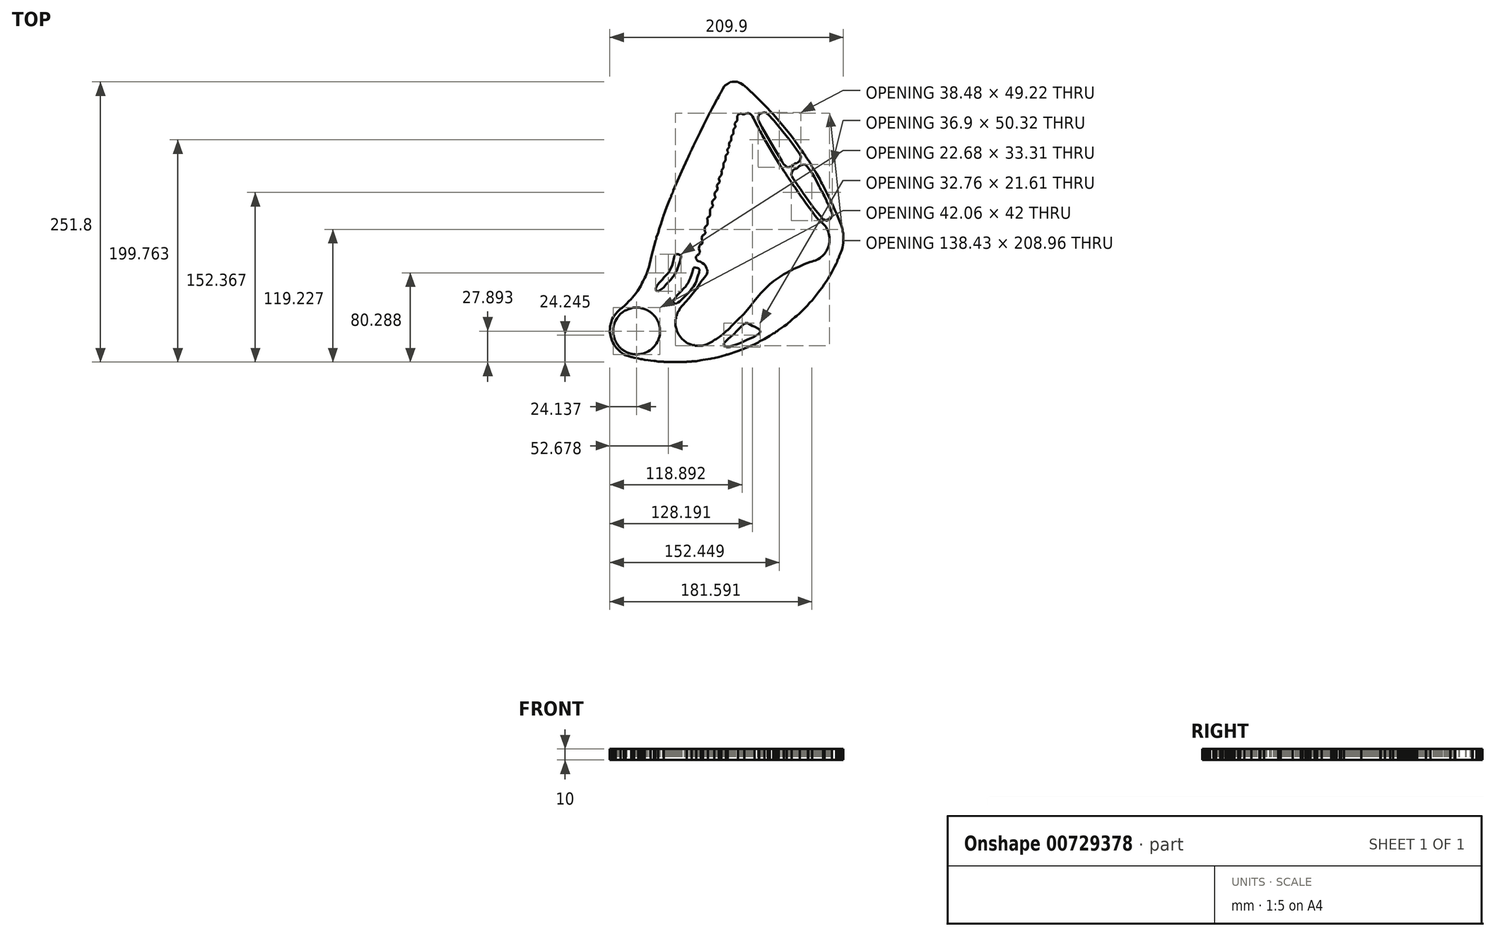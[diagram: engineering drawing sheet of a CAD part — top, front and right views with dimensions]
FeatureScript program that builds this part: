
annotation { "Feature Type Name" : "Feature", "Feature Type Description" : "" }
export const myFeature = defineFeature(function(context is Context, id is Id, definition is map)
    precondition{}
    {
        {
            var Q0;
            Q0=qCreatedBy(makeId("Top.planeOp"),FACE);
            var sketch = newSketch(context, id + "F0", { "sketchPlane" : qUnion([Q0])});
            skLineSegment(sketch, "E0", {"start": v(-166.72, -73.15) * mm, "end": v(-158.5, -73.15) * mm});
            skLineSegment(sketch, "E1", {"start": v(-158.5, -73.15) * mm, "end": v(-154.38, -73.15) * mm});
            skLineSegment(sketch, "E2", {"start": v(-154.38, -73.15) * mm, "end": v(-146.16, -73.15) * mm});
            skLineSegment(sketch, "E3", {"start": v(-146.16, -73.15) * mm, "end": v(-146.16, -73) * mm});
            skLineSegment(sketch, "E4", {"start": v(-146.16, -73) * mm, "end": v(-146.16, -72.91) * mm});
            skLineSegment(sketch, "E5", {"start": v(-146.16, -72.91) * mm, "end": v(-146.16, -72.76) * mm});
            skLineSegment(sketch, "E6", {"start": v(-146.16, -72.76) * mm, "end": v(-144.3, -72.76) * mm});
            skLineSegment(sketch, "E7", {"start": v(-144.3, -72.76) * mm, "end": v(-143.36, -72.76) * mm});
            skLineSegment(sketch, "E8", {"start": v(-143.36, -72.76) * mm, "end": v(-141.5, -72.76) * mm});
            skLineSegment(sketch, "E9", {"start": v(-141.5, -72.76) * mm, "end": v(-141.5, -72.6) * mm});
            skLineSegment(sketch, "E10", {"start": v(-141.5, -72.6) * mm, "end": v(-141.5, -72.53) * mm});
            skLineSegment(sketch, "E11", {"start": v(-141.5, -72.53) * mm, "end": v(-141.5, -72.37) * mm});
            skLineSegment(sketch, "E12", {"start": v(-141.5, -72.37) * mm, "end": v(-139.95, -72.37) * mm});
            skLineSegment(sketch, "E13", {"start": v(-139.95, -72.37) * mm, "end": v(-139.17, -72.37) * mm});
            skLineSegment(sketch, "E14", {"start": v(-139.17, -72.37) * mm, "end": v(-137.62, -72.37) * mm});
            skLineSegment(sketch, "E15", {"start": v(-137.62, -72.37) * mm, "end": v(-133.45, -71.54) * mm});
            skLineSegment(sketch, "E16", {"start": v(-133.45, -71.54) * mm, "end": v(-131.36, -71.2) * mm});
            skLineSegment(sketch, "E17", {"start": v(-131.36, -71.2) * mm, "end": v(-127.15, -70.62) * mm});
            skLineSegment(sketch, "E18", {"start": v(-127.15, -70.62) * mm, "end": v(-124.82, -70.16) * mm});
            skLineSegment(sketch, "E19", {"start": v(-124.82, -70.16) * mm, "end": v(-123.65, -69.93) * mm});
            skLineSegment(sketch, "E20", {"start": v(-123.65, -69.93) * mm, "end": v(-121.33, -69.46) * mm});
            skLineSegment(sketch, "E21", {"start": v(-121.33, -69.46) * mm, "end": v(-117.1, -68.56) * mm});
            skLineSegment(sketch, "E22", {"start": v(-117.1, -68.56) * mm, "end": v(-114.99, -68.02) * mm});
            skLineSegment(sketch, "E23", {"start": v(-114.99, -68.02) * mm, "end": v(-110.85, -66.74) * mm});
            skLineSegment(sketch, "E24", {"start": v(-110.85, -66.74) * mm, "end": v(-110.26, -66.5) * mm});
            skLineSegment(sketch, "E25", {"start": v(-110.26, -66.5) * mm, "end": v(-109.94, -66.42) * mm});
            skLineSegment(sketch, "E26", {"start": v(-109.94, -66.42) * mm, "end": v(-109.3, -66.36) * mm});
            skLineSegment(sketch, "E27", {"start": v(-109.3, -66.36) * mm, "end": v(-105.57, -65.12) * mm});
            skLineSegment(sketch, "E28", {"start": v(-105.57, -65.12) * mm, "end": v(-103.71, -64.5) * mm});
            skLineSegment(sketch, "E29", {"start": v(-103.71, -64.5) * mm, "end": v(-99.99, -63.25) * mm});
            skLineSegment(sketch, "E30", {"start": v(-99.99, -63.25) * mm, "end": v(-97.65, -62.34) * mm});
            skLineSegment(sketch, "E31", {"start": v(-97.65, -62.34) * mm, "end": v(-96.49, -61.87) * mm});
            skLineSegment(sketch, "E32", {"start": v(-96.49, -61.87) * mm, "end": v(-94.17, -60.93) * mm});
            skLineSegment(sketch, "E33", {"start": v(-94.17, -60.93) * mm, "end": v(-90.6, -59.37) * mm});
            skLineSegment(sketch, "E34", {"start": v(-90.6, -59.37) * mm, "end": v(-88.81, -58.6) * mm});
            skLineSegment(sketch, "E35", {"start": v(-88.81, -58.6) * mm, "end": v(-85.24, -57.05) * mm});
            skLineSegment(sketch, "E36", {"start": v(-85.24, -57.05) * mm, "end": v(-83.7, -56.27) * mm});
            skLineSegment(sketch, "E37", {"start": v(-83.7, -56.27) * mm, "end": v(-82.92, -55.88) * mm});
            skLineSegment(sketch, "E38", {"start": v(-82.92, -55.88) * mm, "end": v(-81.36, -55.1) * mm});
            skLineSegment(sketch, "E39", {"start": v(-81.36, -55.1) * mm, "end": v(-81.2, -54.95) * mm});
            skLineSegment(sketch, "E40", {"start": v(-81.2, -54.95) * mm, "end": v(-81.13, -54.87) * mm});
            skLineSegment(sketch, "E41", {"start": v(-81.13, -54.87) * mm, "end": v(-80.98, -54.72) * mm});
            skLineSegment(sketch, "E42", {"start": v(-80.98, -54.72) * mm, "end": v(-79.11, -53.79) * mm});
            skLineSegment(sketch, "E43", {"start": v(-79.11, -53.79) * mm, "end": v(-78.18, -53.32) * mm});
            skLineSegment(sketch, "E44", {"start": v(-78.18, -53.32) * mm, "end": v(-76.32, -52.39) * mm});
            skLineSegment(sketch, "E45", {"start": v(-76.32, -52.39) * mm, "end": v(-73, -50.47) * mm});
            skLineSegment(sketch, "E46", {"start": v(-73, -50.47) * mm, "end": v(-71.37, -49.46) * mm});
            skLineSegment(sketch, "E47", {"start": v(-71.37, -49.46) * mm, "end": v(-68.17, -47.35) * mm});
            skLineSegment(sketch, "E48", {"start": v(-68.17, -47.35) * mm, "end": v(-67.17, -46.84) * mm});
            skLineSegment(sketch, "E49", {"start": v(-67.17, -46.84) * mm, "end": v(-66.7, -46.52) * mm});
            skLineSegment(sketch, "E50", {"start": v(-66.7, -46.52) * mm, "end": v(-65.84, -45.8) * mm});
            skLineSegment(sketch, "E51", {"start": v(-65.84, -45.8) * mm, "end": v(-64.85, -45.29) * mm});
            skLineSegment(sketch, "E52", {"start": v(-64.85, -45.29) * mm, "end": v(-64.37, -44.97) * mm});
            skLineSegment(sketch, "E53", {"start": v(-64.37, -44.97) * mm, "end": v(-63.52, -44.24) * mm});
            skLineSegment(sketch, "E54", {"start": v(-63.52, -44.24) * mm, "end": v(-58.6, -41.03) * mm});
            skLineSegment(sketch, "E55", {"start": v(-58.6, -41.03) * mm, "end": v(-56.25, -39.23) * mm});
            skLineSegment(sketch, "E56", {"start": v(-56.25, -39.23) * mm, "end": v(-51.88, -35.32) * mm});
            skLineSegment(sketch, "E57", {"start": v(-51.88, -35.32) * mm, "end": v(-48.92, -32.85) * mm});
            skLineSegment(sketch, "E58", {"start": v(-48.92, -32.85) * mm, "end": v(-47.44, -31.6) * mm});
            skLineSegment(sketch, "E59", {"start": v(-47.44, -31.6) * mm, "end": v(-44.5, -29.11) * mm});
            skLineSegment(sketch, "E60", {"start": v(-44.5, -29.11) * mm, "end": v(-41.63, -26.24) * mm});
            skLineSegment(sketch, "E61", {"start": v(-41.63, -26.24) * mm, "end": v(-40.2, -24.8) * mm});
            skLineSegment(sketch, "E62", {"start": v(-40.2, -24.8) * mm, "end": v(-37.33, -21.93) * mm});
            skLineSegment(sketch, "E63", {"start": v(-37.33, -21.93) * mm, "end": v(-37.17, -21.62) * mm});
            skLineSegment(sketch, "E64", {"start": v(-37.17, -21.62) * mm, "end": v(-37.1, -21.47) * mm});
            skLineSegment(sketch, "E65", {"start": v(-37.1, -21.47) * mm, "end": v(-36.94, -21.16) * mm});
            skLineSegment(sketch, "E66", {"start": v(-36.94, -21.16) * mm, "end": v(-35.54, -19.76) * mm});
            skLineSegment(sketch, "E67", {"start": v(-35.54, -19.76) * mm, "end": v(-34.85, -19.06) * mm});
            skLineSegment(sketch, "E68", {"start": v(-34.85, -19.06) * mm, "end": v(-33.45, -17.67) * mm});
            skLineSegment(sketch, "E69", {"start": v(-33.45, -17.67) * mm, "end": v(-29.48, -12.63) * mm});
            skLineSegment(sketch, "E70", {"start": v(-29.48, -12.63) * mm, "end": v(-27.5, -10.11) * mm});
            skLineSegment(sketch, "E71", {"start": v(-27.5, -10.11) * mm, "end": v(-23.56, -5.06) * mm});
            skLineSegment(sketch, "E72", {"start": v(-23.56, -5.06) * mm, "end": v(-23.23, -4.1) * mm});
            skLineSegment(sketch, "E73", {"start": v(-23.23, -4.1) * mm, "end": v(-22.93, -3.62) * mm});
            skLineSegment(sketch, "E74", {"start": v(-22.93, -3.62) * mm, "end": v(-22.2, -2.92) * mm});
            skLineSegment(sketch, "E75", {"start": v(-22.2, -2.92) * mm, "end": v(-19.54, 1.41) * mm});
            skLineSegment(sketch, "E76", {"start": v(-19.54, 1.41) * mm, "end": v(-18.22, 3.59) * mm});
            skLineSegment(sketch, "E77", {"start": v(-18.22, 3.59) * mm, "end": v(-15.6, 7.94) * mm});
            skLineSegment(sketch, "E78", {"start": v(-15.6, 7.94) * mm, "end": v(-14.13, 10.89) * mm});
            skLineSegment(sketch, "E79", {"start": v(-14.13, 10.89) * mm, "end": v(-13.4, 12.36) * mm});
            skLineSegment(sketch, "E80", {"start": v(-13.4, 12.36) * mm, "end": v(-11.92, 15.31) * mm});
            skLineSegment(sketch, "E81", {"start": v(-11.92, 15.31) * mm, "end": v(-11.81, 15.62) * mm});
            skLineSegment(sketch, "E82", {"start": v(-11.81, 15.62) * mm, "end": v(-11.37, 15.72) * mm});
            skLineSegment(sketch, "E83", {"start": v(-6.48, 47.32) * mm, "end": v(-7.32, 50.1) * mm});
            skLineSegment(sketch, "E84", {"start": v(-7.32, 50.1) * mm, "end": v(-7.83, 51.46) * mm});
            skLineSegment(sketch, "E85", {"start": v(-7.83, 51.46) * mm, "end": v(-9, 54.11) * mm});
            skLineSegment(sketch, "E86", {"start": v(-9, 54.11) * mm, "end": v(-11.6, 60.33) * mm});
            skLineSegment(sketch, "E87", {"start": v(-11.6, 60.33) * mm, "end": v(-12.93, 63.44) * mm});
            skLineSegment(sketch, "E88", {"start": v(-12.93, 63.44) * mm, "end": v(-15.6, 69.63) * mm});
            skLineSegment(sketch, "E89", {"start": v(-15.6, 69.63) * mm, "end": v(-19.02, 76.46) * mm});
            skLineSegment(sketch, "E90", {"start": v(-19.02, 76.46) * mm, "end": v(-20.72, 79.87) * mm});
            skLineSegment(sketch, "E91", {"start": v(-20.72, 79.87) * mm, "end": v(-24.14, 86.7) * mm});
            skLineSegment(sketch, "E92", {"start": v(-24.14, 86.7) * mm, "end": v(-24.3, 86.86) * mm});
            skLineSegment(sketch, "E93", {"start": v(-24.3, 86.86) * mm, "end": v(-24.37, 86.93) * mm});
            skLineSegment(sketch, "E94", {"start": v(-24.37, 86.93) * mm, "end": v(-24.53, 87.09) * mm});
            skLineSegment(sketch, "E95", {"start": v(-24.53, 87.09) * mm, "end": v(-25.3, 88.64) * mm});
            skLineSegment(sketch, "E96", {"start": v(-25.3, 88.64) * mm, "end": v(-25.69, 89.42) * mm});
            skLineSegment(sketch, "E97", {"start": v(-25.69, 89.42) * mm, "end": v(-26.47, 90.97) * mm});
            skLineSegment(sketch, "E98", {"start": v(-26.47, 90.97) * mm, "end": v(-29.11, 95.75) * mm});
            skLineSegment(sketch, "E99", {"start": v(-29.11, 95.75) * mm, "end": v(-30.56, 98.1) * mm});
            skLineSegment(sketch, "E100", {"start": v(-30.56, 98.1) * mm, "end": v(-33.64, 102.6) * mm});
            skLineSegment(sketch, "E101", {"start": v(-33.64, 102.6) * mm, "end": v(-34.05, 103.97) * mm});
            skLineSegment(sketch, "E102", {"start": v(-34.05, 103.97) * mm, "end": v(-34.43, 104.66) * mm});
            skLineSegment(sketch, "E103", {"start": v(-34.43, 104.66) * mm, "end": v(-35.39, 105.71) * mm});
            skLineSegment(sketch, "E104", {"start": v(-35.39, 105.71) * mm, "end": v(-36.35, 107.5) * mm});
            skLineSegment(sketch, "E105", {"start": v(-36.35, 107.5) * mm, "end": v(-36.9, 108.36) * mm});
            skLineSegment(sketch, "E106", {"start": v(-36.9, 108.36) * mm, "end": v(-38.1, 109.98) * mm});
            skLineSegment(sketch, "E107", {"start": v(-38.1, 109.98) * mm, "end": v(-38.61, 110.98) * mm});
            skLineSegment(sketch, "E108", {"start": v(-38.61, 110.98) * mm, "end": v(-38.93, 111.46) * mm});
            skLineSegment(sketch, "E109", {"start": v(-38.93, 111.46) * mm, "end": v(-39.66, 112.3) * mm});
            skLineSegment(sketch, "E110", {"start": v(-39.66, 112.3) * mm, "end": v(-40.16, 113.3) * mm});
            skLineSegment(sketch, "E111", {"start": v(-40.16, 113.3) * mm, "end": v(-40.48, 113.78) * mm});
            skLineSegment(sketch, "E112", {"start": v(-40.48, 113.78) * mm, "end": v(-41.2, 114.63) * mm});
            skLineSegment(sketch, "E113", {"start": v(-41.2, 114.63) * mm, "end": v(-42.1, 116.36) * mm});
            skLineSegment(sketch, "E114", {"start": v(-42.1, 116.36) * mm, "end": v(-42.71, 117.18) * mm});
            skLineSegment(sketch, "E115", {"start": v(-42.71, 117.18) * mm, "end": v(-44.12, 118.51) * mm});
            skLineSegment(sketch, "E116", {"start": v(-44.12, 118.51) * mm, "end": v(-44.03, 119.03) * mm});
            skLineSegment(sketch, "E117", {"start": v(-44.03, 119.03) * mm, "end": v(-44.24, 119.44) * mm});
            skLineSegment(sketch, "E118", {"start": v(-44.24, 119.44) * mm, "end": v(-44.7, 119.68) * mm});
            skLineSegment(sketch, "E119", {"start": v(-44.7, 119.68) * mm, "end": v(-50.32, 127.77) * mm});
            skLineSegment(sketch, "E120", {"start": v(-50.32, 127.77) * mm, "end": v(-53.32, 131.7) * mm});
            skLineSegment(sketch, "E121", {"start": v(-53.32, 131.7) * mm, "end": v(-59.64, 139.27) * mm});
            skLineSegment(sketch, "E122", {"start": v(-59.64, 139.27) * mm, "end": v(-63.14, 143.38) * mm});
            skLineSegment(sketch, "E123", {"start": v(-63.14, 143.38) * mm, "end": v(-64.88, 145.43) * mm});
            skLineSegment(sketch, "E124", {"start": v(-64.88, 145.43) * mm, "end": v(-68.37, 149.55) * mm});
            skLineSegment(sketch, "E125", {"start": v(-68.37, 149.55) * mm, "end": v(-69.92, 151.1) * mm});
            skLineSegment(sketch, "E126", {"start": v(-69.92, 151.1) * mm, "end": v(-70.7, 151.88) * mm});
            skLineSegment(sketch, "E127", {"start": v(-70.7, 151.88) * mm, "end": v(-72.25, 153.43) * mm});
            skLineSegment(sketch, "E128", {"start": v(-72.25, 153.43) * mm, "end": v(-72.4, 153.74) * mm});
            skLineSegment(sketch, "E129", {"start": v(-72.4, 153.74) * mm, "end": v(-72.48, 153.9) * mm});
            skLineSegment(sketch, "E130", {"start": v(-72.48, 153.9) * mm, "end": v(-72.63, 154.2) * mm});
            skLineSegment(sketch, "E131", {"start": v(-72.63, 154.2) * mm, "end": v(-78.6, 160.18) * mm});
            skLineSegment(sketch, "E132", {"start": v(-78.6, 160.18) * mm, "end": v(-81.6, 163.17) * mm});
            skLineSegment(sketch, "E133", {"start": v(-81.6, 163.17) * mm, "end": v(-87.57, 169.15) * mm});
            skLineSegment(sketch, "E134", {"start": v(-87.57, 169.15) * mm, "end": v(-87.88, 169.3) * mm});
            skLineSegment(sketch, "E135", {"start": v(-87.88, 169.3) * mm, "end": v(-88.04, 169.38) * mm});
            skLineSegment(sketch, "E136", {"start": v(-88.04, 169.38) * mm, "end": v(-88.35, 169.53) * mm});
            skLineSegment(sketch, "E137", {"start": v(-88.35, 169.53) * mm, "end": v(-89.74, 170.93) * mm});
            skLineSegment(sketch, "E138", {"start": v(-89.74, 170.93) * mm, "end": v(-90.44, 171.63) * mm});
            skLineSegment(sketch, "E139", {"start": v(-90.44, 171.63) * mm, "end": v(-91.84, 173.03) * mm});
            skLineSegment(sketch, "E140", {"start": v(-91.84, 173.03) * mm, "end": v(-94.02, 174.98) * mm});
            skLineSegment(sketch, "E141", {"start": v(-94.02, 174.98) * mm, "end": v(-95.2, 175.89) * mm});
            skLineSegment(sketch, "E142", {"start": v(-95.2, 175.89) * mm, "end": v(-97.66, 177.49) * mm});
            skLineSegment(sketch, "E143", {"start": v(-97.66, 177.49) * mm, "end": v(-98.78, 177.87) * mm});
            skLineSegment(sketch, "E144", {"start": v(-98.78, 177.87) * mm, "end": v(-99.33, 178.1) * mm});
            skLineSegment(sketch, "E145", {"start": v(-99.33, 178.1) * mm, "end": v(-100.37, 178.65) * mm});
            skLineSegment(sketch, "E146", {"start": v(-100.37, 178.65) * mm, "end": v(-102.31, 178.65) * mm});
            skLineSegment(sketch, "E147", {"start": v(-102.31, 178.65) * mm, "end": v(-103.28, 178.65) * mm});
            skLineSegment(sketch, "E148", {"start": v(-103.28, 178.65) * mm, "end": v(-105.22, 178.65) * mm});
            skLineSegment(sketch, "E149", {"start": v(-105.22, 178.65) * mm, "end": v(-106.96, 178.31) * mm});
            skLineSegment(sketch, "E150", {"start": v(-106.96, 178.31) * mm, "end": v(-107.85, 177.93) * mm});
            skLineSegment(sketch, "E151", {"start": v(-107.85, 177.93) * mm, "end": v(-109.3, 176.9) * mm});
            skLineSegment(sketch, "E152", {"start": v(-109.3, 176.9) * mm, "end": v(-111.4, 175.61) * mm});
            skLineSegment(sketch, "E153", {"start": v(-111.4, 175.61) * mm, "end": v(-112.37, 174.6) * mm});
            skLineSegment(sketch, "E154", {"start": v(-112.37, 174.6) * mm, "end": v(-113.57, 172.44) * mm});
            skLineSegment(sketch, "E155", {"start": v(-113.57, 172.44) * mm, "end": v(-114.64, 170.38) * mm});
            skLineSegment(sketch, "E156", {"start": v(-114.64, 170.38) * mm, "end": v(-115.23, 169.36) * mm});
            skLineSegment(sketch, "E157", {"start": v(-115.23, 169.36) * mm, "end": v(-116.48, 167.4) * mm});
            skLineSegment(sketch, "E158", {"start": v(-116.48, 167.4) * mm, "end": v(-117.25, 165.85) * mm});
            skLineSegment(sketch, "E159", {"start": v(-117.25, 165.85) * mm, "end": v(-117.64, 165.07) * mm});
            skLineSegment(sketch, "E160", {"start": v(-117.64, 165.07) * mm, "end": v(-118.42, 163.52) * mm});
            skLineSegment(sketch, "E161", {"start": v(-118.42, 163.52) * mm, "end": v(-118.57, 163.36) * mm});
            skLineSegment(sketch, "E162", {"start": v(-118.57, 163.36) * mm, "end": v(-118.65, 163.29) * mm});
            skLineSegment(sketch, "E163", {"start": v(-118.65, 163.29) * mm, "end": v(-118.8, 163.13) * mm});
            skLineSegment(sketch, "E164", {"start": v(-118.8, 163.13) * mm, "end": v(-119.89, 160.96) * mm});
            skLineSegment(sketch, "E165", {"start": v(-119.89, 160.96) * mm, "end": v(-120.43, 159.87) * mm});
            skLineSegment(sketch, "E166", {"start": v(-120.43, 159.87) * mm, "end": v(-121.52, 157.7) * mm});
            skLineSegment(sketch, "E167", {"start": v(-121.52, 157.7) * mm, "end": v(-121.67, 157.54) * mm});
            skLineSegment(sketch, "E168", {"start": v(-121.67, 157.54) * mm, "end": v(-121.75, 157.47) * mm});
            skLineSegment(sketch, "E169", {"start": v(-121.75, 157.47) * mm, "end": v(-121.9, 157.31) * mm});
            skLineSegment(sketch, "E170", {"start": v(-121.9, 157.31) * mm, "end": v(-123.15, 154.83) * mm});
            skLineSegment(sketch, "E171", {"start": v(-123.15, 154.83) * mm, "end": v(-123.77, 153.59) * mm});
            skLineSegment(sketch, "E172", {"start": v(-123.77, 153.59) * mm, "end": v(-125.01, 151.1) * mm});
            skLineSegment(sketch, "E173", {"start": v(-125.01, 151.1) * mm, "end": v(-125.17, 150.95) * mm});
            skLineSegment(sketch, "E174", {"start": v(-125.17, 150.95) * mm, "end": v(-125.24, 150.87) * mm});
            skLineSegment(sketch, "E175", {"start": v(-125.24, 150.87) * mm, "end": v(-125.4, 150.72) * mm});
            skLineSegment(sketch, "E176", {"start": v(-125.4, 150.72) * mm, "end": v(-131.14, 139.23) * mm});
            skLineSegment(sketch, "E177", {"start": v(-131.14, 139.23) * mm, "end": v(-134.01, 133.5) * mm});
            skLineSegment(sketch, "E178", {"start": v(-134.01, 133.5) * mm, "end": v(-139.75, 122) * mm});
            skLineSegment(sketch, "E179", {"start": v(-139.75, 122) * mm, "end": v(-139.9, 121.54) * mm});
            skLineSegment(sketch, "E180", {"start": v(-139.9, 121.54) * mm, "end": v(-139.99, 121.3) * mm});
            skLineSegment(sketch, "E181", {"start": v(-139.99, 121.3) * mm, "end": v(-140.14, 120.84) * mm});
            skLineSegment(sketch, "E182", {"start": v(-140.14, 120.84) * mm, "end": v(-141.23, 118.67) * mm});
            skLineSegment(sketch, "E183", {"start": v(-141.23, 118.67) * mm, "end": v(-141.77, 117.58) * mm});
            skLineSegment(sketch, "E184", {"start": v(-141.77, 117.58) * mm, "end": v(-142.86, 115.41) * mm});
            skLineSegment(sketch, "E185", {"start": v(-142.86, 115.41) * mm, "end": v(-143.01, 114.95) * mm});
            skLineSegment(sketch, "E186", {"start": v(-143.01, 114.95) * mm, "end": v(-143.1, 114.71) * mm});
            skLineSegment(sketch, "E187", {"start": v(-143.1, 114.71) * mm, "end": v(-143.25, 114.25) * mm});
            skLineSegment(sketch, "E188", {"start": v(-143.25, 114.25) * mm, "end": v(-144.18, 112.38) * mm});
            skLineSegment(sketch, "E189", {"start": v(-144.18, 112.38) * mm, "end": v(-144.64, 111.45) * mm});
            skLineSegment(sketch, "E190", {"start": v(-144.64, 111.45) * mm, "end": v(-145.57, 109.6) * mm});
            skLineSegment(sketch, "E191", {"start": v(-145.57, 109.6) * mm, "end": v(-150.57, 98.27) * mm});
            skLineSegment(sketch, "E192", {"start": v(-150.57, 98.27) * mm, "end": v(-153.05, 92.6) * mm});
            skLineSegment(sketch, "E193", {"start": v(-153.05, 92.6) * mm, "end": v(-157.99, 81.27) * mm});
            skLineSegment(sketch, "E194", {"start": v(-157.99, 81.27) * mm, "end": v(-158.58, 79.3) * mm});
            skLineSegment(sketch, "E195", {"start": v(-158.58, 79.3) * mm, "end": v(-159.02, 78.34) * mm});
            skLineSegment(sketch, "E196", {"start": v(-159.02, 78.34) * mm, "end": v(-160.12, 76.61) * mm});
            skLineSegment(sketch, "E197", {"start": v(-160.12, 76.61) * mm, "end": v(-160.01, 75.81) * mm});
            skLineSegment(sketch, "E198", {"start": v(-160.01, 75.81) * mm, "end": v(-160.17, 75.28) * mm});
            skLineSegment(sketch, "E199", {"start": v(-160.17, 75.28) * mm, "end": v(-160.7, 74.67) * mm});
            skLineSegment(sketch, "E200", {"start": v(-160.7, 74.67) * mm, "end": v(-161.25, 73.1) * mm});
            skLineSegment(sketch, "E201", {"start": v(-161.25, 73.1) * mm, "end": v(-161.56, 72.31) * mm});
            skLineSegment(sketch, "E202", {"start": v(-161.56, 72.31) * mm, "end": v(-162.26, 70.8) * mm});
            skLineSegment(sketch, "E203", {"start": v(-162.26, 70.8) * mm, "end": v(-163.48, 67.53) * mm});
            skLineSegment(sketch, "E204", {"start": v(-163.48, 67.53) * mm, "end": v(-164.1, 65.9) * mm});
            skLineSegment(sketch, "E205", {"start": v(-164.1, 65.9) * mm, "end": v(-165.36, 62.65) * mm});
            skLineSegment(sketch, "E206", {"start": v(-165.36, 62.65) * mm, "end": v(-165.98, 60.78) * mm});
            skLineSegment(sketch, "E207", {"start": v(-165.98, 60.78) * mm, "end": v(-166.3, 59.85) * mm});
            skLineSegment(sketch, "E208", {"start": v(-166.3, 59.85) * mm, "end": v(-166.91, 57.99) * mm});
            skLineSegment(sketch, "E209", {"start": v(-166.91, 57.99) * mm, "end": v(-167.07, 57.68) * mm});
            skLineSegment(sketch, "E210", {"start": v(-167.07, 57.68) * mm, "end": v(-167.15, 57.52) * mm});
            skLineSegment(sketch, "E211", {"start": v(-167.15, 57.52) * mm, "end": v(-167.3, 57.21) * mm});
            skLineSegment(sketch, "E212", {"start": v(-167.3, 57.21) * mm, "end": v(-168.7, 53.02) * mm});
            skLineSegment(sketch, "E213", {"start": v(-168.7, 53.02) * mm, "end": v(-169.4, 50.93) * mm});
            skLineSegment(sketch, "E214", {"start": v(-169.4, 50.93) * mm, "end": v(-170.8, 46.74) * mm});
            skLineSegment(sketch, "E215", {"start": v(-170.8, 46.74) * mm, "end": v(-171.52, 43.56) * mm});
            skLineSegment(sketch, "E216", {"start": v(-171.52, 43.56) * mm, "end": v(-172.03, 41.98) * mm});
            skLineSegment(sketch, "E217", {"start": v(-172.03, 41.98) * mm, "end": v(-173.31, 38.98) * mm});
            skLineSegment(sketch, "E218", {"start": v(-173.31, 38.98) * mm, "end": v(-173.26, 37.87) * mm});
            skLineSegment(sketch, "E219", {"start": v(-173.26, 37.87) * mm, "end": v(-173.4, 37.25) * mm});
            skLineSegment(sketch, "E220", {"start": v(-173.4, 37.25) * mm, "end": v(-173.9, 36.26) * mm});
            skLineSegment(sketch, "E221", {"start": v(-173.9, 36.26) * mm, "end": v(-176.43, 26.66) * mm});
            skLineSegment(sketch, "E222", {"start": v(-176.43, 26.66) * mm, "end": v(-177.67, 21.84) * mm});
            skLineSegment(sketch, "E223", {"start": v(-177.67, 21.84) * mm, "end": v(-180.1, 12.2) * mm});
            skLineSegment(sketch, "E224", {"start": v(-180.1, 12.2) * mm, "end": v(-180.72, 10.35) * mm});
            skLineSegment(sketch, "E225", {"start": v(-180.72, 10.35) * mm, "end": v(-181.04, 9.42) * mm});
            skLineSegment(sketch, "E226", {"start": v(-181.04, 9.42) * mm, "end": v(-181.66, 7.55) * mm});
            skLineSegment(sketch, "E227", {"start": v(-181.66, 7.55) * mm, "end": v(-182.98, 4.15) * mm});
            skLineSegment(sketch, "E228", {"start": v(-182.98, 4.15) * mm, "end": v(-183.72, 2.48) * mm});
            skLineSegment(sketch, "E229", {"start": v(-183.72, 2.48) * mm, "end": v(-185.34, -0.79) * mm});
            skLineSegment(sketch, "E230", {"start": v(-185.34, -0.79) * mm, "end": v(-186.29, -2.37) * mm});
            skLineSegment(sketch, "E231", {"start": v(-186.29, -2.37) * mm, "end": v(-186.72, -3.19) * mm});
            skLineSegment(sketch, "E232", {"start": v(-186.72, -3.19) * mm, "end": v(-187.48, -4.86) * mm});
            skLineSegment(sketch, "E233", {"start": v(-187.48, -4.86) * mm, "end": v(-190.18, -9.2) * mm});
            skLineSegment(sketch, "E234", {"start": v(-190.18, -9.2) * mm, "end": v(-191.7, -11.27) * mm});
            skLineSegment(sketch, "E235", {"start": v(-191.7, -11.27) * mm, "end": v(-195.04, -15.14) * mm});
            skLineSegment(sketch, "E236", {"start": v(-195.04, -15.14) * mm, "end": v(-195.34, -15.48) * mm});
            skLineSegment(sketch, "E237", {"start": v(-195.34, -15.48) * mm, "end": v(-195.46, -15.7) * mm});
            skLineSegment(sketch, "E238", {"start": v(-195.46, -15.7) * mm, "end": v(-195.62, -16.11) * mm});
            skLineSegment(sketch, "E239", {"start": v(-195.62, -16.11) * mm, "end": v(-198.34, -18.83) * mm});
            skLineSegment(sketch, "E240", {"start": v(-198.34, -18.83) * mm, "end": v(-199.7, -20.19) * mm});
            skLineSegment(sketch, "E241", {"start": v(-199.7, -20.19) * mm, "end": v(-202.41, -22.9) * mm});
            skLineSegment(sketch, "E242", {"start": v(-202.41, -22.9) * mm, "end": v(-203.65, -23.83) * mm});
            skLineSegment(sketch, "E243", {"start": v(-203.65, -23.83) * mm, "end": v(-204.28, -24.3) * mm});
            skLineSegment(sketch, "E244", {"start": v(-204.28, -24.3) * mm, "end": v(-205.52, -25.23) * mm});
            skLineSegment(sketch, "E245", {"start": v(-205.52, -25.23) * mm, "end": v(-207.3, -27.02) * mm});
            skLineSegment(sketch, "E246", {"start": v(-207.3, -27.02) * mm, "end": v(-208.2, -27.9) * mm});
            skLineSegment(sketch, "E247", {"start": v(-208.2, -27.9) * mm, "end": v(-209.98, -29.7) * mm});
            skLineSegment(sketch, "E248", {"start": v(-209.98, -29.7) * mm, "end": v(-212.07, -32.68) * mm});
            skLineSegment(sketch, "E249", {"start": v(-212.07, -32.68) * mm, "end": v(-212.92, -34.38) * mm});
            skLineSegment(sketch, "E250", {"start": v(-212.92, -34.38) * mm, "end": v(-214.05, -37.84) * mm});
            skLineSegment(sketch, "E251", {"start": v(-214.05, -37.84) * mm, "end": v(-214.84, -40.88) * mm});
            skLineSegment(sketch, "E252", {"start": v(-214.84, -40.88) * mm, "end": v(-215.07, -42.46) * mm});
            skLineSegment(sketch, "E253", {"start": v(-215.07, -42.46) * mm, "end": v(-215.22, -45.6) * mm});
            skLineSegment(sketch, "E254", {"start": v(-215.22, -45.6) * mm, "end": v(-214.66, -48.73) * mm});
            skLineSegment(sketch, "E255", {"start": v(-214.66, -48.73) * mm, "end": v(-214.3, -50.3) * mm});
            skLineSegment(sketch, "E256", {"start": v(-214.3, -50.3) * mm, "end": v(-213.47, -53.36) * mm});
            skLineSegment(sketch, "E257", {"start": v(-213.47, -53.36) * mm, "end": v(-212.7, -54.91) * mm});
            skLineSegment(sketch, "E258", {"start": v(-212.7, -54.91) * mm, "end": v(-212.3, -55.69) * mm});
            skLineSegment(sketch, "E259", {"start": v(-212.3, -55.69) * mm, "end": v(-211.53, -57.24) * mm});
            skLineSegment(sketch, "E260", {"start": v(-211.53, -57.24) * mm, "end": v(-210.79, -58.08) * mm});
            skLineSegment(sketch, "E261", {"start": v(-210.79, -58.08) * mm, "end": v(-210.47, -58.56) * mm});
            skLineSegment(sketch, "E262", {"start": v(-210.47, -58.56) * mm, "end": v(-209.98, -59.57) * mm});
            skLineSegment(sketch, "E263", {"start": v(-209.98, -59.57) * mm, "end": v(-208.2, -61.35) * mm});
            skLineSegment(sketch, "E264", {"start": v(-208.2, -61.35) * mm, "end": v(-207.3, -62.24) * mm});
            skLineSegment(sketch, "E265", {"start": v(-207.3, -62.24) * mm, "end": v(-205.52, -64.03) * mm});
            skLineSegment(sketch, "E266", {"start": v(-205.52, -64.03) * mm, "end": v(-202.68, -66.03) * mm});
            skLineSegment(sketch, "E267", {"start": v(-202.68, -66.03) * mm, "end": v(-201.06, -66.84) * mm});
            skLineSegment(sketch, "E268", {"start": v(-201.06, -66.84) * mm, "end": v(-197.76, -67.9) * mm});
            skLineSegment(sketch, "E269", {"start": v(-197.76, -67.9) * mm, "end": v(-196.07, -68.45) * mm});
            skLineSegment(sketch, "E270", {"start": v(-196.07, -68.45) * mm, "end": v(-195.22, -68.68) * mm});
            skLineSegment(sketch, "E271", {"start": v(-195.22, -68.68) * mm, "end": v(-193.49, -69.07) * mm});
            skLineSegment(sketch, "E272", {"start": v(-193.49, -69.07) * mm, "end": v(-191.94, -69.38) * mm});
            skLineSegment(sketch, "E273", {"start": v(-191.94, -69.38) * mm, "end": v(-191.16, -69.54) * mm});
            skLineSegment(sketch, "E274", {"start": v(-191.16, -69.54) * mm, "end": v(-189.6, -69.85) * mm});
            skLineSegment(sketch, "E275", {"start": v(-189.6, -69.85) * mm, "end": v(-187.3, -70.39) * mm});
            skLineSegment(sketch, "E276", {"start": v(-187.3, -70.39) * mm, "end": v(-186.13, -70.62) * mm});
            skLineSegment(sketch, "E277", {"start": v(-186.13, -70.62) * mm, "end": v(-183.79, -71.01) * mm});
            skLineSegment(sketch, "E278", {"start": v(-183.79, -71.01) * mm, "end": v(-181.62, -71.32) * mm});
            skLineSegment(sketch, "E279", {"start": v(-181.62, -71.32) * mm, "end": v(-180.53, -71.48) * mm});
            skLineSegment(sketch, "E280", {"start": v(-180.53, -71.48) * mm, "end": v(-178.36, -71.79) * mm});
            skLineSegment(sketch, "E281", {"start": v(-178.36, -71.79) * mm, "end": v(-175.7, -71.93) * mm});
            skLineSegment(sketch, "E282", {"start": v(-175.7, -71.93) * mm, "end": v(-174.35, -72.13) * mm});
            skLineSegment(sketch, "E283", {"start": v(-174.35, -72.13) * mm, "end": v(-171.76, -72.76) * mm});
            skLineSegment(sketch, "E284", {"start": v(-171.76, -72.76) * mm, "end": v(-169.75, -72.76) * mm});
            skLineSegment(sketch, "E285", {"start": v(-169.75, -72.76) * mm, "end": v(-168.74, -72.76) * mm});
            skLineSegment(sketch, "E286", {"start": v(-168.74, -72.76) * mm, "end": v(-166.72, -72.76) * mm});
            skLineSegment(sketch, "E287", {"start": v(-166.72, -72.76) * mm, "end": v(-166.72, -72.91) * mm});
            skLineSegment(sketch, "E288", {"start": v(-166.72, -72.91) * mm, "end": v(-166.72, -73) * mm});
            skLineSegment(sketch, "E289", {"start": v(-166.72, -73) * mm, "end": v(-166.72, -73.15) * mm});
            skLineSegment(sketch, "E290", {"start": v(-164, -71.98) * mm, "end": v(-158.1, -71.98) * mm});
            skLineSegment(sketch, "E291", {"start": v(-158.1, -71.98) * mm, "end": v(-155.16, -71.98) * mm});
            skLineSegment(sketch, "E292", {"start": v(-155.16, -71.98) * mm, "end": v(-149.26, -71.98) * mm});
            skLineSegment(sketch, "E293", {"start": v(-149.26, -71.98) * mm, "end": v(-149.26, -71.83) * mm});
            skLineSegment(sketch, "E294", {"start": v(-149.26, -71.83) * mm, "end": v(-149.26, -71.75) * mm});
            skLineSegment(sketch, "E295", {"start": v(-149.26, -71.75) * mm, "end": v(-149.26, -71.6) * mm});
            skLineSegment(sketch, "E296", {"start": v(-149.26, -71.6) * mm, "end": v(-146.78, -71.6) * mm});
            skLineSegment(sketch, "E297", {"start": v(-146.78, -71.6) * mm, "end": v(-145.54, -71.6) * mm});
            skLineSegment(sketch, "E298", {"start": v(-145.54, -71.6) * mm, "end": v(-143.05, -71.6) * mm});
            skLineSegment(sketch, "E299", {"start": v(-143.05, -71.6) * mm, "end": v(-143.05, -71.44) * mm});
            skLineSegment(sketch, "E300", {"start": v(-143.05, -71.44) * mm, "end": v(-143.05, -71.36) * mm});
            skLineSegment(sketch, "E301", {"start": v(-143.05, -71.36) * mm, "end": v(-143.05, -71.2) * mm});
            skLineSegment(sketch, "E302", {"start": v(-143.05, -71.2) * mm, "end": v(-141.35, -71.2) * mm});
            skLineSegment(sketch, "E303", {"start": v(-141.35, -71.2) * mm, "end": v(-140.5, -71.2) * mm});
            skLineSegment(sketch, "E304", {"start": v(-140.5, -71.2) * mm, "end": v(-138.78, -71.2) * mm});
            skLineSegment(sketch, "E305", {"start": v(-138.78, -71.2) * mm, "end": v(-137.65, -70.65) * mm});
            skLineSegment(sketch, "E306", {"start": v(-137.65, -70.65) * mm, "end": v(-136.94, -70.52) * mm});
            skLineSegment(sketch, "E307", {"start": v(-136.94, -70.52) * mm, "end": v(-135.68, -70.62) * mm});
            skLineSegment(sketch, "E308", {"start": v(-135.68, -70.62) * mm, "end": v(-133.5, -70.31) * mm});
            skLineSegment(sketch, "E309", {"start": v(-133.5, -70.31) * mm, "end": v(-132.42, -70.16) * mm});
            skLineSegment(sketch, "E310", {"start": v(-132.42, -70.16) * mm, "end": v(-130.25, -69.85) * mm});
            skLineSegment(sketch, "E311", {"start": v(-130.25, -69.85) * mm, "end": v(-129.31, -69.73) * mm});
            skLineSegment(sketch, "E312", {"start": v(-129.31, -69.73) * mm, "end": v(-128.84, -69.66) * mm});
            skLineSegment(sketch, "E313", {"start": v(-128.84, -69.66) * mm, "end": v(-127.92, -69.46) * mm});
            skLineSegment(sketch, "E314", {"start": v(-127.92, -69.46) * mm, "end": v(-125.6, -69) * mm});
            skLineSegment(sketch, "E315", {"start": v(-125.6, -69) * mm, "end": v(-124.43, -68.76) * mm});
            skLineSegment(sketch, "E316", {"start": v(-124.43, -68.76) * mm, "end": v(-122.1, -68.3) * mm});
            skLineSegment(sketch, "E317", {"start": v(-122.1, -68.3) * mm, "end": v(-120.71, -67.94) * mm});
            skLineSegment(sketch, "E318", {"start": v(-120.71, -67.94) * mm, "end": v(-120.02, -67.79) * mm});
            skLineSegment(sketch, "E319", {"start": v(-120.02, -67.79) * mm, "end": v(-118.6, -67.52) * mm});
            skLineSegment(sketch, "E320", {"start": v(-118.6, -67.52) * mm, "end": v(-116.75, -67.06) * mm});
            skLineSegment(sketch, "E321", {"start": v(-116.75, -67.06) * mm, "end": v(-115.82, -66.82) * mm});
            skLineSegment(sketch, "E322", {"start": v(-115.82, -66.82) * mm, "end": v(-113.95, -66.36) * mm});
            skLineSegment(sketch, "E323", {"start": v(-113.95, -66.36) * mm, "end": v(-111.32, -65.57) * mm});
            skLineSegment(sketch, "E324", {"start": v(-111.32, -65.57) * mm, "end": v(-110, -65.18) * mm});
            skLineSegment(sketch, "E325", {"start": v(-110, -65.18) * mm, "end": v(-107.36, -64.42) * mm});
            skLineSegment(sketch, "E326", {"start": v(-107.36, -64.42) * mm, "end": v(-105.03, -63.64) * mm});
            skLineSegment(sketch, "E327", {"start": v(-105.03, -63.64) * mm, "end": v(-103.87, -63.25) * mm});
            skLineSegment(sketch, "E328", {"start": v(-103.87, -63.25) * mm, "end": v(-101.54, -62.48) * mm});
            skLineSegment(sketch, "E329", {"start": v(-101.54, -62.48) * mm, "end": v(-99.2, -61.56) * mm});
            skLineSegment(sketch, "E330", {"start": v(-99.2, -61.56) * mm, "end": v(-98.04, -61.1) * mm});
            skLineSegment(sketch, "E331", {"start": v(-98.04, -61.1) * mm, "end": v(-95.72, -60.15) * mm});
            skLineSegment(sketch, "E332", {"start": v(-95.72, -60.15) * mm, "end": v(-93.08, -59.08) * mm});
            skLineSegment(sketch, "E333", {"start": v(-93.08, -59.08) * mm, "end": v(-91.76, -58.53) * mm});
            skLineSegment(sketch, "E334", {"start": v(-91.76, -58.53) * mm, "end": v(-89.12, -57.43) * mm});
            skLineSegment(sketch, "E335", {"start": v(-89.12, -57.43) * mm, "end": v(-84.78, -55.26) * mm});
            skLineSegment(sketch, "E336", {"start": v(-84.78, -55.26) * mm, "end": v(-82.6, -54.17) * mm});
            skLineSegment(sketch, "E337", {"start": v(-82.6, -54.17) * mm, "end": v(-78.26, -52) * mm});
            skLineSegment(sketch, "E338", {"start": v(-78.26, -52) * mm, "end": v(-74.6, -49.98) * mm});
            skLineSegment(sketch, "E339", {"start": v(-74.6, -49.98) * mm, "end": v(-72.81, -48.9) * mm});
            skLineSegment(sketch, "E340", {"start": v(-72.81, -48.9) * mm, "end": v(-69.34, -46.57) * mm});
            skLineSegment(sketch, "E341", {"start": v(-69.34, -46.57) * mm, "end": v(-67.37, -45.5) * mm});
            skLineSegment(sketch, "E342", {"start": v(-67.37, -45.5) * mm, "end": v(-66.42, -44.87) * mm});
            skLineSegment(sketch, "E343", {"start": v(-66.42, -44.87) * mm, "end": v(-64.68, -43.47) * mm});
            skLineSegment(sketch, "E344", {"start": v(-64.68, -43.47) * mm, "end": v(-63.68, -42.96) * mm});
            skLineSegment(sketch, "E345", {"start": v(-63.68, -42.96) * mm, "end": v(-63.2, -42.64) * mm});
            skLineSegment(sketch, "E346", {"start": v(-63.2, -42.64) * mm, "end": v(-62.35, -41.91) * mm});
            skLineSegment(sketch, "E347", {"start": v(-62.35, -41.91) * mm, "end": v(-56.7, -38.05) * mm});
            skLineSegment(sketch, "E348", {"start": v(-56.7, -38.05) * mm, "end": v(-54, -35.9) * mm});
            skLineSegment(sketch, "E349", {"start": v(-54, -35.9) * mm, "end": v(-48.97, -31.24) * mm});
            skLineSegment(sketch, "E350", {"start": v(-48.97, -31.24) * mm, "end": v(-48.53, -30.74) * mm});
            skLineSegment(sketch, "E351", {"start": v(-48.53, -30.74) * mm, "end": v(-48.23, -30.52) * mm});
            skLineSegment(sketch, "E352", {"start": v(-48.23, -30.52) * mm, "end": v(-47.6, -30.27) * mm});
            skLineSegment(sketch, "E353", {"start": v(-47.6, -30.27) * mm, "end": v(-42.88, -25.54) * mm});
            skLineSegment(sketch, "E354", {"start": v(-42.88, -25.54) * mm, "end": v(-40.5, -23.17) * mm});
            skLineSegment(sketch, "E355", {"start": v(-40.5, -23.17) * mm, "end": v(-35.78, -18.44) * mm});
            skLineSegment(sketch, "E356", {"start": v(-35.78, -18.44) * mm, "end": v(-32.3, -14.16) * mm});
            skLineSegment(sketch, "E357", {"start": v(-32.3, -14.16) * mm, "end": v(-30.56, -12.02) * mm});
            skLineSegment(sketch, "E358", {"start": v(-30.56, -12.02) * mm, "end": v(-27.05, -7.77) * mm});
            skLineSegment(sketch, "E359", {"start": v(-27.05, -7.77) * mm, "end": v(-26.25, -6.18) * mm});
            skLineSegment(sketch, "E360", {"start": v(-26.25, -6.18) * mm, "end": v(-25.72, -5.41) * mm});
            skLineSegment(sketch, "E361", {"start": v(-25.72, -5.41) * mm, "end": v(-24.53, -4.09) * mm});
            skLineSegment(sketch, "E362", {"start": v(-24.53, -4.09) * mm, "end": v(-24.02, -3.09) * mm});
            skLineSegment(sketch, "E363", {"start": v(-24.02, -3.09) * mm, "end": v(-23.7, -2.6) * mm});
            skLineSegment(sketch, "E364", {"start": v(-23.7, -2.6) * mm, "end": v(-22.97, -1.76) * mm});
            skLineSegment(sketch, "E365", {"start": v(-22.97, -1.76) * mm, "end": v(-20.15, 2.88) * mm});
            skLineSegment(sketch, "E366", {"start": v(-20.15, 2.88) * mm, "end": v(-18.75, 5.2) * mm});
            skLineSegment(sketch, "E367", {"start": v(-18.75, 5.2) * mm, "end": v(-15.99, 9.88) * mm});
            skLineSegment(sketch, "E368", {"start": v(-15.99, 9.88) * mm, "end": v(-15.06, 11.74) * mm});
            skLineSegment(sketch, "E369", {"start": v(-15.06, 11.74) * mm, "end": v(-14.6, 12.67) * mm});
            skLineSegment(sketch, "E370", {"start": v(-14.6, 12.67) * mm, "end": v(-13.66, 14.54) * mm});
            skLineSegment(sketch, "E371", {"start": v(-13.66, 14.54) * mm, "end": v(-13.6, 15.02) * mm});
            skLineSegment(sketch, "E372", {"start": v(-13.6, 15.02) * mm, "end": v(-13.51, 15.27) * mm});
            skLineSegment(sketch, "E373", {"start": v(-13.51, 15.27) * mm, "end": v(-13.27, 15.7) * mm});
            skLineSegment(sketch, "E374", {"start": v(-13.27, 15.7) * mm, "end": v(-13.97, 15.78) * mm});
            skLineSegment(sketch, "E375", {"start": v(-13.97, 15.78) * mm, "end": v(-14.32, 15.82) * mm});
            skLineSegment(sketch, "E376", {"start": v(-14.32, 15.82) * mm, "end": v(-15.02, 15.9) * mm});
            skLineSegment(sketch, "E377", {"start": v(-15.02, 15.9) * mm, "end": v(-17.81, 16.2) * mm});
            skLineSegment(sketch, "E378", {"start": v(-17.81, 16.2) * mm, "end": v(-19.2, 16.36) * mm});
            skLineSegment(sketch, "E379", {"start": v(-19.2, 16.36) * mm, "end": v(-22, 16.67) * mm});
            skLineSegment(sketch, "E380", {"start": v(-22, 16.67) * mm, "end": v(-22.7, 16.75) * mm});
            skLineSegment(sketch, "E381", {"start": v(-22.7, 16.75) * mm, "end": v(-23.05, 16.79) * mm});
            skLineSegment(sketch, "E382", {"start": v(-23.05, 16.79) * mm, "end": v(-23.75, 16.86) * mm});
            skLineSegment(sketch, "E383", {"start": v(-23.75, 16.86) * mm, "end": v(-24.76, 16.86) * mm});
            skLineSegment(sketch, "E384", {"start": v(-24.76, 16.86) * mm, "end": v(-25.26, 16.86) * mm});
            skLineSegment(sketch, "E385", {"start": v(-25.26, 16.86) * mm, "end": v(-26.27, 16.86) * mm});
            skLineSegment(sketch, "E386", {"start": v(-26.27, 16.86) * mm, "end": v(-26.73, 17.3) * mm});
            skLineSegment(sketch, "E387", {"start": v(-26.73, 17.3) * mm, "end": v(-27.28, 17.36) * mm});
            skLineSegment(sketch, "E388", {"start": v(-27.28, 17.36) * mm, "end": v(-27.82, 17.06) * mm});
            skLineSegment(sketch, "E389", {"start": v(-27.82, 17.06) * mm, "end": v(-29, 16.96) * mm});
            skLineSegment(sketch, "E390", {"start": v(-29, 16.96) * mm, "end": v(-29.66, 16.68) * mm});
            skLineSegment(sketch, "E391", {"start": v(-29.66, 16.68) * mm, "end": v(-30.54, 15.9) * mm});
            skLineSegment(sketch, "E392", {"start": v(-30.54, 15.9) * mm, "end": v(-33.8, 14.8) * mm});
            skLineSegment(sketch, "E393", {"start": v(-33.8, 14.8) * mm, "end": v(-35.43, 14.26) * mm});
            skLineSegment(sketch, "E394", {"start": v(-35.43, 14.26) * mm, "end": v(-38.69, 13.18) * mm});
            skLineSegment(sketch, "E395", {"start": v(-38.69, 13.18) * mm, "end": v(-42.72, 11.46) * mm});
            skLineSegment(sketch, "E396", {"start": v(-42.72, 11.46) * mm, "end": v(-44.73, 10.6) * mm});
            skLineSegment(sketch, "E397", {"start": v(-44.73, 10.6) * mm, "end": v(-48.77, 8.91) * mm});
            skLineSegment(sketch, "E398", {"start": v(-48.77, 8.91) * mm, "end": v(-51.57, 7.51) * mm});
            skLineSegment(sketch, "E399", {"start": v(-51.57, 7.51) * mm, "end": v(-52.96, 6.82) * mm});
            skLineSegment(sketch, "E400", {"start": v(-52.96, 6.82) * mm, "end": v(-55.76, 5.42) * mm});
            skLineSegment(sketch, "E401", {"start": v(-55.76, 5.42) * mm, "end": v(-57.94, 4.04) * mm});
            skLineSegment(sketch, "E402", {"start": v(-57.94, 4.04) * mm, "end": v(-59.03, 3.34) * mm});
            skLineSegment(sketch, "E403", {"start": v(-59.03, 3.34) * mm, "end": v(-61.19, 1.93) * mm});
            skLineSegment(sketch, "E404", {"start": v(-61.19, 1.93) * mm, "end": v(-64.87, -0.55) * mm});
            skLineSegment(sketch, "E405", {"start": v(-64.87, -0.55) * mm, "end": v(-66.66, -1.87) * mm});
            skLineSegment(sketch, "E406", {"start": v(-66.66, -1.87) * mm, "end": v(-70.11, -4.67) * mm});
            skLineSegment(sketch, "E407", {"start": v(-70.11, -4.67) * mm, "end": v(-73.3, -7.85) * mm});
            skLineSegment(sketch, "E408", {"start": v(-73.3, -7.85) * mm, "end": v(-74.88, -9.44) * mm});
            skLineSegment(sketch, "E409", {"start": v(-74.88, -9.44) * mm, "end": v(-78.07, -12.62) * mm});
            skLineSegment(sketch, "E410", {"start": v(-78.07, -12.62) * mm, "end": v(-83.4, -19.63) * mm});
            skLineSegment(sketch, "E411", {"start": v(-83.4, -19.63) * mm, "end": v(-86.25, -23.02) * mm});
            skLineSegment(sketch, "E412", {"start": v(-86.25, -23.02) * mm, "end": v(-92.23, -29.5) * mm});
            skLineSegment(sketch, "E413", {"start": v(-92.23, -29.5) * mm, "end": v(-92.53, -29.84) * mm});
            skLineSegment(sketch, "E414", {"start": v(-92.53, -29.84) * mm, "end": v(-92.65, -30.05) * mm});
            skLineSegment(sketch, "E415", {"start": v(-92.65, -30.05) * mm, "end": v(-92.8, -30.47) * mm});
            skLineSegment(sketch, "E416", {"start": v(-92.8, -30.47) * mm, "end": v(-99.1, -36.75) * mm});
            skLineSegment(sketch, "E417", {"start": v(-99.1, -36.75) * mm, "end": v(-102.24, -39.9) * mm});
            skLineSegment(sketch, "E418", {"start": v(-102.24, -39.9) * mm, "end": v(-108.52, -46.18) * mm});
            skLineSegment(sketch, "E419", {"start": v(-108.52, -46.18) * mm, "end": v(-112.26, -49.19) * mm});
            skLineSegment(sketch, "E420", {"start": v(-112.26, -49.19) * mm, "end": v(-114.12, -50.7) * mm});
            skLineSegment(sketch, "E421", {"start": v(-114.12, -50.7) * mm, "end": v(-117.83, -53.75) * mm});
            skLineSegment(sketch, "E422", {"start": v(-117.83, -53.75) * mm, "end": v(-118.35, -53.66) * mm});
            skLineSegment(sketch, "E423", {"start": v(-118.35, -53.66) * mm, "end": v(-118.76, -53.87) * mm});
            skLineSegment(sketch, "E424", {"start": v(-118.76, -53.87) * mm, "end": v(-119, -54.33) * mm});
            skLineSegment(sketch, "E425", {"start": v(-119, -54.33) * mm, "end": v(-121.4, -55.7) * mm});
            skLineSegment(sketch, "E426", {"start": v(-121.4, -55.7) * mm, "end": v(-122.56, -56.43) * mm});
            skLineSegment(sketch, "E427", {"start": v(-122.56, -56.43) * mm, "end": v(-124.82, -58.02) * mm});
            skLineSegment(sketch, "E428", {"start": v(-124.82, -58.02) * mm, "end": v(-127.35, -58.6) * mm});
            skLineSegment(sketch, "E429", {"start": v(-127.35, -58.6) * mm, "end": v(-128.6, -59) * mm});
            skLineSegment(sketch, "E430", {"start": v(-128.6, -59) * mm, "end": v(-131.02, -59.96) * mm});
            skLineSegment(sketch, "E431", {"start": v(-131.02, -59.96) * mm, "end": v(-133.28, -59.96) * mm});
            skLineSegment(sketch, "E432", {"start": v(-133.28, -59.96) * mm, "end": v(-134.4, -59.96) * mm});
            skLineSegment(sketch, "E433", {"start": v(-134.4, -59.96) * mm, "end": v(-136.65, -59.96) * mm});
            skLineSegment(sketch, "E434", {"start": v(-136.65, -59.96) * mm, "end": v(-137.04, -59.88) * mm});
            skLineSegment(sketch, "E435", {"start": v(-137.04, -59.88) * mm, "end": v(-137.23, -59.84) * mm});
            skLineSegment(sketch, "E436", {"start": v(-137.23, -59.84) * mm, "end": v(-137.62, -59.76) * mm});
            skLineSegment(sketch, "E437", {"start": v(-137.62, -59.76) * mm, "end": v(-139.17, -59.45) * mm});
            skLineSegment(sketch, "E438", {"start": v(-139.17, -59.45) * mm, "end": v(-139.95, -59.3) * mm});
            skLineSegment(sketch, "E439", {"start": v(-139.95, -59.3) * mm, "end": v(-141.5, -58.99) * mm});
            skLineSegment(sketch, "E440", {"start": v(-141.5, -58.99) * mm, "end": v(-144.18, -58.24) * mm});
            skLineSegment(sketch, "E441", {"start": v(-144.18, -58.24) * mm, "end": v(-145.5, -57.58) * mm});
            skLineSegment(sketch, "E442", {"start": v(-145.5, -57.58) * mm, "end": v(-147.7, -55.88) * mm});
            skLineSegment(sketch, "E443", {"start": v(-147.7, -55.88) * mm, "end": v(-149.59, -54.73) * mm});
            skLineSegment(sketch, "E444", {"start": v(-149.59, -54.73) * mm, "end": v(-150.48, -54) * mm});
            skLineSegment(sketch, "E445", {"start": v(-150.48, -54) * mm, "end": v(-151.98, -52.39) * mm});
            skLineSegment(sketch, "E446", {"start": v(-151.98, -52.39) * mm, "end": v(-153.88, -49.86) * mm});
            skLineSegment(sketch, "E447", {"start": v(-153.88, -49.86) * mm, "end": v(-154.71, -48.47) * mm});
            skLineSegment(sketch, "E448", {"start": v(-154.71, -48.47) * mm, "end": v(-156.05, -45.6) * mm});
            skLineSegment(sketch, "E449", {"start": v(-156.05, -45.6) * mm, "end": v(-156.49, -43.86) * mm});
            skLineSegment(sketch, "E450", {"start": v(-156.49, -43.86) * mm, "end": v(-156.76, -43) * mm});
            skLineSegment(sketch, "E451", {"start": v(-156.76, -43) * mm, "end": v(-157.4, -41.33) * mm});
            skLineSegment(sketch, "E452", {"start": v(-157.4, -41.33) * mm, "end": v(-157.4, -38.38) * mm});
            skLineSegment(sketch, "E453", {"start": v(-157.4, -38.38) * mm, "end": v(-157.4, -36.9) * mm});
            skLineSegment(sketch, "E454", {"start": v(-157.4, -36.9) * mm, "end": v(-157.4, -33.96) * mm});
            skLineSegment(sketch, "E455", {"start": v(-157.4, -33.96) * mm, "end": v(-156.65, -30.88) * mm});
            skLineSegment(sketch, "E456", {"start": v(-156.65, -30.88) * mm, "end": v(-156.04, -29.36) * mm});
            skLineSegment(sketch, "E457", {"start": v(-156.04, -29.36) * mm, "end": v(-154.5, -26.59) * mm});
            skLineSegment(sketch, "E458", {"start": v(-154.5, -26.59) * mm, "end": v(-152.85, -23.7) * mm});
            skLineSegment(sketch, "E459", {"start": v(-152.85, -23.7) * mm, "end": v(-151.8, -22.34) * mm});
            skLineSegment(sketch, "E460", {"start": v(-151.8, -22.34) * mm, "end": v(-149.45, -20) * mm});
            skLineSegment(sketch, "E461", {"start": v(-149.45, -20) * mm, "end": v(-145.05, -14.86) * mm});
            skLineSegment(sketch, "E462", {"start": v(-145.05, -14.86) * mm, "end": v(-142.84, -12.3) * mm});
            skLineSegment(sketch, "E463", {"start": v(-142.84, -12.3) * mm, "end": v(-138.4, -7.2) * mm});
            skLineSegment(sketch, "E464", {"start": v(-138.4, -7.2) * mm, "end": v(-137.51, -5.04) * mm});
            skLineSegment(sketch, "E465", {"start": v(-137.51, -5.04) * mm, "end": v(-136.9, -4) * mm});
            skLineSegment(sketch, "E466", {"start": v(-136.9, -4) * mm, "end": v(-135.49, -2.15) * mm});
            skLineSegment(sketch, "E467", {"start": v(-135.49, -2.15) * mm, "end": v(-133.42, 1.2) * mm});
            skLineSegment(sketch, "E468", {"start": v(-133.42, 1.2) * mm, "end": v(-132.19, 2.78) * mm});
            skLineSegment(sketch, "E469", {"start": v(-132.19, 2.78) * mm, "end": v(-129.47, 5.61) * mm});
            skLineSegment(sketch, "E470", {"start": v(-129.47, 5.61) * mm, "end": v(-128.93, 6.92) * mm});
            skLineSegment(sketch, "E471", {"start": v(-128.93, 6.92) * mm, "end": v(-128.8, 7.7) * mm});
            skLineSegment(sketch, "E472", {"start": v(-128.8, 7.7) * mm, "end": v(-128.9, 9.1) * mm});
            skLineSegment(sketch, "E473", {"start": v(-128.9, 9.1) * mm, "end": v(-129.32, 11.14) * mm});
            skLineSegment(sketch, "E474", {"start": v(-129.32, 11.14) * mm, "end": v(-129.85, 12.2) * mm});
            skLineSegment(sketch, "E475", {"start": v(-129.85, 12.2) * mm, "end": v(-131.22, 13.76) * mm});
            skLineSegment(sketch, "E476", {"start": v(-131.22, 13.76) * mm, "end": v(-132.48, 14.9) * mm});
            skLineSegment(sketch, "E477", {"start": v(-132.48, 14.9) * mm, "end": v(-133.28, 15.37) * mm});
            skLineSegment(sketch, "E478", {"start": v(-133.28, 15.37) * mm, "end": v(-134.9, 15.9) * mm});
            skLineSegment(sketch, "E479", {"start": v(-134.9, 15.9) * mm, "end": v(-136.13, 16.15) * mm});
            skLineSegment(sketch, "E480", {"start": v(-136.13, 16.15) * mm, "end": v(-136.78, 16.52) * mm});
            skLineSegment(sketch, "E481", {"start": v(-136.78, 16.52) * mm, "end": v(-137.62, 17.45) * mm});
            skLineSegment(sketch, "E482", {"start": v(-137.62, 17.45) * mm, "end": v(-138.02, 18.04) * mm});
            skLineSegment(sketch, "E483", {"start": v(-138.02, 18.04) * mm, "end": v(-138.26, 18.32) * mm});
            skLineSegment(sketch, "E484", {"start": v(-138.26, 18.32) * mm, "end": v(-138.78, 18.8) * mm});
            skLineSegment(sketch, "E485", {"start": v(-138.78, 18.8) * mm, "end": v(-138.95, 20.43) * mm});
            skLineSegment(sketch, "E486", {"start": v(-138.95, 20.43) * mm, "end": v(-138.87, 21.31) * mm});
            skLineSegment(sketch, "E487", {"start": v(-138.87, 21.31) * mm, "end": v(-138.4, 22.88) * mm});
            skLineSegment(sketch, "E488", {"start": v(-138.4, 22.88) * mm, "end": v(-137.53, 23.95) * mm});
            skLineSegment(sketch, "E489", {"start": v(-137.53, 23.95) * mm, "end": v(-136.93, 24.42) * mm});
            skLineSegment(sketch, "E490", {"start": v(-136.93, 24.42) * mm, "end": v(-135.68, 25.01) * mm});
            skLineSegment(sketch, "E491", {"start": v(-135.68, 25.01) * mm, "end": v(-136.15, 26.99) * mm});
            skLineSegment(sketch, "E492", {"start": v(-136.15, 26.99) * mm, "end": v(-136.27, 28.02) * mm});
            skLineSegment(sketch, "E493", {"start": v(-136.27, 28.02) * mm, "end": v(-136.26, 30.06) * mm});
            skLineSegment(sketch, "E494", {"start": v(-136.26, 30.06) * mm, "end": v(-136.17, 30.79) * mm});
            skLineSegment(sketch, "E495", {"start": v(-136.17, 30.79) * mm, "end": v(-136.05, 31.16) * mm});
            skLineSegment(sketch, "E496", {"start": v(-136.05, 31.16) * mm, "end": v(-135.68, 31.8) * mm});
            skLineSegment(sketch, "E497", {"start": v(-135.68, 31.8) * mm, "end": v(-135.2, 32.55) * mm});
            skLineSegment(sketch, "E498", {"start": v(-135.2, 32.55) * mm, "end": v(-134.93, 32.9) * mm});
            skLineSegment(sketch, "E499", {"start": v(-134.93, 32.9) * mm, "end": v(-134.32, 33.55) * mm});
            skLineSegment(sketch, "E500", {"start": v(-134.32, 33.55) * mm, "end": v(-133.9, 33.57) * mm});
            skLineSegment(sketch, "E501", {"start": v(-133.9, 33.57) * mm, "end": v(-133.67, 33.67) * mm});
            skLineSegment(sketch, "E502", {"start": v(-133.67, 33.67) * mm, "end": v(-133.35, 33.94) * mm});
            skLineSegment(sketch, "E503", {"start": v(-133.35, 33.94) * mm, "end": v(-133.68, 36.24) * mm});
            skLineSegment(sketch, "E504", {"start": v(-133.68, 36.24) * mm, "end": v(-133.71, 37.43) * mm});
            skLineSegment(sketch, "E505", {"start": v(-133.71, 37.43) * mm, "end": v(-133.55, 39.76) * mm});
            skLineSegment(sketch, "E506", {"start": v(-133.55, 39.76) * mm, "end": v(-133.15, 40.8) * mm});
            skLineSegment(sketch, "E507", {"start": v(-133.15, 40.8) * mm, "end": v(-132.8, 41.32) * mm});
            skLineSegment(sketch, "E508", {"start": v(-132.8, 41.32) * mm, "end": v(-132, 42.08) * mm});
            skLineSegment(sketch, "E509", {"start": v(-132, 42.08) * mm, "end": v(-131.58, 42.1) * mm});
            skLineSegment(sketch, "E510", {"start": v(-131.58, 42.1) * mm, "end": v(-131.35, 42.2) * mm});
            skLineSegment(sketch, "E511", {"start": v(-131.35, 42.2) * mm, "end": v(-131.02, 42.47) * mm});
            skLineSegment(sketch, "E512", {"start": v(-131.02, 42.47) * mm, "end": v(-130.93, 42.93) * mm});
            skLineSegment(sketch, "E513", {"start": v(-130.93, 42.93) * mm, "end": v(-130.89, 43.17) * mm});
            skLineSegment(sketch, "E514", {"start": v(-130.89, 43.17) * mm, "end": v(-130.83, 43.63) * mm});
            skLineSegment(sketch, "E515", {"start": v(-130.83, 43.63) * mm, "end": v(-131.06, 44.8) * mm});
            skLineSegment(sketch, "E516", {"start": v(-131.06, 44.8) * mm, "end": v(-131.18, 45.38) * mm});
            skLineSegment(sketch, "E517", {"start": v(-131.18, 45.38) * mm, "end": v(-131.41, 46.54) * mm});
            skLineSegment(sketch, "E518", {"start": v(-131.41, 46.54) * mm, "end": v(-131.26, 47.86) * mm});
            skLineSegment(sketch, "E519", {"start": v(-131.26, 47.86) * mm, "end": v(-131, 48.55) * mm});
            skLineSegment(sketch, "E520", {"start": v(-131, 48.55) * mm, "end": v(-130.25, 49.65) * mm});
            skLineSegment(sketch, "E521", {"start": v(-130.25, 49.65) * mm, "end": v(-129.2, 50.37) * mm});
            skLineSegment(sketch, "E522", {"start": v(-129.2, 50.37) * mm, "end": v(-128.74, 50.97) * mm});
            skLineSegment(sketch, "E523", {"start": v(-128.74, 50.97) * mm, "end": v(-128.3, 52.17) * mm});
            skLineSegment(sketch, "E524", {"start": v(-128.3, 52.17) * mm, "end": v(-129, 53.42) * mm});
            skLineSegment(sketch, "E525", {"start": v(-129, 53.42) * mm, "end": v(-129.18, 54.23) * mm});
            skLineSegment(sketch, "E526", {"start": v(-129.18, 54.23) * mm, "end": v(-129.09, 55.66) * mm});
            skLineSegment(sketch, "E527", {"start": v(-129.09, 55.66) * mm, "end": v(-128.45, 57.03) * mm});
            skLineSegment(sketch, "E528", {"start": v(-128.45, 57.03) * mm, "end": v(-128, 57.68) * mm});
            skLineSegment(sketch, "E529", {"start": v(-128, 57.68) * mm, "end": v(-126.95, 58.77) * mm});
            skLineSegment(sketch, "E530", {"start": v(-126.95, 58.77) * mm, "end": v(-126.72, 58.77) * mm});
            skLineSegment(sketch, "E531", {"start": v(-126.72, 58.77) * mm, "end": v(-126.6, 58.77) * mm});
            skLineSegment(sketch, "E532", {"start": v(-126.6, 58.77) * mm, "end": v(-126.37, 58.77) * mm});
            skLineSegment(sketch, "E533", {"start": v(-126.37, 58.77) * mm, "end": v(-126.61, 60.61) * mm});
            skLineSegment(sketch, "E534", {"start": v(-126.61, 60.61) * mm, "end": v(-126.65, 61.56) * mm});
            skLineSegment(sketch, "E535", {"start": v(-126.65, 61.56) * mm, "end": v(-126.56, 63.42) * mm});
            skLineSegment(sketch, "E536", {"start": v(-126.56, 63.42) * mm, "end": v(-126.33, 64.54) * mm});
            skLineSegment(sketch, "E537", {"start": v(-126.33, 64.54) * mm, "end": v(-126, 65.13) * mm});
            skLineSegment(sketch, "E538", {"start": v(-126, 65.13) * mm, "end": v(-125.2, 65.94) * mm});
            skLineSegment(sketch, "E539", {"start": v(-125.2, 65.94) * mm, "end": v(-124.74, 66.4) * mm});
            skLineSegment(sketch, "E540", {"start": v(-124.74, 66.4) * mm, "end": v(-124.5, 66.64) * mm});
            skLineSegment(sketch, "E541", {"start": v(-124.5, 66.64) * mm, "end": v(-124.04, 67.1) * mm});
            skLineSegment(sketch, "E542", {"start": v(-124.04, 67.1) * mm, "end": v(-124.5, 68.84) * mm});
            skLineSegment(sketch, "E543", {"start": v(-124.5, 68.84) * mm, "end": v(-124.54, 69.8) * mm});
            skLineSegment(sketch, "E544", {"start": v(-124.54, 69.8) * mm, "end": v(-124.24, 71.57) * mm});
            skLineSegment(sketch, "E545", {"start": v(-124.24, 71.57) * mm, "end": v(-123.68, 72.9) * mm});
            skLineSegment(sketch, "E546", {"start": v(-123.68, 72.9) * mm, "end": v(-123.2, 73.55) * mm});
            skLineSegment(sketch, "E547", {"start": v(-123.2, 73.55) * mm, "end": v(-122.1, 74.48) * mm});
            skLineSegment(sketch, "E548", {"start": v(-122.1, 74.48) * mm, "end": v(-122.18, 75.95) * mm});
            skLineSegment(sketch, "E549", {"start": v(-122.18, 75.95) * mm, "end": v(-122.21, 76.7) * mm});
            skLineSegment(sketch, "E550", {"start": v(-122.21, 76.7) * mm, "end": v(-122.3, 78.16) * mm});
            skLineSegment(sketch, "E551", {"start": v(-122.3, 78.16) * mm, "end": v(-122.04, 79.4) * mm});
            skLineSegment(sketch, "E552", {"start": v(-122.04, 79.4) * mm, "end": v(-121.67, 80.04) * mm});
            skLineSegment(sketch, "E553", {"start": v(-121.67, 80.04) * mm, "end": v(-120.74, 80.88) * mm});
            skLineSegment(sketch, "E554", {"start": v(-120.74, 80.88) * mm, "end": v(-120.36, 81.27) * mm});
            skLineSegment(sketch, "E555", {"start": v(-120.36, 81.27) * mm, "end": v(-120.16, 81.46) * mm});
            skLineSegment(sketch, "E556", {"start": v(-120.16, 81.46) * mm, "end": v(-119.77, 81.85) * mm});
            skLineSegment(sketch, "E557", {"start": v(-119.77, 81.85) * mm, "end": v(-120.32, 83.55) * mm});
            skLineSegment(sketch, "E558", {"start": v(-120.32, 83.55) * mm, "end": v(-120.37, 84.57) * mm});
            skLineSegment(sketch, "E559", {"start": v(-120.37, 84.57) * mm, "end": v(-119.97, 86.31) * mm});
            skLineSegment(sketch, "E560", {"start": v(-119.97, 86.31) * mm, "end": v(-119.3, 87.45) * mm});
            skLineSegment(sketch, "E561", {"start": v(-119.3, 87.45) * mm, "end": v(-118.84, 87.98) * mm});
            skLineSegment(sketch, "E562", {"start": v(-118.84, 87.98) * mm, "end": v(-117.83, 88.83) * mm});
            skLineSegment(sketch, "E563", {"start": v(-117.83, 88.83) * mm, "end": v(-118.34, 90.38) * mm});
            skLineSegment(sketch, "E564", {"start": v(-118.34, 90.38) * mm, "end": v(-118.39, 91.32) * mm});
            skLineSegment(sketch, "E565", {"start": v(-118.39, 91.32) * mm, "end": v(-118.03, 92.9) * mm});
            skLineSegment(sketch, "E566", {"start": v(-118.03, 92.9) * mm, "end": v(-117.12, 94.27) * mm});
            skLineSegment(sketch, "E567", {"start": v(-117.12, 94.27) * mm, "end": v(-116.69, 94.97) * mm});
            skLineSegment(sketch, "E568", {"start": v(-116.69, 94.97) * mm, "end": v(-115.9, 96.4) * mm});
            skLineSegment(sketch, "E569", {"start": v(-115.9, 96.4) * mm, "end": v(-116.53, 97.47) * mm});
            skLineSegment(sketch, "E570", {"start": v(-116.53, 97.47) * mm, "end": v(-116.58, 98.36) * mm});
            skLineSegment(sketch, "E571", {"start": v(-116.58, 98.36) * mm, "end": v(-116.09, 99.5) * mm});
            skLineSegment(sketch, "E572", {"start": v(-116.09, 99.5) * mm, "end": v(-115.65, 100.65) * mm});
            skLineSegment(sketch, "E573", {"start": v(-115.65, 100.65) * mm, "end": v(-115.26, 101.21) * mm});
            skLineSegment(sketch, "E574", {"start": v(-115.26, 101.21) * mm, "end": v(-114.34, 102.03) * mm});
            skLineSegment(sketch, "E575", {"start": v(-114.34, 102.03) * mm, "end": v(-114.34, 103.5) * mm});
            skLineSegment(sketch, "E576", {"start": v(-114.34, 103.5) * mm, "end": v(-114.34, 104.24) * mm});
            skLineSegment(sketch, "E577", {"start": v(-114.34, 104.24) * mm, "end": v(-114.34, 105.71) * mm});
            skLineSegment(sketch, "E578", {"start": v(-114.34, 105.71) * mm, "end": v(-113.85, 107.02) * mm});
            skLineSegment(sketch, "E579", {"start": v(-113.85, 107.02) * mm, "end": v(-113.42, 107.66) * mm});
            skLineSegment(sketch, "E580", {"start": v(-113.42, 107.66) * mm, "end": v(-112.4, 108.62) * mm});
            skLineSegment(sketch, "E581", {"start": v(-112.4, 108.62) * mm, "end": v(-112.53, 109.78) * mm});
            skLineSegment(sketch, "E582", {"start": v(-112.53, 109.78) * mm, "end": v(-112.57, 110.36) * mm});
            skLineSegment(sketch, "E583", {"start": v(-112.57, 110.36) * mm, "end": v(-112.6, 111.53) * mm});
            skLineSegment(sketch, "E584", {"start": v(-112.6, 111.53) * mm, "end": v(-112.34, 112.76) * mm});
            skLineSegment(sketch, "E585", {"start": v(-112.34, 112.76) * mm, "end": v(-111.97, 113.4) * mm});
            skLineSegment(sketch, "E586", {"start": v(-111.97, 113.4) * mm, "end": v(-111.04, 114.25) * mm});
            skLineSegment(sketch, "E587", {"start": v(-111.04, 114.25) * mm, "end": v(-110.7, 114.6) * mm});
            skLineSegment(sketch, "E588", {"start": v(-110.7, 114.6) * mm, "end": v(-110.6, 114.92) * mm});
            skLineSegment(sketch, "E589", {"start": v(-110.6, 114.92) * mm, "end": v(-110.66, 115.41) * mm});
            skLineSegment(sketch, "E590", {"start": v(-110.66, 115.41) * mm, "end": v(-111, 116.85) * mm});
            skLineSegment(sketch, "E591", {"start": v(-111, 116.85) * mm, "end": v(-110.95, 117.7) * mm});
            skLineSegment(sketch, "E592", {"start": v(-110.95, 117.7) * mm, "end": v(-110.46, 119.1) * mm});
            skLineSegment(sketch, "E593", {"start": v(-110.46, 119.1) * mm, "end": v(-109.84, 119.72) * mm});
            skLineSegment(sketch, "E594", {"start": v(-109.84, 119.72) * mm, "end": v(-109.53, 120.03) * mm});
            skLineSegment(sketch, "E595", {"start": v(-109.53, 120.03) * mm, "end": v(-108.91, 120.65) * mm});
            skLineSegment(sketch, "E596", {"start": v(-108.91, 120.65) * mm, "end": v(-109.06, 121.65) * mm});
            skLineSegment(sketch, "E597", {"start": v(-109.06, 121.65) * mm, "end": v(-109.1, 122.16) * mm});
            skLineSegment(sketch, "E598", {"start": v(-109.1, 122.16) * mm, "end": v(-109.1, 123.17) * mm});
            skLineSegment(sketch, "E599", {"start": v(-109.1, 123.17) * mm, "end": v(-108.95, 124.24) * mm});
            skLineSegment(sketch, "E600", {"start": v(-108.95, 124.24) * mm, "end": v(-108.74, 124.8) * mm});
            skLineSegment(sketch, "E601", {"start": v(-108.74, 124.8) * mm, "end": v(-108.13, 125.7) * mm});
            skLineSegment(sketch, "E602", {"start": v(-108.13, 125.7) * mm, "end": v(-107.82, 126) * mm});
            skLineSegment(sketch, "E603", {"start": v(-107.82, 126) * mm, "end": v(-107.67, 126.16) * mm});
            skLineSegment(sketch, "E604", {"start": v(-107.67, 126.16) * mm, "end": v(-107.36, 126.47) * mm});
            skLineSegment(sketch, "E605", {"start": v(-107.36, 126.47) * mm, "end": v(-107.36, 127.79) * mm});
            skLineSegment(sketch, "E606", {"start": v(-107.36, 127.79) * mm, "end": v(-107.36, 128.45) * mm});
            skLineSegment(sketch, "E607", {"start": v(-107.36, 128.45) * mm, "end": v(-107.36, 129.77) * mm});
            skLineSegment(sketch, "E608", {"start": v(-107.36, 129.77) * mm, "end": v(-106.86, 131.07) * mm});
            skLineSegment(sketch, "E609", {"start": v(-106.86, 131.07) * mm, "end": v(-106.44, 131.72) * mm});
            skLineSegment(sketch, "E610", {"start": v(-106.44, 131.72) * mm, "end": v(-105.42, 132.68) * mm});
            skLineSegment(sketch, "E611", {"start": v(-105.42, 132.68) * mm, "end": v(-105.84, 133.76) * mm});
            skLineSegment(sketch, "E612", {"start": v(-105.84, 133.76) * mm, "end": v(-105.88, 134.45) * mm});
            skLineSegment(sketch, "E613", {"start": v(-105.88, 134.45) * mm, "end": v(-105.61, 135.59) * mm});
            skLineSegment(sketch, "E614", {"start": v(-105.61, 135.59) * mm, "end": v(-105.17, 136.73) * mm});
            skLineSegment(sketch, "E615", {"start": v(-105.17, 136.73) * mm, "end": v(-104.78, 137.3) * mm});
            skLineSegment(sketch, "E616", {"start": v(-104.78, 137.3) * mm, "end": v(-103.87, 138.1) * mm});
            skLineSegment(sketch, "E617", {"start": v(-103.87, 138.1) * mm, "end": v(-103.87, 139.74) * mm});
            skLineSegment(sketch, "E618", {"start": v(-103.87, 139.74) * mm, "end": v(-103.87, 140.55) * mm});
            skLineSegment(sketch, "E619", {"start": v(-103.87, 140.55) * mm, "end": v(-103.87, 142.18) * mm});
            skLineSegment(sketch, "E620", {"start": v(-103.87, 142.18) * mm, "end": v(-103.1, 143.04) * mm});
            skLineSegment(sketch, "E621", {"start": v(-103.1, 143.04) * mm, "end": v(-102.7, 143.46) * mm});
            skLineSegment(sketch, "E622", {"start": v(-102.7, 143.46) * mm, "end": v(-101.93, 144.31) * mm});
            skLineSegment(sketch, "E623", {"start": v(-101.93, 144.31) * mm, "end": v(-102.3, 145.58) * mm});
            skLineSegment(sketch, "E624", {"start": v(-102.3, 145.58) * mm, "end": v(-102.34, 146.31) * mm});
            skLineSegment(sketch, "E625", {"start": v(-102.34, 146.31) * mm, "end": v(-102.12, 147.61) * mm});
            skLineSegment(sketch, "E626", {"start": v(-102.12, 147.61) * mm, "end": v(-101.8, 148.69) * mm});
            skLineSegment(sketch, "E627", {"start": v(-101.8, 148.69) * mm, "end": v(-101.44, 149.24) * mm});
            skLineSegment(sketch, "E628", {"start": v(-101.44, 149.24) * mm, "end": v(-100.57, 149.94) * mm});
            skLineSegment(sketch, "E629", {"start": v(-100.57, 149.94) * mm, "end": v(-99.97, 150.34) * mm});
            skLineSegment(sketch, "E630", {"start": v(-99.97, 150.34) * mm, "end": v(-99.7, 150.58) * mm});
            skLineSegment(sketch, "E631", {"start": v(-99.7, 150.58) * mm, "end": v(-99.21, 151.1) * mm});
            skLineSegment(sketch, "E632", {"start": v(-99.21, 151.1) * mm, "end": v(-96.88, 151.1) * mm});
            skLineSegment(sketch, "E633", {"start": v(-96.88, 151.1) * mm, "end": v(-95.72, 151.1) * mm});
            skLineSegment(sketch, "E634", {"start": v(-95.72, 151.1) * mm, "end": v(-93.4, 151.1) * mm});
            skLineSegment(sketch, "E635", {"start": v(-93.4, 151.1) * mm, "end": v(-92.93, 151.41) * mm});
            skLineSegment(sketch, "E636", {"start": v(-92.93, 151.41) * mm, "end": v(-92.7, 151.57) * mm});
            skLineSegment(sketch, "E637", {"start": v(-92.7, 151.57) * mm, "end": v(-92.23, 151.88) * mm});
            skLineSegment(sketch, "E638", {"start": v(-92.23, 151.88) * mm, "end": v(-90.97, 151.97) * mm});
            skLineSegment(sketch, "E639", {"start": v(-90.97, 151.97) * mm, "end": v(-90.27, 151.84) * mm});
            skLineSegment(sketch, "E640", {"start": v(-90.27, 151.84) * mm, "end": v(-89.12, 151.3) * mm});
            skLineSegment(sketch, "E641", {"start": v(-89.12, 151.3) * mm, "end": v(-88.08, 150.9) * mm});
            skLineSegment(sketch, "E642", {"start": v(-88.08, 150.9) * mm, "end": v(-87.56, 150.56) * mm});
            skLineSegment(sketch, "E643", {"start": v(-87.56, 150.56) * mm, "end": v(-86.8, 149.75) * mm});
            skLineSegment(sketch, "E644", {"start": v(-86.8, 149.75) * mm, "end": v(-86.83, 149.3) * mm});
            skLineSegment(sketch, "E645", {"start": v(-86.83, 149.3) * mm, "end": v(-86.63, 148.96) * mm});
            skLineSegment(sketch, "E646", {"start": v(-86.63, 148.96) * mm, "end": v(-86.21, 148.78) * mm});
            skLineSegment(sketch, "E647", {"start": v(-86.21, 148.78) * mm, "end": v(-84.66, 145.67) * mm});
            skLineSegment(sketch, "E648", {"start": v(-84.66, 145.67) * mm, "end": v(-83.89, 144.12) * mm});
            skLineSegment(sketch, "E649", {"start": v(-83.89, 144.12) * mm, "end": v(-82.33, 141.02) * mm});
            skLineSegment(sketch, "E650", {"start": v(-82.33, 141.02) * mm, "end": v(-82.18, 140.86) * mm});
            skLineSegment(sketch, "E651", {"start": v(-82.18, 140.86) * mm, "end": v(-82.1, 140.78) * mm});
            skLineSegment(sketch, "E652", {"start": v(-82.1, 140.78) * mm, "end": v(-81.95, 140.63) * mm});
            skLineSegment(sketch, "E653", {"start": v(-81.95, 140.63) * mm, "end": v(-81.01, 138.77) * mm});
            skLineSegment(sketch, "E654", {"start": v(-81.01, 138.77) * mm, "end": v(-80.55, 137.84) * mm});
            skLineSegment(sketch, "E655", {"start": v(-80.55, 137.84) * mm, "end": v(-79.62, 135.97) * mm});
            skLineSegment(sketch, "E656", {"start": v(-79.62, 135.97) * mm, "end": v(-72.58, 123.8) * mm});
            skLineSegment(sketch, "E657", {"start": v(-72.58, 123.8) * mm, "end": v(-69.01, 117.75) * mm});
            skLineSegment(sketch, "E658", {"start": v(-69.01, 117.75) * mm, "end": v(-61.77, 105.71) * mm});
            skLineSegment(sketch, "E659", {"start": v(-61.77, 105.71) * mm, "end": v(-60.81, 103.93) * mm});
            skLineSegment(sketch, "E660", {"start": v(-60.81, 103.93) * mm, "end": v(-60.26, 103.07) * mm});
            skLineSegment(sketch, "E661", {"start": v(-60.26, 103.07) * mm, "end": v(-59.06, 101.44) * mm});
            skLineSegment(sketch, "E662", {"start": v(-59.06, 101.44) * mm, "end": v(-58.1, 99.66) * mm});
            skLineSegment(sketch, "E663", {"start": v(-58.1, 99.66) * mm, "end": v(-57.55, 98.8) * mm});
            skLineSegment(sketch, "E664", {"start": v(-57.55, 98.8) * mm, "end": v(-56.34, 97.18) * mm});
            skLineSegment(sketch, "E665", {"start": v(-56.34, 97.18) * mm, "end": v(-55.83, 96.18) * mm});
            skLineSegment(sketch, "E666", {"start": v(-55.83, 96.18) * mm, "end": v(-55.51, 95.7) * mm});
            skLineSegment(sketch, "E667", {"start": v(-55.51, 95.7) * mm, "end": v(-54.79, 94.85) * mm});
            skLineSegment(sketch, "E668", {"start": v(-54.79, 94.85) * mm, "end": v(-54.28, 93.85) * mm});
            skLineSegment(sketch, "E669", {"start": v(-54.28, 93.85) * mm, "end": v(-53.96, 93.37) * mm});
            skLineSegment(sketch, "E670", {"start": v(-53.96, 93.37) * mm, "end": v(-53.24, 92.52) * mm});
            skLineSegment(sketch, "E671", {"start": v(-53.24, 92.52) * mm, "end": v(-52.73, 91.52) * mm});
            skLineSegment(sketch, "E672", {"start": v(-52.73, 91.52) * mm, "end": v(-52.41, 91.04) * mm});
            skLineSegment(sketch, "E673", {"start": v(-52.41, 91.04) * mm, "end": v(-51.68, 90.2) * mm});
            skLineSegment(sketch, "E674", {"start": v(-51.68, 90.2) * mm, "end": v(-51.18, 89.2) * mm});
            skLineSegment(sketch, "E675", {"start": v(-51.18, 89.2) * mm, "end": v(-50.86, 88.72) * mm});
            skLineSegment(sketch, "E676", {"start": v(-50.86, 88.72) * mm, "end": v(-50.13, 87.86) * mm});
            skLineSegment(sketch, "E677", {"start": v(-50.13, 87.86) * mm, "end": v(-49.63, 86.87) * mm});
            skLineSegment(sketch, "E678", {"start": v(-49.63, 86.87) * mm, "end": v(-49.3, 86.39) * mm});
            skLineSegment(sketch, "E679", {"start": v(-49.3, 86.39) * mm, "end": v(-48.58, 85.54) * mm});
            skLineSegment(sketch, "E680", {"start": v(-48.58, 85.54) * mm, "end": v(-48.07, 84.54) * mm});
            skLineSegment(sketch, "E681", {"start": v(-48.07, 84.54) * mm, "end": v(-47.75, 84.06) * mm});
            skLineSegment(sketch, "E682", {"start": v(-47.75, 84.06) * mm, "end": v(-47.03, 83.2) * mm});
            skLineSegment(sketch, "E683", {"start": v(-47.03, 83.2) * mm, "end": v(-46.42, 81.97) * mm});
            skLineSegment(sketch, "E684", {"start": v(-46.42, 81.97) * mm, "end": v(-45.95, 81.38) * mm});
            skLineSegment(sketch, "E685", {"start": v(-45.95, 81.38) * mm, "end": v(-44.9, 80.5) * mm});
            skLineSegment(sketch, "E686", {"start": v(-44.9, 80.5) * mm, "end": v(-44.98, 79.98) * mm});
            skLineSegment(sketch, "E687", {"start": v(-44.98, 79.98) * mm, "end": v(-44.78, 79.57) * mm});
            skLineSegment(sketch, "E688", {"start": v(-44.78, 79.57) * mm, "end": v(-44.31, 79.33) * mm});
            skLineSegment(sketch, "E689", {"start": v(-44.31, 79.33) * mm, "end": v(-42.01, 76.05) * mm});
            skLineSegment(sketch, "E690", {"start": v(-42.01, 76.05) * mm, "end": v(-40.85, 74.42) * mm});
            skLineSegment(sketch, "E691", {"start": v(-40.85, 74.42) * mm, "end": v(-38.5, 71.18) * mm});
            skLineSegment(sketch, "E692", {"start": v(-38.5, 71.18) * mm, "end": v(-34.26, 65.09) * mm});
            skLineSegment(sketch, "E693", {"start": v(-34.26, 65.09) * mm, "end": v(-32, 62.12) * mm});
            skLineSegment(sketch, "E694", {"start": v(-32, 62.12) * mm, "end": v(-27.24, 56.44) * mm});
            skLineSegment(sketch, "E695", {"start": v(-27.24, 56.44) * mm, "end": v(-26.59, 56.05) * mm});
            skLineSegment(sketch, "E696", {"start": v(-26.59, 56.05) * mm, "end": v(-26.23, 55.89) * mm});
            skLineSegment(sketch, "E697", {"start": v(-26.23, 55.89) * mm, "end": v(-25.5, 55.66) * mm});
            skLineSegment(sketch, "E698", {"start": v(-25.5, 55.66) * mm, "end": v(-25.5, 55.35) * mm});
            skLineSegment(sketch, "E699", {"start": v(-25.5, 55.35) * mm, "end": v(-25.5, 55.2) * mm});
            skLineSegment(sketch, "E700", {"start": v(-25.5, 55.2) * mm, "end": v(-25.5, 54.89) * mm});
            skLineSegment(sketch, "E701", {"start": v(-25.5, 54.89) * mm, "end": v(-24.98, 54.98) * mm});
            skLineSegment(sketch, "E702", {"start": v(-24.98, 54.98) * mm, "end": v(-24.57, 54.77) * mm});
            skLineSegment(sketch, "E703", {"start": v(-24.57, 54.77) * mm, "end": v(-24.33, 54.3) * mm});
            skLineSegment(sketch, "E704", {"start": v(-24.33, 54.3) * mm, "end": v(-22.67, 53.13) * mm});
            skLineSegment(sketch, "E705", {"start": v(-22.67, 53.13) * mm, "end": v(-21.88, 52.46) * mm});
            skLineSegment(sketch, "E706", {"start": v(-21.88, 52.46) * mm, "end": v(-20.45, 51) * mm});
            skLineSegment(sketch, "E707", {"start": v(-20.45, 51) * mm, "end": v(-15.61, 49.7) * mm});
            skLineSegment(sketch, "E708", {"start": v(-15.61, 49.7) * mm, "end": v(-13.16, 49.16) * mm});
            skLineSegment(sketch, "E709", {"start": v(-13.16, 49.16) * mm, "end": v(-8.23, 48.3) * mm});
            skLineSegment(sketch, "E710", {"start": v(-8.23, 48.3) * mm, "end": v(-8.98, 50.83) * mm});
            skLineSegment(sketch, "E711", {"start": v(-8.98, 50.83) * mm, "end": v(-9.45, 52.09) * mm});
            skLineSegment(sketch, "E712", {"start": v(-9.45, 52.09) * mm, "end": v(-10.56, 54.5) * mm});
            skLineSegment(sketch, "E713", {"start": v(-10.56, 54.5) * mm, "end": v(-12.55, 59.32) * mm});
            skLineSegment(sketch, "E714", {"start": v(-12.55, 59.32) * mm, "end": v(-13.56, 61.72) * mm});
            skLineSegment(sketch, "E715", {"start": v(-13.56, 61.72) * mm, "end": v(-15.6, 66.53) * mm});
            skLineSegment(sketch, "E716", {"start": v(-15.6, 66.53) * mm, "end": v(-16.38, 68.08) * mm});
            skLineSegment(sketch, "E717", {"start": v(-16.38, 68.08) * mm, "end": v(-16.77, 68.85) * mm});
            skLineSegment(sketch, "E718", {"start": v(-16.77, 68.85) * mm, "end": v(-17.54, 70.4) * mm});
            skLineSegment(sketch, "E719", {"start": v(-17.54, 70.4) * mm, "end": v(-17.7, 70.87) * mm});
            skLineSegment(sketch, "E720", {"start": v(-17.7, 70.87) * mm, "end": v(-17.77, 71.1) * mm});
            skLineSegment(sketch, "E721", {"start": v(-17.77, 71.1) * mm, "end": v(-17.93, 71.57) * mm});
            skLineSegment(sketch, "E722", {"start": v(-17.93, 71.57) * mm, "end": v(-20.57, 76.85) * mm});
            skLineSegment(sketch, "E723", {"start": v(-20.57, 76.85) * mm, "end": v(-21.89, 79.48) * mm});
            skLineSegment(sketch, "E724", {"start": v(-21.89, 79.48) * mm, "end": v(-24.53, 84.76) * mm});
            skLineSegment(sketch, "E725", {"start": v(-24.53, 84.76) * mm, "end": v(-24.68, 84.92) * mm});
            skLineSegment(sketch, "E726", {"start": v(-24.68, 84.92) * mm, "end": v(-24.76, 85) * mm});
            skLineSegment(sketch, "E727", {"start": v(-24.76, 85) * mm, "end": v(-24.91, 85.15) * mm});
            skLineSegment(sketch, "E728", {"start": v(-24.91, 85.15) * mm, "end": v(-25.69, 86.7) * mm});
            skLineSegment(sketch, "E729", {"start": v(-25.69, 86.7) * mm, "end": v(-26.08, 87.48) * mm});
            skLineSegment(sketch, "E730", {"start": v(-26.08, 87.48) * mm, "end": v(-26.85, 89.03) * mm});
            skLineSegment(sketch, "E731", {"start": v(-26.85, 89.03) * mm, "end": v(-30.98, 96.05) * mm});
            skLineSegment(sketch, "E732", {"start": v(-30.98, 96.05) * mm, "end": v(-33.08, 99.54) * mm});
            skLineSegment(sketch, "E733", {"start": v(-33.08, 99.54) * mm, "end": v(-37.33, 106.49) * mm});
            skLineSegment(sketch, "E734", {"start": v(-37.33, 106.49) * mm, "end": v(-37.83, 107.49) * mm});
            skLineSegment(sketch, "E735", {"start": v(-37.83, 107.49) * mm, "end": v(-38.15, 107.96) * mm});
            skLineSegment(sketch, "E736", {"start": v(-38.15, 107.96) * mm, "end": v(-38.88, 108.81) * mm});
            skLineSegment(sketch, "E737", {"start": v(-38.88, 108.81) * mm, "end": v(-39.39, 109.81) * mm});
            skLineSegment(sketch, "E738", {"start": v(-39.39, 109.81) * mm, "end": v(-39.7, 110.3) * mm});
            skLineSegment(sketch, "E739", {"start": v(-39.7, 110.3) * mm, "end": v(-40.43, 111.14) * mm});
            skLineSegment(sketch, "E740", {"start": v(-40.43, 111.14) * mm, "end": v(-40.94, 112.14) * mm});
            skLineSegment(sketch, "E741", {"start": v(-40.94, 112.14) * mm, "end": v(-41.26, 112.62) * mm});
            skLineSegment(sketch, "E742", {"start": v(-41.26, 112.62) * mm, "end": v(-41.98, 113.47) * mm});
            skLineSegment(sketch, "E743", {"start": v(-41.98, 113.47) * mm, "end": v(-42.5, 114.47) * mm});
            skLineSegment(sketch, "E744", {"start": v(-42.5, 114.47) * mm, "end": v(-42.8, 114.95) * mm});
            skLineSegment(sketch, "E745", {"start": v(-42.8, 114.95) * mm, "end": v(-43.54, 115.8) * mm});
            skLineSegment(sketch, "E746", {"start": v(-43.54, 115.8) * mm, "end": v(-44.04, 116.8) * mm});
            skLineSegment(sketch, "E747", {"start": v(-44.04, 116.8) * mm, "end": v(-44.36, 117.28) * mm});
            skLineSegment(sketch, "E748", {"start": v(-44.36, 117.28) * mm, "end": v(-45.09, 118.13) * mm});
            skLineSegment(sketch, "E749", {"start": v(-45.09, 118.13) * mm, "end": v(-50.18, 125.51) * mm});
            skLineSegment(sketch, "E750", {"start": v(-50.18, 125.51) * mm, "end": v(-52.9, 129.1) * mm});
            skLineSegment(sketch, "E751", {"start": v(-52.9, 129.1) * mm, "end": v(-58.67, 135.97) * mm});
            skLineSegment(sketch, "E752", {"start": v(-58.67, 135.97) * mm, "end": v(-63.12, 141.85) * mm});
            skLineSegment(sketch, "E753", {"start": v(-63.12, 141.85) * mm, "end": v(-65.55, 144.66) * mm});
            skLineSegment(sketch, "E754", {"start": v(-65.55, 144.66) * mm, "end": v(-70.7, 149.94) * mm});
            skLineSegment(sketch, "E755", {"start": v(-70.7, 149.94) * mm, "end": v(-70.85, 150.25) * mm});
            skLineSegment(sketch, "E756", {"start": v(-70.85, 150.25) * mm, "end": v(-70.93, 150.4) * mm});
            skLineSegment(sketch, "E757", {"start": v(-70.93, 150.4) * mm, "end": v(-71.08, 150.72) * mm});
            skLineSegment(sketch, "E758", {"start": v(-71.08, 150.72) * mm, "end": v(-73.41, 153.04) * mm});
            skLineSegment(sketch, "E759", {"start": v(-73.41, 153.04) * mm, "end": v(-74.57, 154.2) * mm});
            skLineSegment(sketch, "E760", {"start": v(-74.57, 154.2) * mm, "end": v(-76.9, 156.54) * mm});
            skLineSegment(sketch, "E761", {"start": v(-76.9, 156.54) * mm, "end": v(-77.06, 156.85) * mm});
            skLineSegment(sketch, "E762", {"start": v(-77.06, 156.85) * mm, "end": v(-77.13, 157) * mm});
            skLineSegment(sketch, "E763", {"start": v(-77.13, 157) * mm, "end": v(-77.3, 157.31) * mm});
            skLineSegment(sketch, "E764", {"start": v(-77.3, 157.31) * mm, "end": v(-80.16, 160.18) * mm});
            skLineSegment(sketch, "E765", {"start": v(-80.16, 160.18) * mm, "end": v(-81.6, 161.62) * mm});
            skLineSegment(sketch, "E766", {"start": v(-81.6, 161.62) * mm, "end": v(-84.47, 164.49) * mm});
            skLineSegment(sketch, "E767", {"start": v(-84.47, 164.49) * mm, "end": v(-84.78, 164.64) * mm});
            skLineSegment(sketch, "E768", {"start": v(-84.78, 164.64) * mm, "end": v(-84.93, 164.72) * mm});
            skLineSegment(sketch, "E769", {"start": v(-84.93, 164.72) * mm, "end": v(-85.24, 164.88) * mm});
            skLineSegment(sketch, "E770", {"start": v(-85.24, 164.88) * mm, "end": v(-87.42, 167.05) * mm});
            skLineSegment(sketch, "E771", {"start": v(-87.42, 167.05) * mm, "end": v(-88.5, 168.14) * mm});
            skLineSegment(sketch, "E772", {"start": v(-88.5, 168.14) * mm, "end": v(-90.68, 170.3) * mm});
            skLineSegment(sketch, "E773", {"start": v(-90.68, 170.3) * mm, "end": v(-93.57, 172.6) * mm});
            skLineSegment(sketch, "E774", {"start": v(-93.57, 172.6) * mm, "end": v(-94.97, 173.8) * mm});
            skLineSegment(sketch, "E775", {"start": v(-94.97, 173.8) * mm, "end": v(-97.66, 176.32) * mm});
            skLineSegment(sketch, "E776", {"start": v(-97.66, 176.32) * mm, "end": v(-99.11, 176.55) * mm});
            skLineSegment(sketch, "E777", {"start": v(-99.11, 176.55) * mm, "end": v(-99.85, 176.8) * mm});
            skLineSegment(sketch, "E778", {"start": v(-99.85, 176.8) * mm, "end": v(-101.15, 177.49) * mm});
            skLineSegment(sketch, "E779", {"start": v(-101.15, 177.49) * mm, "end": v(-102.7, 177.49) * mm});
            skLineSegment(sketch, "E780", {"start": v(-102.7, 177.49) * mm, "end": v(-103.48, 177.49) * mm});
            skLineSegment(sketch, "E781", {"start": v(-103.48, 177.49) * mm, "end": v(-105.03, 177.49) * mm});
            skLineSegment(sketch, "E782", {"start": v(-105.03, 177.49) * mm, "end": v(-107.44, 176.6) * mm});
            skLineSegment(sketch, "E783", {"start": v(-107.44, 176.6) * mm, "end": v(-108.62, 175.95) * mm});
            skLineSegment(sketch, "E784", {"start": v(-108.62, 175.95) * mm, "end": v(-110.66, 174.38) * mm});
            skLineSegment(sketch, "E785", {"start": v(-110.66, 174.38) * mm, "end": v(-112.06, 172.64) * mm});
            skLineSegment(sketch, "E786", {"start": v(-112.06, 172.64) * mm, "end": v(-112.69, 171.7) * mm});
            skLineSegment(sketch, "E787", {"start": v(-112.69, 171.7) * mm, "end": v(-113.76, 169.73) * mm});
            skLineSegment(sketch, "E788", {"start": v(-113.76, 169.73) * mm, "end": v(-114.54, 168.18) * mm});
            skLineSegment(sketch, "E789", {"start": v(-114.54, 168.18) * mm, "end": v(-114.92, 167.4) * mm});
            skLineSegment(sketch, "E790", {"start": v(-114.92, 167.4) * mm, "end": v(-115.7, 165.85) * mm});
            skLineSegment(sketch, "E791", {"start": v(-115.7, 165.85) * mm, "end": v(-115.86, 165.7) * mm});
            skLineSegment(sketch, "E792", {"start": v(-115.86, 165.7) * mm, "end": v(-115.93, 165.61) * mm});
            skLineSegment(sketch, "E793", {"start": v(-115.93, 165.61) * mm, "end": v(-116.09, 165.46) * mm});
            skLineSegment(sketch, "E794", {"start": v(-116.09, 165.46) * mm, "end": v(-116.86, 163.9) * mm});
            skLineSegment(sketch, "E795", {"start": v(-116.86, 163.9) * mm, "end": v(-117.25, 163.13) * mm});
            skLineSegment(sketch, "E796", {"start": v(-117.25, 163.13) * mm, "end": v(-118.03, 161.58) * mm});
            skLineSegment(sketch, "E797", {"start": v(-118.03, 161.58) * mm, "end": v(-118.18, 161.42) * mm});
            skLineSegment(sketch, "E798", {"start": v(-118.18, 161.42) * mm, "end": v(-118.26, 161.35) * mm});
            skLineSegment(sketch, "E799", {"start": v(-118.26, 161.35) * mm, "end": v(-118.42, 161.2) * mm});
            skLineSegment(sketch, "E800", {"start": v(-118.42, 161.2) * mm, "end": v(-119.5, 159.02) * mm});
            skLineSegment(sketch, "E801", {"start": v(-119.5, 159.02) * mm, "end": v(-120.05, 157.93) * mm});
            skLineSegment(sketch, "E802", {"start": v(-120.05, 157.93) * mm, "end": v(-121.13, 155.76) * mm});
            skLineSegment(sketch, "E803", {"start": v(-121.13, 155.76) * mm, "end": v(-121.29, 155.6) * mm});
            skLineSegment(sketch, "E804", {"start": v(-121.29, 155.6) * mm, "end": v(-121.36, 155.53) * mm});
            skLineSegment(sketch, "E805", {"start": v(-121.36, 155.53) * mm, "end": v(-121.52, 155.37) * mm});
            skLineSegment(sketch, "E806", {"start": v(-121.52, 155.37) * mm, "end": v(-123.07, 152.27) * mm});
            skLineSegment(sketch, "E807", {"start": v(-123.07, 152.27) * mm, "end": v(-123.85, 150.72) * mm});
            skLineSegment(sketch, "E808", {"start": v(-123.85, 150.72) * mm, "end": v(-125.4, 147.61) * mm});
            skLineSegment(sketch, "E809", {"start": v(-125.4, 147.61) * mm, "end": v(-125.55, 147.46) * mm});
            skLineSegment(sketch, "E810", {"start": v(-125.55, 147.46) * mm, "end": v(-125.63, 147.38) * mm});
            skLineSegment(sketch, "E811", {"start": v(-125.63, 147.38) * mm, "end": v(-125.79, 147.22) * mm});
            skLineSegment(sketch, "E812", {"start": v(-125.79, 147.22) * mm, "end": v(-130.29, 138.22) * mm});
            skLineSegment(sketch, "E813", {"start": v(-130.29, 138.22) * mm, "end": v(-132.54, 133.72) * mm});
            skLineSegment(sketch, "E814", {"start": v(-132.54, 133.72) * mm, "end": v(-137.04, 124.72) * mm});
            skLineSegment(sketch, "E815", {"start": v(-137.04, 124.72) * mm, "end": v(-137.2, 124.26) * mm});
            skLineSegment(sketch, "E816", {"start": v(-137.2, 124.26) * mm, "end": v(-137.27, 124.02) * mm});
            skLineSegment(sketch, "E817", {"start": v(-137.27, 124.02) * mm, "end": v(-137.43, 123.56) * mm});
            skLineSegment(sketch, "E818", {"start": v(-137.43, 123.56) * mm, "end": v(-138.82, 120.76) * mm});
            skLineSegment(sketch, "E819", {"start": v(-138.82, 120.76) * mm, "end": v(-139.52, 119.37) * mm});
            skLineSegment(sketch, "E820", {"start": v(-139.52, 119.37) * mm, "end": v(-140.92, 116.57) * mm});
            skLineSegment(sketch, "E821", {"start": v(-140.92, 116.57) * mm, "end": v(-141.07, 116.1) * mm});
            skLineSegment(sketch, "E822", {"start": v(-141.07, 116.1) * mm, "end": v(-141.15, 115.88) * mm});
            skLineSegment(sketch, "E823", {"start": v(-141.15, 115.88) * mm, "end": v(-141.3, 115.41) * mm});
            skLineSegment(sketch, "E824", {"start": v(-141.3, 115.41) * mm, "end": v(-142.24, 113.55) * mm});
            skLineSegment(sketch, "E825", {"start": v(-142.24, 113.55) * mm, "end": v(-142.7, 112.62) * mm});
            skLineSegment(sketch, "E826", {"start": v(-142.7, 112.62) * mm, "end": v(-143.63, 110.75) * mm});
            skLineSegment(sketch, "E827", {"start": v(-143.63, 110.75) * mm, "end": v(-143.79, 110.29) * mm});
            skLineSegment(sketch, "E828", {"start": v(-143.79, 110.29) * mm, "end": v(-143.87, 110.06) * mm});
            skLineSegment(sketch, "E829", {"start": v(-143.87, 110.06) * mm, "end": v(-144.02, 109.6) * mm});
            skLineSegment(sketch, "E830", {"start": v(-144.02, 109.6) * mm, "end": v(-144.8, 108.04) * mm});
            skLineSegment(sketch, "E831", {"start": v(-144.8, 108.04) * mm, "end": v(-145.19, 107.26) * mm});
            skLineSegment(sketch, "E832", {"start": v(-145.19, 107.26) * mm, "end": v(-145.96, 105.71) * mm});
            skLineSegment(sketch, "E833", {"start": v(-145.96, 105.71) * mm, "end": v(-150.16, 96.1) * mm});
            skLineSegment(sketch, "E834", {"start": v(-150.16, 96.1) * mm, "end": v(-152.25, 91.28) * mm});
            skLineSegment(sketch, "E835", {"start": v(-152.25, 91.28) * mm, "end": v(-156.44, 81.66) * mm});
            skLineSegment(sketch, "E836", {"start": v(-156.44, 81.66) * mm, "end": v(-158.38, 76.63) * mm});
            skLineSegment(sketch, "E837", {"start": v(-158.38, 76.63) * mm, "end": v(-159.42, 74.14) * mm});
            skLineSegment(sketch, "E838", {"start": v(-159.42, 74.14) * mm, "end": v(-161.68, 69.24) * mm});
            skLineSegment(sketch, "E839", {"start": v(-161.68, 69.24) * mm, "end": v(-162.8, 65.56) * mm});
            skLineSegment(sketch, "E840", {"start": v(-162.8, 65.56) * mm, "end": v(-163.43, 63.73) * mm});
            skLineSegment(sketch, "E841", {"start": v(-163.43, 63.73) * mm, "end": v(-164.78, 60.12) * mm});
            skLineSegment(sketch, "E842", {"start": v(-164.78, 60.12) * mm, "end": v(-167.08, 53.54) * mm});
            skLineSegment(sketch, "E843", {"start": v(-167.08, 53.54) * mm, "end": v(-168.2, 50.25) * mm});
            skLineSegment(sketch, "E844", {"start": v(-168.2, 50.25) * mm, "end": v(-170.4, 43.63) * mm});
            skLineSegment(sketch, "E845", {"start": v(-170.4, 43.63) * mm, "end": v(-170.97, 40.92) * mm});
            skLineSegment(sketch, "E846", {"start": v(-170.97, 40.92) * mm, "end": v(-171.4, 39.57) * mm});
            skLineSegment(sketch, "E847", {"start": v(-171.4, 39.57) * mm, "end": v(-172.54, 37.04) * mm});
            skLineSegment(sketch, "E848", {"start": v(-172.54, 37.04) * mm, "end": v(-172.49, 35.93) * mm});
            skLineSegment(sketch, "E849", {"start": v(-172.49, 35.93) * mm, "end": v(-172.62, 35.31) * mm});
            skLineSegment(sketch, "E850", {"start": v(-172.62, 35.31) * mm, "end": v(-173.12, 34.32) * mm});
            skLineSegment(sketch, "E851", {"start": v(-173.12, 34.32) * mm, "end": v(-173.43, 33.24) * mm});
            skLineSegment(sketch, "E852", {"start": v(-173.43, 33.24) * mm, "end": v(-173.59, 32.7) * mm});
            skLineSegment(sketch, "E853", {"start": v(-173.59, 32.7) * mm, "end": v(-173.9, 31.6) * mm});
            skLineSegment(sketch, "E854", {"start": v(-173.9, 31.6) * mm, "end": v(-174.36, 29.75) * mm});
            skLineSegment(sketch, "E855", {"start": v(-174.36, 29.75) * mm, "end": v(-174.6, 28.81) * mm});
            skLineSegment(sketch, "E856", {"start": v(-174.6, 28.81) * mm, "end": v(-175.06, 26.95) * mm});
            skLineSegment(sketch, "E857", {"start": v(-175.06, 26.95) * mm, "end": v(-175.22, 26.49) * mm});
            skLineSegment(sketch, "E858", {"start": v(-175.22, 26.49) * mm, "end": v(-175.3, 26.25) * mm});
            skLineSegment(sketch, "E859", {"start": v(-175.3, 26.25) * mm, "end": v(-175.45, 25.79) * mm});
            skLineSegment(sketch, "E860", {"start": v(-175.45, 25.79) * mm, "end": v(-175.91, 23.93) * mm});
            skLineSegment(sketch, "E861", {"start": v(-175.91, 23.93) * mm, "end": v(-176.15, 23) * mm});
            skLineSegment(sketch, "E862", {"start": v(-176.15, 23) * mm, "end": v(-176.61, 21.13) * mm});
            skLineSegment(sketch, "E863", {"start": v(-176.61, 21.13) * mm, "end": v(-177.68, 15.68) * mm});
            skLineSegment(sketch, "E864", {"start": v(-177.68, 15.68) * mm, "end": v(-178.42, 12.97) * mm});
            skLineSegment(sketch, "E865", {"start": v(-178.42, 12.97) * mm, "end": v(-180.3, 7.75) * mm});
            skLineSegment(sketch, "E866", {"start": v(-180.3, 7.75) * mm, "end": v(-181.28, 5.18) * mm});
            skLineSegment(sketch, "E867", {"start": v(-181.28, 5.18) * mm, "end": v(-181.79, 3.9) * mm});
            skLineSegment(sketch, "E868", {"start": v(-181.79, 3.9) * mm, "end": v(-182.82, 1.35) * mm});
            skLineSegment(sketch, "E869", {"start": v(-182.82, 1.35) * mm, "end": v(-183.75, -0.52) * mm});
            skLineSegment(sketch, "E870", {"start": v(-183.75, -0.52) * mm, "end": v(-184.22, -1.45) * mm});
            skLineSegment(sketch, "E871", {"start": v(-184.22, -1.45) * mm, "end": v(-185.15, -3.31) * mm});
            skLineSegment(sketch, "E872", {"start": v(-185.15, -3.31) * mm, "end": v(-186.53, -5.5) * mm});
            skLineSegment(sketch, "E873", {"start": v(-186.53, -5.5) * mm, "end": v(-187.23, -6.58) * mm});
            skLineSegment(sketch, "E874", {"start": v(-187.23, -6.58) * mm, "end": v(-188.64, -8.74) * mm});
            skLineSegment(sketch, "E875", {"start": v(-188.64, -8.74) * mm, "end": v(-190.98, -12.5) * mm});
            skLineSegment(sketch, "E876", {"start": v(-190.98, -12.5) * mm, "end": v(-192.37, -14.28) * mm});
            skLineSegment(sketch, "E877", {"start": v(-192.37, -14.28) * mm, "end": v(-195.43, -17.47) * mm});
            skLineSegment(sketch, "E878", {"start": v(-195.43, -17.47) * mm, "end": v(-198.22, -20.72) * mm});
            skLineSegment(sketch, "E879", {"start": v(-198.22, -20.72) * mm, "end": v(-199.75, -22.25) * mm});
            skLineSegment(sketch, "E880", {"start": v(-199.75, -22.25) * mm, "end": v(-203, -25.04) * mm});
            skLineSegment(sketch, "E881", {"start": v(-203, -25.04) * mm, "end": v(-205.3, -26.56) * mm});
            skLineSegment(sketch, "E882", {"start": v(-205.3, -26.56) * mm, "end": v(-206.37, -27.47) * mm});
            skLineSegment(sketch, "E883", {"start": v(-206.37, -27.47) * mm, "end": v(-208.23, -29.5) * mm});
            skLineSegment(sketch, "E884", {"start": v(-208.23, -29.5) * mm, "end": v(-210.27, -32.1) * mm});
            skLineSegment(sketch, "E885", {"start": v(-210.27, -32.1) * mm, "end": v(-211.12, -33.6) * mm});
            skLineSegment(sketch, "E886", {"start": v(-211.12, -33.6) * mm, "end": v(-212.3, -36.68) * mm});
            skLineSegment(sketch, "E887", {"start": v(-212.3, -36.68) * mm, "end": v(-212.83, -38.54) * mm});
            skLineSegment(sketch, "E888", {"start": v(-212.83, -38.54) * mm, "end": v(-213.1, -39.48) * mm});
            skLineSegment(sketch, "E889", {"start": v(-213.1, -39.48) * mm, "end": v(-213.66, -41.33) * mm});
            skLineSegment(sketch, "E890", {"start": v(-213.66, -41.33) * mm, "end": v(-213.66, -44.13) * mm});
            skLineSegment(sketch, "E891", {"start": v(-213.66, -44.13) * mm, "end": v(-213.66, -45.52) * mm});
            skLineSegment(sketch, "E892", {"start": v(-213.66, -45.52) * mm, "end": v(-213.66, -48.32) * mm});
            skLineSegment(sketch, "E893", {"start": v(-213.66, -48.32) * mm, "end": v(-212.66, -51.84) * mm});
            skLineSegment(sketch, "E894", {"start": v(-212.66, -51.84) * mm, "end": v(-211.99, -53.57) * mm});
            skLineSegment(sketch, "E895", {"start": v(-211.99, -53.57) * mm, "end": v(-210.37, -56.85) * mm});
            skLineSegment(sketch, "E896", {"start": v(-210.37, -56.85) * mm, "end": v(-208.6, -59.38) * mm});
            skLineSegment(sketch, "E897", {"start": v(-208.6, -59.38) * mm, "end": v(-207.57, -60.57) * mm});
            skLineSegment(sketch, "E898", {"start": v(-207.57, -60.57) * mm, "end": v(-205.32, -62.67) * mm});
            skLineSegment(sketch, "E899", {"start": v(-205.32, -62.67) * mm, "end": v(-202.96, -64.14) * mm});
            skLineSegment(sketch, "E900", {"start": v(-202.96, -64.14) * mm, "end": v(-201.76, -64.84) * mm});
            skLineSegment(sketch, "E901", {"start": v(-201.76, -64.84) * mm, "end": v(-199.3, -66.16) * mm});
            skLineSegment(sketch, "E902", {"start": v(-199.3, -66.16) * mm, "end": v(-191.82, -68.25) * mm});
            skLineSegment(sketch, "E903", {"start": v(-191.82, -68.25) * mm, "end": v(-187.99, -69.07) * mm});
            skLineSegment(sketch, "E904", {"start": v(-187.99, -69.07) * mm, "end": v(-180.3, -70.24) * mm});
            skLineSegment(sketch, "E905", {"start": v(-180.3, -70.24) * mm, "end": v(-177.82, -70.55) * mm});
            skLineSegment(sketch, "E906", {"start": v(-177.82, -70.55) * mm, "end": v(-176.57, -70.7) * mm});
            skLineSegment(sketch, "E907", {"start": v(-176.57, -70.7) * mm, "end": v(-174.1, -71.01) * mm});
            skLineSegment(sketch, "E908", {"start": v(-174.1, -71.01) * mm, "end": v(-173.47, -71.1) * mm});
            skLineSegment(sketch, "E909", {"start": v(-173.47, -71.1) * mm, "end": v(-173.16, -71.13) * mm});
            skLineSegment(sketch, "E910", {"start": v(-173.16, -71.13) * mm, "end": v(-172.54, -71.2) * mm});
            skLineSegment(sketch, "E911", {"start": v(-172.54, -71.2) * mm, "end": v(-171.45, -71.2) * mm});
            skLineSegment(sketch, "E912", {"start": v(-171.45, -71.2) * mm, "end": v(-170.9, -71.2) * mm});
            skLineSegment(sketch, "E913", {"start": v(-170.9, -71.2) * mm, "end": v(-169.82, -71.2) * mm});
            skLineSegment(sketch, "E914", {"start": v(-169.82, -71.2) * mm, "end": v(-169.82, -71.36) * mm});
            skLineSegment(sketch, "E915", {"start": v(-169.82, -71.36) * mm, "end": v(-169.82, -71.44) * mm});
            skLineSegment(sketch, "E916", {"start": v(-169.82, -71.44) * mm, "end": v(-169.82, -71.6) * mm});
            skLineSegment(sketch, "E917", {"start": v(-169.82, -71.6) * mm, "end": v(-167.5, -71.6) * mm});
            skLineSegment(sketch, "E918", {"start": v(-167.5, -71.6) * mm, "end": v(-166.33, -71.6) * mm});
            skLineSegment(sketch, "E919", {"start": v(-166.33, -71.6) * mm, "end": v(-164, -71.6) * mm});
            skLineSegment(sketch, "E920", {"start": v(-164, -71.6) * mm, "end": v(-164, -71.75) * mm});
            skLineSegment(sketch, "E921", {"start": v(-164, -71.75) * mm, "end": v(-164, -71.83) * mm});
            skLineSegment(sketch, "E922", {"start": v(-164, -71.83) * mm, "end": v(-164, -71.98) * mm});
            skLineSegment(sketch, "E923", {"start": v(-193.1, -66.16) * mm, "end": v(-191.4, -66.16) * mm});
            skLineSegment(sketch, "E924", {"start": v(-191.4, -66.16) * mm, "end": v(-190.54, -66.16) * mm});
            skLineSegment(sketch, "E925", {"start": v(-190.54, -66.16) * mm, "end": v(-188.83, -66.16) * mm});
            skLineSegment(sketch, "E926", {"start": v(-188.83, -66.16) * mm, "end": v(-185.13, -65.28) * mm});
            skLineSegment(sketch, "E927", {"start": v(-185.13, -65.28) * mm, "end": v(-183.3, -64.6) * mm});
            skLineSegment(sketch, "E928", {"start": v(-183.3, -64.6) * mm, "end": v(-179.91, -62.86) * mm});
            skLineSegment(sketch, "E929", {"start": v(-179.91, -62.86) * mm, "end": v(-179.56, -62.43) * mm});
            skLineSegment(sketch, "E930", {"start": v(-179.56, -62.43) * mm, "end": v(-179.28, -62.24) * mm});
            skLineSegment(sketch, "E931", {"start": v(-179.28, -62.24) * mm, "end": v(-178.75, -62.09) * mm});
            skLineSegment(sketch, "E932", {"start": v(-178.75, -62.09) * mm, "end": v(-176.96, -60.3) * mm});
            skLineSegment(sketch, "E933", {"start": v(-176.96, -60.3) * mm, "end": v(-176.07, -59.41) * mm});
            skLineSegment(sketch, "E934", {"start": v(-176.07, -59.41) * mm, "end": v(-174.28, -57.63) * mm});
            skLineSegment(sketch, "E935", {"start": v(-174.28, -57.63) * mm, "end": v(-172.66, -55.38) * mm});
            skLineSegment(sketch, "E936", {"start": v(-172.66, -55.38) * mm, "end": v(-172, -54.07) * mm});
            skLineSegment(sketch, "E937", {"start": v(-172, -54.07) * mm, "end": v(-171.18, -51.42) * mm});
            skLineSegment(sketch, "E938", {"start": v(-171.18, -51.42) * mm, "end": v(-170.96, -50.14) * mm});
            skLineSegment(sketch, "E939", {"start": v(-170.96, -50.14) * mm, "end": v(-170.76, -49.5) * mm});
            skLineSegment(sketch, "E940", {"start": v(-170.76, -49.5) * mm, "end": v(-170.21, -48.32) * mm});
            skLineSegment(sketch, "E941", {"start": v(-170.21, -48.32) * mm, "end": v(-170.21, -45.99) * mm});
            skLineSegment(sketch, "E942", {"start": v(-170.21, -45.99) * mm, "end": v(-170.21, -44.82) * mm});
            skLineSegment(sketch, "E943", {"start": v(-170.21, -44.82) * mm, "end": v(-170.21, -42.5) * mm});
            skLineSegment(sketch, "E944", {"start": v(-170.21, -42.5) * mm, "end": v(-170.76, -39.6) * mm});
            skLineSegment(sketch, "E945", {"start": v(-170.76, -39.6) * mm, "end": v(-171.24, -38.16) * mm});
            skLineSegment(sketch, "E946", {"start": v(-171.24, -38.16) * mm, "end": v(-172.54, -35.51) * mm});
            skLineSegment(sketch, "E947", {"start": v(-172.54, -35.51) * mm, "end": v(-174.02, -32.85) * mm});
            skLineSegment(sketch, "E948", {"start": v(-174.02, -32.85) * mm, "end": v(-175, -31.6) * mm});
            skLineSegment(sketch, "E949", {"start": v(-175, -31.6) * mm, "end": v(-177.2, -29.5) * mm});
            skLineSegment(sketch, "E950", {"start": v(-177.2, -29.5) * mm, "end": v(-178.44, -28.9) * mm});
            skLineSegment(sketch, "E951", {"start": v(-179.04, -28.44) * mm, "end": v(-179.91, -27.37) * mm});
            skLineSegment(sketch, "E952", {"start": v(-179.91, -27.37) * mm, "end": v(-180.42, -27.45) * mm});
            skLineSegment(sketch, "E953", {"start": v(-180.42, -27.45) * mm, "end": v(-180.84, -27.25) * mm});
            skLineSegment(sketch, "E954", {"start": v(-180.84, -27.25) * mm, "end": v(-181.07, -26.78) * mm});
            skLineSegment(sketch, "E955", {"start": v(-181.07, -26.78) * mm, "end": v(-182.67, -26.2) * mm});
            skLineSegment(sketch, "E956", {"start": v(-182.67, -26.2) * mm, "end": v(-183.46, -25.85) * mm});
            skLineSegment(sketch, "E957", {"start": v(-183.46, -25.85) * mm, "end": v(-184.95, -25.04) * mm});
            skLineSegment(sketch, "E958", {"start": v(-184.95, -25.04) * mm, "end": v(-186.38, -25.13) * mm});
            skLineSegment(sketch, "E959", {"start": v(-186.38, -25.13) * mm, "end": v(-187.2, -24.95) * mm});
            skLineSegment(sketch, "E960", {"start": v(-187.2, -24.95) * mm, "end": v(-188.45, -24.26) * mm});
            skLineSegment(sketch, "E961", {"start": v(-188.45, -24.26) * mm, "end": v(-190.62, -24.26) * mm});
            skLineSegment(sketch, "E962", {"start": v(-190.62, -24.26) * mm, "end": v(-191.7, -24.26) * mm});
            skLineSegment(sketch, "E963", {"start": v(-191.7, -24.26) * mm, "end": v(-193.88, -24.26) * mm});
            skLineSegment(sketch, "E964", {"start": v(-193.88, -24.26) * mm, "end": v(-196.08, -24.86) * mm});
            skLineSegment(sketch, "E965", {"start": v(-196.08, -24.86) * mm, "end": v(-197.17, -25.21) * mm});
            skLineSegment(sketch, "E966", {"start": v(-197.17, -25.21) * mm, "end": v(-199.3, -26) * mm});
            skLineSegment(sketch, "E967", {"start": v(-199.3, -26) * mm, "end": v(-201.05, -26.61) * mm});
            skLineSegment(sketch, "E968", {"start": v(-201.05, -26.61) * mm, "end": v(-201.9, -27.06) * mm});
            skLineSegment(sketch, "E969", {"start": v(-201.9, -27.06) * mm, "end": v(-203.38, -28.14) * mm});
            skLineSegment(sketch, "E970", {"start": v(-203.38, -28.14) * mm, "end": v(-205.78, -29.98) * mm});
            skLineSegment(sketch, "E971", {"start": v(-205.78, -29.98) * mm, "end": v(-206.87, -31.11) * mm});
            skLineSegment(sketch, "E972", {"start": v(-206.87, -31.11) * mm, "end": v(-208.62, -33.57) * mm});
            skLineSegment(sketch, "E973", {"start": v(-208.62, -33.57) * mm, "end": v(-210.27, -36.23) * mm});
            skLineSegment(sketch, "E974", {"start": v(-210.27, -36.23) * mm, "end": v(-210.92, -37.73) * mm});
            skLineSegment(sketch, "E975", {"start": v(-210.92, -37.73) * mm, "end": v(-211.72, -40.75) * mm});
            skLineSegment(sketch, "E976", {"start": v(-211.72, -40.75) * mm, "end": v(-211.46, -41.25) * mm});
            skLineSegment(sketch, "E977", {"start": v(-211.46, -41.25) * mm, "end": v(-211.62, -41.82) * mm});
            skLineSegment(sketch, "E978", {"start": v(-211.62, -41.82) * mm, "end": v(-212.11, -42.1) * mm});
            skLineSegment(sketch, "E979", {"start": v(-212.11, -42.1) * mm, "end": v(-212.11, -44.6) * mm});
            skLineSegment(sketch, "E980", {"start": v(-212.11, -44.6) * mm, "end": v(-212.11, -45.83) * mm});
            skLineSegment(sketch, "E981", {"start": v(-212.11, -45.83) * mm, "end": v(-212.11, -48.32) * mm});
            skLineSegment(sketch, "E982", {"start": v(-212.11, -48.32) * mm, "end": v(-211.47, -49.99) * mm});
            skLineSegment(sketch, "E983", {"start": v(-211.47, -49.99) * mm, "end": v(-211.2, -50.85) * mm});
            skLineSegment(sketch, "E984", {"start": v(-211.2, -50.85) * mm, "end": v(-210.75, -52.58) * mm});
            skLineSegment(sketch, "E985", {"start": v(-210.75, -52.58) * mm, "end": v(-209.98, -54.14) * mm});
            skLineSegment(sketch, "E986", {"start": v(-209.98, -54.14) * mm, "end": v(-209.6, -54.91) * mm});
            skLineSegment(sketch, "E987", {"start": v(-209.6, -54.91) * mm, "end": v(-208.81, -56.46) * mm});
            skLineSegment(sketch, "E988", {"start": v(-208.81, -56.46) * mm, "end": v(-208.38, -56.81) * mm});
            skLineSegment(sketch, "E989", {"start": v(-208.38, -56.81) * mm, "end": v(-208.2, -57.09) * mm});
            skLineSegment(sketch, "E990", {"start": v(-208.2, -57.09) * mm, "end": v(-208.04, -57.63) * mm});
            skLineSegment(sketch, "E991", {"start": v(-208.04, -57.63) * mm, "end": v(-206.25, -59.41) * mm});
            skLineSegment(sketch, "E992", {"start": v(-206.25, -59.41) * mm, "end": v(-205.36, -60.3) * mm});
            skLineSegment(sketch, "E993", {"start": v(-205.36, -60.3) * mm, "end": v(-203.58, -62.09) * mm});
            skLineSegment(sketch, "E994", {"start": v(-203.58, -62.09) * mm, "end": v(-200.71, -63.93) * mm});
            skLineSegment(sketch, "E995", {"start": v(-200.71, -63.93) * mm, "end": v(-199.1, -64.66) * mm});
            skLineSegment(sketch, "E996", {"start": v(-199.1, -64.66) * mm, "end": v(-195.82, -65.58) * mm});
            skLineSegment(sketch, "E997", {"start": v(-195.82, -65.58) * mm, "end": v(-194.7, -65.52) * mm});
            skLineSegment(sketch, "E998", {"start": v(-194.7, -65.52) * mm, "end": v(-194.09, -65.65) * mm});
            skLineSegment(sketch, "E999", {"start": v(-194.09, -65.65) * mm, "end": v(-193.1, -66.16) * mm});
            skLineSegment(sketch, "E1000", {"start": v(-194.65, -64.61) * mm, "end": v(-191.86, -64.61) * mm});
            skLineSegment(sketch, "E1001", {"start": v(-191.86, -64.61) * mm, "end": v(-190.46, -64.61) * mm});
            skLineSegment(sketch, "E1002", {"start": v(-190.46, -64.61) * mm, "end": v(-187.67, -64.61) * mm});
            skLineSegment(sketch, "E1003", {"start": v(-187.67, -64.61) * mm, "end": v(-186.11, -64.08) * mm});
            skLineSegment(sketch, "E1004", {"start": v(-186.11, -64.08) * mm, "end": v(-185.34, -63.8) * mm});
            skLineSegment(sketch, "E1005", {"start": v(-185.34, -63.8) * mm, "end": v(-183.79, -63.25) * mm});
            skLineSegment(sketch, "E1006", {"start": v(-183.79, -63.25) * mm, "end": v(-181.73, -62.61) * mm});
            skLineSegment(sketch, "E1007", {"start": v(-181.73, -62.61) * mm, "end": v(-180.7, -62.01) * mm});
            skLineSegment(sketch, "E1008", {"start": v(-180.7, -62.01) * mm, "end": v(-179.13, -60.54) * mm});
            skLineSegment(sketch, "E1009", {"start": v(-179.13, -60.54) * mm, "end": v(-177.06, -59.1) * mm});
            skLineSegment(sketch, "E1010", {"start": v(-177.06, -59.1) * mm, "end": v(-176.1, -58.15) * mm});
            skLineSegment(sketch, "E1011", {"start": v(-176.1, -58.15) * mm, "end": v(-174.67, -56.08) * mm});
            skLineSegment(sketch, "E1012", {"start": v(-174.67, -56.08) * mm, "end": v(-173.9, -54.52) * mm});
            skLineSegment(sketch, "E1013", {"start": v(-173.9, -54.52) * mm, "end": v(-173.5, -53.75) * mm});
            skLineSegment(sketch, "E1014", {"start": v(-173.5, -53.75) * mm, "end": v(-172.73, -52.2) * mm});
            skLineSegment(sketch, "E1015", {"start": v(-172.73, -52.2) * mm, "end": v(-172.53, -51.06) * mm});
            skLineSegment(sketch, "E1016", {"start": v(-172.53, -51.06) * mm, "end": v(-172.33, -50.49) * mm});
            skLineSegment(sketch, "E1017", {"start": v(-172.33, -50.49) * mm, "end": v(-171.76, -49.48) * mm});
            skLineSegment(sketch, "E1018", {"start": v(-171.76, -49.48) * mm, "end": v(-172.04, -48.58) * mm});
            skLineSegment(sketch, "E1019", {"start": v(-172.04, -48.58) * mm, "end": v(-171.93, -47.92) * mm});
            skLineSegment(sketch, "E1020", {"start": v(-171.93, -47.92) * mm, "end": v(-171.37, -47.15) * mm});
            skLineSegment(sketch, "E1021", {"start": v(-171.37, -47.15) * mm, "end": v(-171.37, -45.6) * mm});
            skLineSegment(sketch, "E1022", {"start": v(-171.37, -45.6) * mm, "end": v(-171.37, -44.82) * mm});
            skLineSegment(sketch, "E1023", {"start": v(-171.37, -44.82) * mm, "end": v(-171.37, -43.27) * mm});
            skLineSegment(sketch, "E1024", {"start": v(-171.37, -43.27) * mm, "end": v(-172.06, -40.08) * mm});
            skLineSegment(sketch, "E1025", {"start": v(-172.06, -40.08) * mm, "end": v(-172.57, -38.5) * mm});
            skLineSegment(sketch, "E1026", {"start": v(-172.57, -38.5) * mm, "end": v(-173.9, -35.51) * mm});
            skLineSegment(sketch, "E1027", {"start": v(-173.9, -35.51) * mm, "end": v(-174.64, -34.67) * mm});
            skLineSegment(sketch, "E1028", {"start": v(-174.64, -34.67) * mm, "end": v(-174.96, -34.2) * mm});
            skLineSegment(sketch, "E1029", {"start": v(-174.96, -34.2) * mm, "end": v(-175.45, -33.18) * mm});
            skLineSegment(sketch, "E1030", {"start": v(-175.45, -33.18) * mm, "end": v(-176.92, -31.71) * mm});
            skLineSegment(sketch, "E1031", {"start": v(-176.92, -31.71) * mm, "end": v(-177.66, -30.97) * mm});
            skLineSegment(sketch, "E1032", {"start": v(-177.66, -30.97) * mm, "end": v(-179.13, -29.5) * mm});
            skLineSegment(sketch, "E1033", {"start": v(-179.13, -29.5) * mm, "end": v(-179.67, -29.34) * mm});
            skLineSegment(sketch, "E1034", {"start": v(-179.67, -29.34) * mm, "end": v(-179.95, -29.16) * mm});
            skLineSegment(sketch, "E1035", {"start": v(-179.95, -29.16) * mm, "end": v(-180.3, -28.72) * mm});
            skLineSegment(sketch, "E1036", {"start": v(-180.3, -28.72) * mm, "end": v(-181.85, -27.95) * mm});
            skLineSegment(sketch, "E1037", {"start": v(-181.85, -27.95) * mm, "end": v(-182.63, -27.56) * mm});
            skLineSegment(sketch, "E1038", {"start": v(-182.63, -27.56) * mm, "end": v(-184.18, -26.78) * mm});
            skLineSegment(sketch, "E1039", {"start": v(-184.18, -26.78) * mm, "end": v(-185.31, -26.58) * mm});
            skLineSegment(sketch, "E1040", {"start": v(-185.31, -26.58) * mm, "end": v(-185.89, -26.38) * mm});
            skLineSegment(sketch, "E1041", {"start": v(-185.89, -26.38) * mm, "end": v(-186.9, -25.81) * mm});
            skLineSegment(sketch, "E1042", {"start": v(-186.9, -25.81) * mm, "end": v(-189.05, -25.57) * mm});
            skLineSegment(sketch, "E1043", {"start": v(-189.05, -25.57) * mm, "end": v(-190.15, -25.53) * mm});
            skLineSegment(sketch, "E1044", {"start": v(-190.15, -25.53) * mm, "end": v(-192.33, -25.62) * mm});
            skLineSegment(sketch, "E1045", {"start": v(-192.33, -25.62) * mm, "end": v(-194.2, -25.79) * mm});
            skLineSegment(sketch, "E1046", {"start": v(-194.2, -25.79) * mm, "end": v(-195.15, -25.94) * mm});
            skLineSegment(sketch, "E1047", {"start": v(-195.15, -25.94) * mm, "end": v(-196.98, -26.4) * mm});
            skLineSegment(sketch, "E1048", {"start": v(-196.98, -26.4) * mm, "end": v(-197.41, -26.63) * mm});
            skLineSegment(sketch, "E1049", {"start": v(-197.41, -26.63) * mm, "end": v(-197.66, -26.71) * mm});
            skLineSegment(sketch, "E1050", {"start": v(-197.66, -26.71) * mm, "end": v(-198.15, -26.78) * mm});
            skLineSegment(sketch, "E1051", {"start": v(-198.15, -26.78) * mm, "end": v(-199.7, -27.56) * mm});
            skLineSegment(sketch, "E1052", {"start": v(-199.7, -27.56) * mm, "end": v(-200.47, -27.95) * mm});
            skLineSegment(sketch, "E1053", {"start": v(-200.47, -27.95) * mm, "end": v(-202.02, -28.72) * mm});
            skLineSegment(sketch, "E1054", {"start": v(-202.02, -28.72) * mm, "end": v(-202.37, -29.16) * mm});
            skLineSegment(sketch, "E1055", {"start": v(-202.37, -29.16) * mm, "end": v(-202.65, -29.34) * mm});
            skLineSegment(sketch, "E1056", {"start": v(-202.65, -29.34) * mm, "end": v(-203.19, -29.5) * mm});
            skLineSegment(sketch, "E1057", {"start": v(-203.19, -29.5) * mm, "end": v(-204.66, -30.97) * mm});
            skLineSegment(sketch, "E1058", {"start": v(-204.66, -30.97) * mm, "end": v(-205.4, -31.71) * mm});
            skLineSegment(sketch, "E1059", {"start": v(-205.4, -31.71) * mm, "end": v(-206.87, -33.18) * mm});
            skLineSegment(sketch, "E1060", {"start": v(-206.87, -33.18) * mm, "end": v(-207.36, -34.2) * mm});
            skLineSegment(sketch, "E1061", {"start": v(-207.36, -34.2) * mm, "end": v(-207.69, -34.67) * mm});
            skLineSegment(sketch, "E1062", {"start": v(-207.69, -34.67) * mm, "end": v(-208.43, -35.51) * mm});
            skLineSegment(sketch, "E1063", {"start": v(-208.43, -35.51) * mm, "end": v(-209, -37.11) * mm});
            skLineSegment(sketch, "E1064", {"start": v(-209, -37.11) * mm, "end": v(-209.36, -37.9) * mm});
            skLineSegment(sketch, "E1065", {"start": v(-209.36, -37.9) * mm, "end": v(-210.17, -39.4) * mm});
            skLineSegment(sketch, "E1066", {"start": v(-210.17, -39.4) * mm, "end": v(-210.66, -42.32) * mm});
            skLineSegment(sketch, "E1067", {"start": v(-210.66, -42.32) * mm, "end": v(-210.82, -43.8) * mm});
            skLineSegment(sketch, "E1068", {"start": v(-210.82, -43.8) * mm, "end": v(-210.95, -46.76) * mm});
            skLineSegment(sketch, "E1069", {"start": v(-210.95, -46.76) * mm, "end": v(-210.44, -49.12) * mm});
            skLineSegment(sketch, "E1070", {"start": v(-210.44, -49.12) * mm, "end": v(-210.12, -50.29) * mm});
            skLineSegment(sketch, "E1071", {"start": v(-210.12, -50.29) * mm, "end": v(-209.4, -52.58) * mm});
            skLineSegment(sketch, "E1072", {"start": v(-209.4, -52.58) * mm, "end": v(-208.36, -55.02) * mm});
            skLineSegment(sketch, "E1073", {"start": v(-208.36, -55.02) * mm, "end": v(-207.63, -56.2) * mm});
            skLineSegment(sketch, "E1074", {"start": v(-207.63, -56.2) * mm, "end": v(-205.9, -58.2) * mm});
            skLineSegment(sketch, "E1075", {"start": v(-205.9, -58.2) * mm, "end": v(-204, -60.22) * mm});
            skLineSegment(sketch, "E1076", {"start": v(-204, -60.22) * mm, "end": v(-202.88, -61.11) * mm});
            skLineSegment(sketch, "E1077", {"start": v(-202.88, -61.11) * mm, "end": v(-200.47, -62.48) * mm});
            skLineSegment(sketch, "E1078", {"start": v(-200.47, -62.48) * mm, "end": v(-198.86, -63.01) * mm});
            skLineSegment(sketch, "E1079", {"start": v(-198.86, -63.01) * mm, "end": v(-198.07, -63.37) * mm});
            skLineSegment(sketch, "E1080", {"start": v(-198.07, -63.37) * mm, "end": v(-196.6, -64.22) * mm});
            skLineSegment(sketch, "E1081", {"start": v(-196.6, -64.22) * mm, "end": v(-195.86, -63.92) * mm});
            skLineSegment(sketch, "E1082", {"start": v(-195.86, -63.92) * mm, "end": v(-195.21, -64.05) * mm});
            skLineSegment(sketch, "E1083", {"start": v(-195.21, -64.05) * mm, "end": v(-194.65, -64.61) * mm});
            skLineSegment(sketch, "E1084", {"start": v(-110.66, -59.57) * mm, "end": v(-108.77, -59.71) * mm});
            skLineSegment(sketch, "E1085", {"start": v(-108.77, -59.71) * mm, "end": v(-107.73, -59.54) * mm});
            skLineSegment(sketch, "E1086", {"start": v(-107.73, -59.54) * mm, "end": v(-106, -58.8) * mm});
            skLineSegment(sketch, "E1087", {"start": v(-106, -58.8) * mm, "end": v(-99.9, -56.74) * mm});
            skLineSegment(sketch, "E1088", {"start": v(-99.9, -56.74) * mm, "end": v(-96.89, -55.53) * mm});
            skLineSegment(sketch, "E1089", {"start": v(-96.89, -55.53) * mm, "end": v(-91.06, -52.78) * mm});
            skLineSegment(sketch, "E1090", {"start": v(-91.06, -52.78) * mm, "end": v(-86.97, -51.24) * mm});
            skLineSegment(sketch, "E1091", {"start": v(-86.97, -51.24) * mm, "end": v(-84.97, -50.2) * mm});
            skLineSegment(sketch, "E1092", {"start": v(-84.97, -50.2) * mm, "end": v(-81.36, -47.73) * mm});
            skLineSegment(sketch, "E1093", {"start": v(-81.36, -47.73) * mm, "end": v(-80.9, -47.27) * mm});
            skLineSegment(sketch, "E1094", {"start": v(-80.9, -47.27) * mm, "end": v(-80.67, -47.04) * mm});
            skLineSegment(sketch, "E1095", {"start": v(-80.67, -47.04) * mm, "end": v(-80.2, -46.57) * mm});
            skLineSegment(sketch, "E1096", {"start": v(-80.2, -46.57) * mm, "end": v(-79.95, -45.66) * mm});
            skLineSegment(sketch, "E1097", {"start": v(-79.95, -45.66) * mm, "end": v(-80.05, -45.02) * mm});
            skLineSegment(sketch, "E1098", {"start": v(-80.05, -45.02) * mm, "end": v(-80.59, -44.24) * mm});
            skLineSegment(sketch, "E1099", {"start": v(-80.59, -44.24) * mm, "end": v(-81.05, -43.78) * mm});
            skLineSegment(sketch, "E1100", {"start": v(-81.05, -43.78) * mm, "end": v(-81.29, -43.54) * mm});
            skLineSegment(sketch, "E1101", {"start": v(-81.29, -43.54) * mm, "end": v(-81.75, -43.08) * mm});
            skLineSegment(sketch, "E1102", {"start": v(-81.75, -43.08) * mm, "end": v(-85.17, -41.37) * mm});
            skLineSegment(sketch, "E1103", {"start": v(-85.17, -41.37) * mm, "end": v(-86.87, -40.52) * mm});
            skLineSegment(sketch, "E1104", {"start": v(-86.87, -40.52) * mm, "end": v(-90.29, -38.81) * mm});
            skLineSegment(sketch, "E1105", {"start": v(-90.29, -38.81) * mm, "end": v(-91.58, -38.23) * mm});
            skLineSegment(sketch, "E1106", {"start": v(-91.58, -38.23) * mm, "end": v(-92.37, -38.1) * mm});
            skLineSegment(sketch, "E1107", {"start": v(-92.37, -38.1) * mm, "end": v(-93.78, -38.23) * mm});
            skLineSegment(sketch, "E1108", {"start": v(-93.78, -38.23) * mm, "end": v(-93.95, -38.8) * mm});
            skLineSegment(sketch, "E1109", {"start": v(-93.95, -38.8) * mm, "end": v(-94.34, -39.13) * mm});
            skLineSegment(sketch, "E1110", {"start": v(-94.34, -39.13) * mm, "end": v(-94.94, -39.2) * mm});
            skLineSegment(sketch, "E1111", {"start": v(-94.94, -39.2) * mm, "end": v(-98.67, -42.92) * mm});
            skLineSegment(sketch, "E1112", {"start": v(-98.67, -42.92) * mm, "end": v(-100.53, -44.79) * mm});
            skLineSegment(sketch, "E1113", {"start": v(-100.53, -44.79) * mm, "end": v(-104.25, -48.5) * mm});
            skLineSegment(sketch, "E1114", {"start": v(-104.25, -48.5) * mm, "end": v(-105.96, -49.9) * mm});
            skLineSegment(sketch, "E1115", {"start": v(-105.96, -49.9) * mm, "end": v(-106.82, -50.6) * mm});
            skLineSegment(sketch, "E1116", {"start": v(-106.82, -50.6) * mm, "end": v(-108.52, -52) * mm});
            skLineSegment(sketch, "E1117", {"start": v(-108.52, -52) * mm, "end": v(-110, -53.48) * mm});
            skLineSegment(sketch, "E1118", {"start": v(-110, -53.48) * mm, "end": v(-110.73, -54.21) * mm});
            skLineSegment(sketch, "E1119", {"start": v(-110.73, -54.21) * mm, "end": v(-112.2, -55.69) * mm});
            skLineSegment(sketch, "E1120", {"start": v(-112.2, -55.69) * mm, "end": v(-112.7, -56.57) * mm});
            skLineSegment(sketch, "E1121", {"start": v(-112.7, -56.57) * mm, "end": v(-112.64, -57.42) * mm});
            skLineSegment(sketch, "E1122", {"start": v(-112.64, -57.42) * mm, "end": v(-112.01, -58.2) * mm});
            skLineSegment(sketch, "E1123", {"start": v(-112.01, -58.2) * mm, "end": v(-111.47, -58.75) * mm});
            skLineSegment(sketch, "E1124", {"start": v(-111.47, -58.75) * mm, "end": v(-111.2, -59.02) * mm});
            skLineSegment(sketch, "E1125", {"start": v(-111.2, -59.02) * mm, "end": v(-110.66, -59.57) * mm});
            skLineSegment(sketch, "E1126", {"start": v(-110.46, -58.4) * mm, "end": v(-109.69, -58.49) * mm});
            skLineSegment(sketch, "E1127", {"start": v(-109.69, -58.49) * mm, "end": v(-109.27, -58.45) * mm});
            skLineSegment(sketch, "E1128", {"start": v(-109.27, -58.45) * mm, "end": v(-108.52, -58.2) * mm});
            skLineSegment(sketch, "E1129", {"start": v(-108.52, -58.2) * mm, "end": v(-106.2, -57.43) * mm});
            skLineSegment(sketch, "E1130", {"start": v(-106.2, -57.43) * mm, "end": v(-105.03, -57.05) * mm});
            skLineSegment(sketch, "E1131", {"start": v(-105.03, -57.05) * mm, "end": v(-102.7, -56.27) * mm});
            skLineSegment(sketch, "E1132", {"start": v(-102.7, -56.27) * mm, "end": v(-100.37, -55.35) * mm});
            skLineSegment(sketch, "E1133", {"start": v(-100.37, -55.35) * mm, "end": v(-99.2, -54.89) * mm});
            skLineSegment(sketch, "E1134", {"start": v(-99.2, -54.89) * mm, "end": v(-96.88, -53.94) * mm});
            skLineSegment(sketch, "E1135", {"start": v(-96.88, -53.94) * mm, "end": v(-95.33, -53.31) * mm});
            skLineSegment(sketch, "E1136", {"start": v(-95.33, -53.31) * mm, "end": v(-94.56, -53) * mm});
            skLineSegment(sketch, "E1137", {"start": v(-94.56, -53) * mm, "end": v(-93, -52.39) * mm});
            skLineSegment(sketch, "E1138", {"start": v(-93, -52.39) * mm, "end": v(-91.14, -51.46) * mm});
            skLineSegment(sketch, "E1139", {"start": v(-91.14, -51.46) * mm, "end": v(-90.2, -51) * mm});
            skLineSegment(sketch, "E1140", {"start": v(-90.2, -51) * mm, "end": v(-88.35, -50.06) * mm});
            skLineSegment(sketch, "E1141", {"start": v(-88.35, -50.06) * mm, "end": v(-85.49, -49.08) * mm});
            skLineSegment(sketch, "E1142", {"start": v(-85.49, -49.08) * mm, "end": v(-84.09, -48.3) * mm});
            skLineSegment(sketch, "E1143", {"start": v(-84.09, -48.3) * mm, "end": v(-81.75, -46.38) * mm});
            skLineSegment(sketch, "E1144", {"start": v(-81.75, -46.38) * mm, "end": v(-81.42, -46.04) * mm});
            skLineSegment(sketch, "E1145", {"start": v(-81.42, -46.04) * mm, "end": v(-81.35, -45.64) * mm});
            skLineSegment(sketch, "E1146", {"start": v(-81.35, -45.64) * mm, "end": v(-81.56, -45.21) * mm});
            skLineSegment(sketch, "E1147", {"start": v(-81.56, -45.21) * mm, "end": v(-81.72, -44.79) * mm});
            skLineSegment(sketch, "E1148", {"start": v(-81.72, -44.79) * mm, "end": v(-81.84, -44.58) * mm});
            skLineSegment(sketch, "E1149", {"start": v(-81.84, -44.58) * mm, "end": v(-82.14, -44.24) * mm});
            skLineSegment(sketch, "E1150", {"start": v(-82.14, -44.24) * mm, "end": v(-84, -43.31) * mm});
            skLineSegment(sketch, "E1151", {"start": v(-84, -43.31) * mm, "end": v(-84.93, -42.85) * mm});
            skLineSegment(sketch, "E1152", {"start": v(-84.93, -42.85) * mm, "end": v(-86.8, -41.91) * mm});
            skLineSegment(sketch, "E1153", {"start": v(-86.8, -41.91) * mm, "end": v(-87.26, -41.76) * mm});
            skLineSegment(sketch, "E1154", {"start": v(-87.26, -41.76) * mm, "end": v(-87.5, -41.68) * mm});
            skLineSegment(sketch, "E1155", {"start": v(-87.5, -41.68) * mm, "end": v(-87.96, -41.53) * mm});
            skLineSegment(sketch, "E1156", {"start": v(-87.96, -41.53) * mm, "end": v(-89.51, -40.75) * mm});
            skLineSegment(sketch, "E1157", {"start": v(-89.51, -40.75) * mm, "end": v(-90.29, -40.36) * mm});
            skLineSegment(sketch, "E1158", {"start": v(-90.29, -40.36) * mm, "end": v(-91.84, -39.59) * mm});
            skLineSegment(sketch, "E1159", {"start": v(-91.84, -39.59) * mm, "end": v(-92.5, -39.35) * mm});
            skLineSegment(sketch, "E1160", {"start": v(-92.5, -39.35) * mm, "end": v(-93, -39.4) * mm});
            skLineSegment(sketch, "E1161", {"start": v(-93, -39.4) * mm, "end": v(-93.59, -39.78) * mm});
            skLineSegment(sketch, "E1162", {"start": v(-93.59, -39.78) * mm, "end": v(-96.3, -42.5) * mm});
            skLineSegment(sketch, "E1163", {"start": v(-96.3, -42.5) * mm, "end": v(-97.66, -43.85) * mm});
            skLineSegment(sketch, "E1164", {"start": v(-97.66, -43.85) * mm, "end": v(-100.37, -46.57) * mm});
            skLineSegment(sketch, "E1165", {"start": v(-100.37, -46.57) * mm, "end": v(-100.69, -46.73) * mm});
            skLineSegment(sketch, "E1166", {"start": v(-100.69, -46.73) * mm, "end": v(-100.84, -46.8) * mm});
            skLineSegment(sketch, "E1167", {"start": v(-100.84, -46.8) * mm, "end": v(-101.15, -46.96) * mm});
            skLineSegment(sketch, "E1168", {"start": v(-101.15, -46.96) * mm, "end": v(-102.86, -48.66) * mm});
            skLineSegment(sketch, "E1169", {"start": v(-102.86, -48.66) * mm, "end": v(-103.71, -49.52) * mm});
            skLineSegment(sketch, "E1170", {"start": v(-103.71, -49.52) * mm, "end": v(-105.42, -51.23) * mm});
            skLineSegment(sketch, "E1171", {"start": v(-105.42, -51.23) * mm, "end": v(-107.99, -52.92) * mm});
            skLineSegment(sketch, "E1172", {"start": v(-107.99, -52.92) * mm, "end": v(-109.17, -54.02) * mm});
            skLineSegment(sketch, "E1173", {"start": v(-109.17, -54.02) * mm, "end": v(-111.04, -56.46) * mm});
            skLineSegment(sketch, "E1174", {"start": v(-111.04, -56.46) * mm, "end": v(-111.16, -57.26) * mm});
            skLineSegment(sketch, "E1175", {"start": v(-111.16, -57.26) * mm, "end": v(-111, -57.8) * mm});
            skLineSegment(sketch, "E1176", {"start": v(-111, -57.8) * mm, "end": v(-110.46, -58.4) * mm});
            skLineSegment(sketch, "E1177", {"start": v(-156.83, -20.77) * mm, "end": v(-154.92, -20.25) * mm});
            skLineSegment(sketch, "E1178", {"start": v(-154.92, -20.25) * mm, "end": v(-153.97, -19.8) * mm});
            skLineSegment(sketch, "E1179", {"start": v(-153.97, -19.8) * mm, "end": v(-152.36, -18.64) * mm});
            skLineSegment(sketch, "E1180", {"start": v(-152.36, -18.64) * mm, "end": v(-148.56, -14.83) * mm});
            skLineSegment(sketch, "E1181", {"start": v(-148.56, -14.83) * mm, "end": v(-146.66, -12.93) * mm});
            skLineSegment(sketch, "E1182", {"start": v(-146.66, -12.93) * mm, "end": v(-142.86, -9.13) * mm});
            skLineSegment(sketch, "E1183", {"start": v(-142.86, -9.13) * mm, "end": v(-142.27, -7.88) * mm});
            skLineSegment(sketch, "E1184", {"start": v(-142.27, -7.88) * mm, "end": v(-141.8, -7.28) * mm});
            skLineSegment(sketch, "E1185", {"start": v(-141.8, -7.28) * mm, "end": v(-140.72, -6.41) * mm});
            skLineSegment(sketch, "E1186", {"start": v(-140.72, -6.41) * mm, "end": v(-140.81, -5.9) * mm});
            skLineSegment(sketch, "E1187", {"start": v(-140.81, -5.9) * mm, "end": v(-140.6, -5.49) * mm});
            skLineSegment(sketch, "E1188", {"start": v(-140.6, -5.49) * mm, "end": v(-140.14, -5.25) * mm});
            skLineSegment(sketch, "E1189", {"start": v(-140.14, -5.25) * mm, "end": v(-138.3, -2.27) * mm});
            skLineSegment(sketch, "E1190", {"start": v(-138.3, -2.27) * mm, "end": v(-137.53, -0.63) * mm});
            skLineSegment(sketch, "E1191", {"start": v(-137.53, -0.63) * mm, "end": v(-136.46, 2.7) * mm});
            skLineSegment(sketch, "E1192", {"start": v(-136.46, 2.7) * mm, "end": v(-135.5, 5.6) * mm});
            skLineSegment(sketch, "E1193", {"start": v(-135.5, 5.6) * mm, "end": v(-135.11, 7.08) * mm});
            skLineSegment(sketch, "E1194", {"start": v(-135.11, 7.08) * mm, "end": v(-134.52, 10.07) * mm});
            skLineSegment(sketch, "E1195", {"start": v(-134.52, 10.07) * mm, "end": v(-135.75, 11.14) * mm});
            skLineSegment(sketch, "E1196", {"start": v(-135.75, 11.14) * mm, "end": v(-136.6, 11.54) * mm});
            skLineSegment(sketch, "E1197", {"start": v(-136.6, 11.54) * mm, "end": v(-138.2, 11.82) * mm});
            skLineSegment(sketch, "E1198", {"start": v(-138.2, 11.82) * mm, "end": v(-138.9, 11.97) * mm});
            skLineSegment(sketch, "E1199", {"start": v(-138.9, 11.97) * mm, "end": v(-139.38, 11.87) * mm});
            skLineSegment(sketch, "E1200", {"start": v(-139.38, 11.87) * mm, "end": v(-139.95, 11.43) * mm});
            skLineSegment(sketch, "E1201", {"start": v(-139.95, 11.43) * mm, "end": v(-141.08, 7.7) * mm});
            skLineSegment(sketch, "E1202", {"start": v(-141.08, 7.7) * mm, "end": v(-141.66, 5.84) * mm});
            skLineSegment(sketch, "E1203", {"start": v(-141.66, 5.84) * mm, "end": v(-142.86, 2.12) * mm});
            skLineSegment(sketch, "E1204", {"start": v(-142.86, 2.12) * mm, "end": v(-143.79, 0.26) * mm});
            skLineSegment(sketch, "E1205", {"start": v(-143.79, 0.26) * mm, "end": v(-144.25, -0.67) * mm});
            skLineSegment(sketch, "E1206", {"start": v(-144.25, -0.67) * mm, "end": v(-145.19, -2.53) * mm});
            skLineSegment(sketch, "E1207", {"start": v(-145.19, -2.53) * mm, "end": v(-146.07, -3.54) * mm});
            skLineSegment(sketch, "E1208", {"start": v(-146.07, -3.54) * mm, "end": v(-146.47, -4.1) * mm});
            skLineSegment(sketch, "E1209", {"start": v(-146.47, -4.1) * mm, "end": v(-147.13, -5.25) * mm});
            skLineSegment(sketch, "E1210", {"start": v(-147.13, -5.25) * mm, "end": v(-148.52, -6.65) * mm});
            skLineSegment(sketch, "E1211", {"start": v(-148.52, -6.65) * mm, "end": v(-149.22, -7.35) * mm});
            skLineSegment(sketch, "E1212", {"start": v(-149.22, -7.35) * mm, "end": v(-150.62, -8.74) * mm});
            skLineSegment(sketch, "E1213", {"start": v(-150.62, -8.74) * mm, "end": v(-153.27, -11.61) * mm});
            skLineSegment(sketch, "E1214", {"start": v(-153.27, -11.61) * mm, "end": v(-154.55, -13.09) * mm});
            skLineSegment(sketch, "E1215", {"start": v(-154.55, -13.09) * mm, "end": v(-157.02, -16.11) * mm});
            skLineSegment(sketch, "E1216", {"start": v(-157.02, -16.11) * mm, "end": v(-157.1, -16.54) * mm});
            skLineSegment(sketch, "E1217", {"start": v(-157.1, -16.54) * mm, "end": v(-157.37, -16.8) * mm});
            skLineSegment(sketch, "E1218", {"start": v(-157.37, -16.8) * mm, "end": v(-157.8, -16.89) * mm});
            skLineSegment(sketch, "E1219", {"start": v(-157.8, -16.89) * mm, "end": v(-158.14, -17.92) * mm});
            skLineSegment(sketch, "E1220", {"start": v(-158.14, -17.92) * mm, "end": v(-158.19, -18.53) * mm});
            skLineSegment(sketch, "E1221", {"start": v(-158.19, -18.53) * mm, "end": v(-157.99, -19.6) * mm});
            skLineSegment(sketch, "E1222", {"start": v(-157.99, -19.6) * mm, "end": v(-157.52, -20.07) * mm});
            skLineSegment(sketch, "E1223", {"start": v(-157.52, -20.07) * mm, "end": v(-157.3, -20.3) * mm});
            skLineSegment(sketch, "E1224", {"start": v(-157.3, -20.3) * mm, "end": v(-156.83, -20.77) * mm});
            skLineSegment(sketch, "E1225", {"start": v(-156.63, -19.22) * mm, "end": v(-155.07, -19.18) * mm});
            skLineSegment(sketch, "E1226", {"start": v(-155.07, -19.18) * mm, "end": v(-154.11, -18.7) * mm});
            skLineSegment(sketch, "E1227", {"start": v(-154.11, -18.7) * mm, "end": v(-153.14, -17.47) * mm});
            skLineSegment(sketch, "E1228", {"start": v(-153.14, -17.47) * mm, "end": v(-152.65, -16.87) * mm});
            skLineSegment(sketch, "E1229", {"start": v(-152.65, -16.87) * mm, "end": v(-152.3, -16.61) * mm});
            skLineSegment(sketch, "E1230", {"start": v(-152.3, -16.61) * mm, "end": v(-151.59, -16.3) * mm});
            skLineSegment(sketch, "E1231", {"start": v(-151.59, -16.3) * mm, "end": v(-148.87, -13.6) * mm});
            skLineSegment(sketch, "E1232", {"start": v(-148.87, -13.6) * mm, "end": v(-147.51, -12.23) * mm});
            skLineSegment(sketch, "E1233", {"start": v(-147.51, -12.23) * mm, "end": v(-144.8, -9.52) * mm});
            skLineSegment(sketch, "E1234", {"start": v(-144.8, -9.52) * mm, "end": v(-142.66, -6.93) * mm});
            skLineSegment(sketch, "E1235", {"start": v(-142.66, -6.93) * mm, "end": v(-141.7, -5.5) * mm});
            skLineSegment(sketch, "E1236", {"start": v(-141.7, -5.5) * mm, "end": v(-140.14, -2.53) * mm});
            skLineSegment(sketch, "E1237", {"start": v(-140.14, -2.53) * mm, "end": v(-139.52, -1.3) * mm});
            skLineSegment(sketch, "E1238", {"start": v(-139.52, -1.3) * mm, "end": v(-139.21, -0.67) * mm});
            skLineSegment(sketch, "E1239", {"start": v(-139.21, -0.67) * mm, "end": v(-138.6, 0.57) * mm});
            skLineSegment(sketch, "E1240", {"start": v(-138.6, 0.57) * mm, "end": v(-137.97, 2.43) * mm});
            skLineSegment(sketch, "E1241", {"start": v(-137.97, 2.43) * mm, "end": v(-137.66, 3.36) * mm});
            skLineSegment(sketch, "E1242", {"start": v(-137.66, 3.36) * mm, "end": v(-137.04, 5.23) * mm});
            skLineSegment(sketch, "E1243", {"start": v(-137.04, 5.23) * mm, "end": v(-136.99, 6.38) * mm});
            skLineSegment(sketch, "E1244", {"start": v(-136.99, 6.38) * mm, "end": v(-136.76, 7.02) * mm});
            skLineSegment(sketch, "E1245", {"start": v(-136.76, 7.02) * mm, "end": v(-136.07, 7.94) * mm});
            skLineSegment(sketch, "E1246", {"start": v(-136.07, 7.94) * mm, "end": v(-136.07, 8.72) * mm});
            skLineSegment(sketch, "E1247", {"start": v(-136.07, 8.72) * mm, "end": v(-136.07, 9.1) * mm});
            skLineSegment(sketch, "E1248", {"start": v(-136.07, 9.1) * mm, "end": v(-136.07, 9.88) * mm});
            skLineSegment(sketch, "E1249", {"start": v(-136.07, 9.88) * mm, "end": v(-137.3, 10.15) * mm});
            skLineSegment(sketch, "E1250", {"start": v(-137.3, 10.15) * mm, "end": v(-137.92, 10.23) * mm});
            skLineSegment(sketch, "E1251", {"start": v(-137.92, 10.23) * mm, "end": v(-139.17, 10.27) * mm});
            skLineSegment(sketch, "E1252", {"start": v(-139.17, 10.27) * mm, "end": v(-139.34, 8.68) * mm});
            skLineSegment(sketch, "E1253", {"start": v(-139.34, 8.68) * mm, "end": v(-139.55, 7.87) * mm});
            skLineSegment(sketch, "E1254", {"start": v(-139.55, 7.87) * mm, "end": v(-140.14, 6.39) * mm});
            skLineSegment(sketch, "E1255", {"start": v(-140.14, 6.39) * mm, "end": v(-140.9, 3.23) * mm});
            skLineSegment(sketch, "E1256", {"start": v(-140.9, 3.23) * mm, "end": v(-141.5, 1.67) * mm});
            skLineSegment(sketch, "E1257", {"start": v(-141.5, 1.67) * mm, "end": v(-143.05, -1.18) * mm});
            skLineSegment(sketch, "E1258", {"start": v(-143.05, -1.18) * mm, "end": v(-143.8, -2.56) * mm});
            skLineSegment(sketch, "E1259", {"start": v(-143.8, -2.56) * mm, "end": v(-144.24, -3.22) * mm});
            skLineSegment(sketch, "E1260", {"start": v(-144.24, -3.22) * mm, "end": v(-145.19, -4.47) * mm});
            skLineSegment(sketch, "E1261", {"start": v(-145.19, -4.47) * mm, "end": v(-145.97, -5.56) * mm});
            skLineSegment(sketch, "E1262", {"start": v(-145.97, -5.56) * mm, "end": v(-146.36, -6.1) * mm});
            skLineSegment(sketch, "E1263", {"start": v(-146.36, -6.1) * mm, "end": v(-147.13, -7.2) * mm});
            skLineSegment(sketch, "E1264", {"start": v(-147.13, -7.2) * mm, "end": v(-150.23, -10.3) * mm});
            skLineSegment(sketch, "E1265", {"start": v(-150.23, -10.3) * mm, "end": v(-151.78, -11.85) * mm});
            skLineSegment(sketch, "E1266", {"start": v(-151.78, -11.85) * mm, "end": v(-154.89, -14.95) * mm});
            skLineSegment(sketch, "E1267", {"start": v(-154.89, -14.95) * mm, "end": v(-155.9, -16.35) * mm});
            skLineSegment(sketch, "E1268", {"start": v(-155.9, -16.35) * mm, "end": v(-156.31, -17.17) * mm});
            skLineSegment(sketch, "E1269", {"start": v(-156.31, -17.17) * mm, "end": v(-156.83, -18.83) * mm});
            skLineSegment(sketch, "E1270", {"start": v(-156.83, -18.83) * mm, "end": v(-156.67, -18.91) * mm});
            skLineSegment(sketch, "E1271", {"start": v(-156.67, -18.91) * mm, "end": v(-156.6, -19.05) * mm});
            skLineSegment(sketch, "E1272", {"start": v(-156.6, -19.05) * mm, "end": v(-156.63, -19.22) * mm});
            skLineSegment(sketch, "E1273", {"start": v(-171.96, -9.52) * mm, "end": v(-171.22, -9.21) * mm});
            skLineSegment(sketch, "E1274", {"start": v(-171.22, -9.21) * mm, "end": v(-170.86, -9.02) * mm});
            skLineSegment(sketch, "E1275", {"start": v(-170.86, -9.02) * mm, "end": v(-170.21, -8.55) * mm});
            skLineSegment(sketch, "E1276", {"start": v(-170.21, -8.55) * mm, "end": v(-167.98, -7.13) * mm});
            skLineSegment(sketch, "E1277", {"start": v(-167.98, -7.13) * mm, "end": v(-166.93, -6.25) * mm});
            skLineSegment(sketch, "E1278", {"start": v(-166.93, -6.25) * mm, "end": v(-165.17, -4.28) * mm});
            skLineSegment(sketch, "E1279", {"start": v(-165.17, -4.28) * mm, "end": v(-165.23, -4.04) * mm});
            skLineSegment(sketch, "E1280", {"start": v(-165.23, -4.04) * mm, "end": v(-165.17, -3.85) * mm});
            skLineSegment(sketch, "E1281", {"start": v(-165.17, -3.85) * mm, "end": v(-164.97, -3.7) * mm});
            skLineSegment(sketch, "E1282", {"start": v(-164.97, -3.7) * mm, "end": v(-163.11, -1.84) * mm});
            skLineSegment(sketch, "E1283", {"start": v(-163.11, -1.84) * mm, "end": v(-162.18, -0.9) * mm});
            skLineSegment(sketch, "E1284", {"start": v(-162.18, -0.9) * mm, "end": v(-160.32, 0.96) * mm});
            skLineSegment(sketch, "E1285", {"start": v(-160.32, 0.96) * mm, "end": v(-158.75, 3.12) * mm});
            skLineSegment(sketch, "E1286", {"start": v(-158.75, 3.12) * mm, "end": v(-157.97, 4.2) * mm});
            skLineSegment(sketch, "E1287", {"start": v(-157.97, 4.2) * mm, "end": v(-156.44, 6.39) * mm});
            skLineSegment(sketch, "E1288", {"start": v(-156.44, 6.39) * mm, "end": v(-155.66, 7.94) * mm});
            skLineSegment(sketch, "E1289", {"start": v(-155.66, 7.94) * mm, "end": v(-155.27, 8.72) * mm});
            skLineSegment(sketch, "E1290", {"start": v(-155.27, 8.72) * mm, "end": v(-154.5, 10.27) * mm});
            skLineSegment(sketch, "E1291", {"start": v(-154.5, 10.27) * mm, "end": v(-153.86, 11.97) * mm});
            skLineSegment(sketch, "E1292", {"start": v(-153.86, 11.97) * mm, "end": v(-153.55, 12.82) * mm});
            skLineSegment(sketch, "E1293", {"start": v(-153.55, 12.82) * mm, "end": v(-152.95, 14.54) * mm});
            skLineSegment(sketch, "E1294", {"start": v(-152.95, 14.54) * mm, "end": v(-152.25, 17.33) * mm});
            skLineSegment(sketch, "E1295", {"start": v(-152.25, 17.33) * mm, "end": v(-151.9, 18.73) * mm});
            skLineSegment(sketch, "E1296", {"start": v(-151.9, 18.73) * mm, "end": v(-151.2, 21.52) * mm});
            skLineSegment(sketch, "E1297", {"start": v(-151.2, 21.52) * mm, "end": v(-151.24, 22.3) * mm});
            skLineSegment(sketch, "E1298", {"start": v(-151.24, 22.3) * mm, "end": v(-151.63, 22.82) * mm});
            skLineSegment(sketch, "E1299", {"start": v(-151.63, 22.82) * mm, "end": v(-152.36, 23.07) * mm});
            skLineSegment(sketch, "E1300", {"start": v(-152.36, 23.07) * mm, "end": v(-153.82, 23.66) * mm});
            skLineSegment(sketch, "E1301", {"start": v(-153.82, 23.66) * mm, "end": v(-154.68, 23.8) * mm});
            skLineSegment(sketch, "E1302", {"start": v(-154.68, 23.8) * mm, "end": v(-156.24, 23.65) * mm});
            skLineSegment(sketch, "E1303", {"start": v(-156.24, 23.65) * mm, "end": v(-157, 22.66) * mm});
            skLineSegment(sketch, "E1304", {"start": v(-157, 22.66) * mm, "end": v(-157.27, 22) * mm});
            skLineSegment(sketch, "E1305", {"start": v(-157.27, 22) * mm, "end": v(-157.4, 20.74) * mm});
            skLineSegment(sketch, "E1306", {"start": v(-157.4, 20.74) * mm, "end": v(-158.34, 16.25) * mm});
            skLineSegment(sketch, "E1307", {"start": v(-158.34, 16.25) * mm, "end": v(-159.1, 14.01) * mm});
            skLineSegment(sketch, "E1308", {"start": v(-159.1, 14.01) * mm, "end": v(-161.1, 9.88) * mm});
            skLineSegment(sketch, "E1309", {"start": v(-161.1, 9.88) * mm, "end": v(-162.7, 7.1) * mm});
            skLineSegment(sketch, "E1310", {"start": v(-162.7, 7.1) * mm, "end": v(-163.7, 5.79) * mm});
            skLineSegment(sketch, "E1311", {"start": v(-163.7, 5.79) * mm, "end": v(-165.94, 3.48) * mm});
            skLineSegment(sketch, "E1312", {"start": v(-165.94, 3.48) * mm, "end": v(-166.63, 2.92) * mm});
            skLineSegment(sketch, "E1313", {"start": v(-166.63, 2.92) * mm, "end": v(-166.93, 2.54) * mm});
            skLineSegment(sketch, "E1314", {"start": v(-166.93, 2.54) * mm, "end": v(-167.3, 1.73) * mm});
            skLineSegment(sketch, "E1315", {"start": v(-167.3, 1.73) * mm, "end": v(-168.7, 0.34) * mm});
            skLineSegment(sketch, "E1316", {"start": v(-168.7, 0.34) * mm, "end": v(-169.4, -0.36) * mm});
            skLineSegment(sketch, "E1317", {"start": v(-169.4, -0.36) * mm, "end": v(-170.8, -1.76) * mm});
            skLineSegment(sketch, "E1318", {"start": v(-170.8, -1.76) * mm, "end": v(-172.1, -3.53) * mm});
            skLineSegment(sketch, "E1319", {"start": v(-172.1, -3.53) * mm, "end": v(-172.68, -4.47) * mm});
            skLineSegment(sketch, "E1320", {"start": v(-172.68, -4.47) * mm, "end": v(-173.7, -6.41) * mm});
            skLineSegment(sketch, "E1321", {"start": v(-173.7, -6.41) * mm, "end": v(-173.88, -7.5) * mm});
            skLineSegment(sketch, "E1322", {"start": v(-173.88, -7.5) * mm, "end": v(-173.8, -8.14) * mm});
            skLineSegment(sketch, "E1323", {"start": v(-173.8, -8.14) * mm, "end": v(-173.31, -9.13) * mm});
            skLineSegment(sketch, "E1324", {"start": v(-173.31, -9.13) * mm, "end": v(-172.78, -8.94) * mm});
            skLineSegment(sketch, "E1325", {"start": v(-172.78, -8.94) * mm, "end": v(-172.31, -9.08) * mm});
            skLineSegment(sketch, "E1326", {"start": v(-172.31, -9.08) * mm, "end": v(-171.96, -9.52) * mm});
            skLineSegment(sketch, "E1327", {"start": v(-172.73, -7.97) * mm, "end": v(-171.5, -7.94) * mm});
            skLineSegment(sketch, "E1328", {"start": v(-171.5, -7.94) * mm, "end": v(-170.82, -7.71) * mm});
            skLineSegment(sketch, "E1329", {"start": v(-170.82, -7.71) * mm, "end": v(-169.82, -7) * mm});
            skLineSegment(sketch, "E1330", {"start": v(-169.82, -7) * mm, "end": v(-166.95, -4.13) * mm});
            skLineSegment(sketch, "E1331", {"start": v(-166.95, -4.13) * mm, "end": v(-165.52, -2.69) * mm});
            skLineSegment(sketch, "E1332", {"start": v(-165.52, -2.69) * mm, "end": v(-162.65, 0.18) * mm});
            skLineSegment(sketch, "E1333", {"start": v(-162.65, 0.18) * mm, "end": v(-161.02, 2.48) * mm});
            skLineSegment(sketch, "E1334", {"start": v(-161.02, 2.48) * mm, "end": v(-160.12, 3.58) * mm});
            skLineSegment(sketch, "E1335", {"start": v(-160.12, 3.58) * mm, "end": v(-158.18, 5.61) * mm});
            skLineSegment(sketch, "E1336", {"start": v(-158.18, 5.61) * mm, "end": v(-156.2, 9.33) * mm});
            skLineSegment(sketch, "E1337", {"start": v(-156.2, 9.33) * mm, "end": v(-155.38, 11.3) * mm});
            skLineSegment(sketch, "E1338", {"start": v(-155.38, 11.3) * mm, "end": v(-154.1, 15.31) * mm});
            skLineSegment(sketch, "E1339", {"start": v(-154.1, 15.31) * mm, "end": v(-153.64, 17.17) * mm});
            skLineSegment(sketch, "E1340", {"start": v(-153.64, 17.17) * mm, "end": v(-153.41, 18.1) * mm});
            skLineSegment(sketch, "E1341", {"start": v(-153.41, 18.1) * mm, "end": v(-152.95, 19.97) * mm});
            skLineSegment(sketch, "E1342", {"start": v(-152.95, 19.97) * mm, "end": v(-152.73, 20.72) * mm});
            skLineSegment(sketch, "E1343", {"start": v(-152.73, 20.72) * mm, "end": v(-152.69, 21.13) * mm});
            skLineSegment(sketch, "E1344", {"start": v(-152.69, 21.13) * mm, "end": v(-152.75, 21.9) * mm});
            skLineSegment(sketch, "E1345", {"start": v(-152.75, 21.9) * mm, "end": v(-153.78, 22.27) * mm});
            skLineSegment(sketch, "E1346", {"start": v(-153.78, 22.27) * mm, "end": v(-154.4, 22.32) * mm});
            skLineSegment(sketch, "E1347", {"start": v(-154.4, 22.32) * mm, "end": v(-155.47, 22.1) * mm});
            skLineSegment(sketch, "E1348", {"start": v(-155.47, 22.1) * mm, "end": v(-156.22, 19.84) * mm});
            skLineSegment(sketch, "E1349", {"start": v(-156.22, 19.84) * mm, "end": v(-156.6, 18.72) * mm});
            skLineSegment(sketch, "E1350", {"start": v(-156.6, 18.72) * mm, "end": v(-157.4, 16.48) * mm});
            skLineSegment(sketch, "E1351", {"start": v(-157.4, 16.48) * mm, "end": v(-157.36, 15.37) * mm});
            skLineSegment(sketch, "E1352", {"start": v(-157.36, 15.37) * mm, "end": v(-157.49, 14.75) * mm});
            skLineSegment(sketch, "E1353", {"start": v(-157.49, 14.75) * mm, "end": v(-157.99, 13.76) * mm});
            skLineSegment(sketch, "E1354", {"start": v(-157.99, 13.76) * mm, "end": v(-159.02, 10.96) * mm});
            skLineSegment(sketch, "E1355", {"start": v(-159.02, 10.96) * mm, "end": v(-159.74, 9.6) * mm});
            skLineSegment(sketch, "E1356", {"start": v(-159.74, 9.6) * mm, "end": v(-161.48, 7.16) * mm});
            skLineSegment(sketch, "E1357", {"start": v(-161.48, 7.16) * mm, "end": v(-163.52, 4.02) * mm});
            skLineSegment(sketch, "E1358", {"start": v(-163.52, 4.02) * mm, "end": v(-164.76, 2.54) * mm});
            skLineSegment(sketch, "E1359", {"start": v(-164.76, 2.54) * mm, "end": v(-167.5, -0.01) * mm});
            skLineSegment(sketch, "E1360", {"start": v(-167.5, -0.01) * mm, "end": v(-168.88, -1.93) * mm});
            skLineSegment(sketch, "E1361", {"start": v(-168.88, -1.93) * mm, "end": v(-169.67, -2.84) * mm});
            skLineSegment(sketch, "E1362", {"start": v(-169.67, -2.84) * mm, "end": v(-171.37, -4.47) * mm});
            skLineSegment(sketch, "E1363", {"start": v(-171.37, -4.47) * mm, "end": v(-171.92, -5.87) * mm});
            skLineSegment(sketch, "E1364", {"start": v(-171.92, -5.87) * mm, "end": v(-172.2, -6.57) * mm});
            skLineSegment(sketch, "E1365", {"start": v(-172.2, -6.57) * mm, "end": v(-172.73, -7.97) * mm});
            skLineSegment(sketch, "E1366", {"start": v(-21.23, 54.11) * mm, "end": v(-20.12, 54.06) * mm});
            skLineSegment(sketch, "E1367", {"start": v(-20.12, 54.06) * mm, "end": v(-19.5, 54.2) * mm});
            skLineSegment(sketch, "E1368", {"start": v(-19.5, 54.2) * mm, "end": v(-18.51, 54.7) * mm});
            skLineSegment(sketch, "E1369", {"start": v(-18.51, 54.7) * mm, "end": v(-17.29, 55.43) * mm});
            skLineSegment(sketch, "E1370", {"start": v(-17.29, 55.43) * mm, "end": v(-16.72, 55.92) * mm});
            skLineSegment(sketch, "E1371", {"start": v(-16.72, 55.92) * mm, "end": v(-15.8, 57.02) * mm});
            skLineSegment(sketch, "E1372", {"start": v(-15.8, 57.02) * mm, "end": v(-15.23, 58.55) * mm});
            skLineSegment(sketch, "E1373", {"start": v(-15.23, 58.55) * mm, "end": v(-15.18, 59.52) * mm});
            skLineSegment(sketch, "E1374", {"start": v(-15.18, 59.52) * mm, "end": v(-15.6, 61.1) * mm});
            skLineSegment(sketch, "E1375", {"start": v(-15.6, 61.1) * mm, "end": v(-16.6, 63.24) * mm});
            skLineSegment(sketch, "E1376", {"start": v(-16.6, 63.24) * mm, "end": v(-17.07, 64.32) * mm});
            skLineSegment(sketch, "E1377", {"start": v(-17.07, 64.32) * mm, "end": v(-17.93, 66.53) * mm});
            skLineSegment(sketch, "E1378", {"start": v(-17.93, 66.53) * mm, "end": v(-18.86, 68.39) * mm});
            skLineSegment(sketch, "E1379", {"start": v(-18.86, 68.39) * mm, "end": v(-19.33, 69.32) * mm});
            skLineSegment(sketch, "E1380", {"start": v(-19.33, 69.32) * mm, "end": v(-20.26, 71.18) * mm});
            skLineSegment(sketch, "E1381", {"start": v(-20.26, 71.18) * mm, "end": v(-20.41, 71.65) * mm});
            skLineSegment(sketch, "E1382", {"start": v(-20.41, 71.65) * mm, "end": v(-20.5, 71.88) * mm});
            skLineSegment(sketch, "E1383", {"start": v(-20.5, 71.88) * mm, "end": v(-20.65, 72.35) * mm});
            skLineSegment(sketch, "E1384", {"start": v(-20.65, 72.35) * mm, "end": v(-22.35, 75.76) * mm});
            skLineSegment(sketch, "E1385", {"start": v(-22.35, 75.76) * mm, "end": v(-23.2, 77.47) * mm});
            skLineSegment(sketch, "E1386", {"start": v(-23.2, 77.47) * mm, "end": v(-24.91, 80.88) * mm});
            skLineSegment(sketch, "E1387", {"start": v(-24.91, 80.88) * mm, "end": v(-25.07, 81.04) * mm});
            skLineSegment(sketch, "E1388", {"start": v(-25.07, 81.04) * mm, "end": v(-25.15, 81.11) * mm});
            skLineSegment(sketch, "E1389", {"start": v(-25.15, 81.11) * mm, "end": v(-25.3, 81.27) * mm});
            skLineSegment(sketch, "E1390", {"start": v(-25.3, 81.27) * mm, "end": v(-26.39, 83.44) * mm});
            skLineSegment(sketch, "E1391", {"start": v(-26.39, 83.44) * mm, "end": v(-26.93, 84.53) * mm});
            skLineSegment(sketch, "E1392", {"start": v(-26.93, 84.53) * mm, "end": v(-28.02, 86.7) * mm});
            skLineSegment(sketch, "E1393", {"start": v(-28.02, 86.7) * mm, "end": v(-31.5, 93.28) * mm});
            skLineSegment(sketch, "E1394", {"start": v(-31.5, 93.28) * mm, "end": v(-33.46, 96.49) * mm});
            skLineSegment(sketch, "E1395", {"start": v(-33.46, 96.49) * mm, "end": v(-37.72, 102.6) * mm});
            skLineSegment(sketch, "E1396", {"start": v(-37.72, 102.6) * mm, "end": v(-38.43, 103.2) * mm});
            skLineSegment(sketch, "E1397", {"start": v(-38.43, 103.2) * mm, "end": v(-38.78, 103.52) * mm});
            skLineSegment(sketch, "E1398", {"start": v(-38.78, 103.52) * mm, "end": v(-39.46, 104.16) * mm});
            skLineSegment(sketch, "E1399", {"start": v(-39.46, 104.16) * mm, "end": v(-41, 104.38) * mm});
            skLineSegment(sketch, "E1400", {"start": v(-41, 104.38) * mm, "end": v(-41.87, 104.29) * mm});
            skLineSegment(sketch, "E1401", {"start": v(-41.87, 104.29) * mm, "end": v(-43.34, 103.77) * mm});
            skLineSegment(sketch, "E1402", {"start": v(-43.34, 103.77) * mm, "end": v(-45.06, 102.77) * mm});
            skLineSegment(sketch, "E1403", {"start": v(-45.06, 102.77) * mm, "end": v(-45.87, 102.12) * mm});
            skLineSegment(sketch, "E1404", {"start": v(-45.87, 102.12) * mm, "end": v(-47.22, 100.67) * mm});
            skLineSegment(sketch, "E1405", {"start": v(-47.22, 100.67) * mm, "end": v(-48.18, 100.75) * mm});
            skLineSegment(sketch, "E1406", {"start": v(-48.18, 100.75) * mm, "end": v(-48.74, 100.6) * mm});
            skLineSegment(sketch, "E1407", {"start": v(-48.74, 100.6) * mm, "end": v(-49.55, 100.09) * mm});
            skLineSegment(sketch, "E1408", {"start": v(-49.55, 100.09) * mm, "end": v(-50.77, 99.03) * mm});
            skLineSegment(sketch, "E1409", {"start": v(-50.77, 99.03) * mm, "end": v(-51.29, 98.3) * mm});
            skLineSegment(sketch, "E1410", {"start": v(-51.29, 98.3) * mm, "end": v(-51.88, 96.79) * mm});
            skLineSegment(sketch, "E1411", {"start": v(-51.88, 96.79) * mm, "end": v(-52.08, 95.39) * mm});
            skLineSegment(sketch, "E1412", {"start": v(-52.08, 95.39) * mm, "end": v(-51.94, 94.56) * mm});
            skLineSegment(sketch, "E1413", {"start": v(-51.94, 94.56) * mm, "end": v(-51.3, 93.3) * mm});
            skLineSegment(sketch, "E1414", {"start": v(-51.3, 93.3) * mm, "end": v(-50.79, 92.3) * mm});
            skLineSegment(sketch, "E1415", {"start": v(-50.79, 92.3) * mm, "end": v(-50.47, 91.82) * mm});
            skLineSegment(sketch, "E1416", {"start": v(-50.47, 91.82) * mm, "end": v(-49.74, 90.97) * mm});
            skLineSegment(sketch, "E1417", {"start": v(-49.74, 90.97) * mm, "end": v(-49.24, 89.97) * mm});
            skLineSegment(sketch, "E1418", {"start": v(-49.24, 89.97) * mm, "end": v(-48.92, 89.5) * mm});
            skLineSegment(sketch, "E1419", {"start": v(-48.92, 89.5) * mm, "end": v(-48.2, 88.64) * mm});
            skLineSegment(sketch, "E1420", {"start": v(-48.2, 88.64) * mm, "end": v(-47.69, 87.64) * mm});
            skLineSegment(sketch, "E1421", {"start": v(-47.69, 87.64) * mm, "end": v(-47.37, 87.16) * mm});
            skLineSegment(sketch, "E1422", {"start": v(-47.37, 87.16) * mm, "end": v(-46.64, 86.31) * mm});
            skLineSegment(sketch, "E1423", {"start": v(-46.64, 86.31) * mm, "end": v(-46.03, 85.07) * mm});
            skLineSegment(sketch, "E1424", {"start": v(-46.03, 85.07) * mm, "end": v(-45.57, 84.48) * mm});
            skLineSegment(sketch, "E1425", {"start": v(-45.57, 84.48) * mm, "end": v(-44.5, 83.6) * mm});
            skLineSegment(sketch, "E1426", {"start": v(-44.5, 83.6) * mm, "end": v(-44.6, 83.08) * mm});
            skLineSegment(sketch, "E1427", {"start": v(-44.6, 83.08) * mm, "end": v(-44.39, 82.67) * mm});
            skLineSegment(sketch, "E1428", {"start": v(-44.39, 82.67) * mm, "end": v(-43.92, 82.43) * mm});
            skLineSegment(sketch, "E1429", {"start": v(-43.92, 82.43) * mm, "end": v(-43.31, 81.2) * mm});
            skLineSegment(sketch, "E1430", {"start": v(-43.31, 81.2) * mm, "end": v(-42.85, 80.6) * mm});
            skLineSegment(sketch, "E1431", {"start": v(-42.85, 80.6) * mm, "end": v(-41.8, 79.72) * mm});
            skLineSegment(sketch, "E1432", {"start": v(-41.8, 79.72) * mm, "end": v(-41.88, 79.2) * mm});
            skLineSegment(sketch, "E1433", {"start": v(-41.88, 79.2) * mm, "end": v(-41.67, 78.79) * mm});
            skLineSegment(sketch, "E1434", {"start": v(-41.67, 78.79) * mm, "end": v(-41.2, 78.55) * mm});
            skLineSegment(sketch, "E1435", {"start": v(-41.2, 78.55) * mm, "end": v(-35.07, 69.6) * mm});
            skLineSegment(sketch, "E1436", {"start": v(-35.07, 69.6) * mm, "end": v(-31.8, 65.23) * mm});
            skLineSegment(sketch, "E1437", {"start": v(-31.8, 65.23) * mm, "end": v(-24.91, 56.83) * mm});
            skLineSegment(sketch, "E1438", {"start": v(-24.91, 56.83) * mm, "end": v(-24.48, 55.76) * mm});
            skLineSegment(sketch, "E1439", {"start": v(-24.48, 55.76) * mm, "end": v(-23.88, 55.22) * mm});
            skLineSegment(sketch, "E1440", {"start": v(-23.88, 55.22) * mm, "end": v(-22.78, 54.89) * mm});
            skLineSegment(sketch, "E1441", {"start": v(-22.78, 54.89) * mm, "end": v(-22.1, 54.78) * mm});
            skLineSegment(sketch, "E1442", {"start": v(-22.1, 54.78) * mm, "end": v(-21.72, 54.6) * mm});
            skLineSegment(sketch, "E1443", {"start": v(-21.72, 54.6) * mm, "end": v(-21.23, 54.11) * mm});
            skLineSegment(sketch, "E1444", {"start": v(-22, 55.66) * mm, "end": v(-20.53, 55.5) * mm});
            skLineSegment(sketch, "E1445", {"start": v(-20.53, 55.5) * mm, "end": v(-19.73, 55.59) * mm});
            skLineSegment(sketch, "E1446", {"start": v(-19.73, 55.59) * mm, "end": v(-18.32, 56.05) * mm});
            skLineSegment(sketch, "E1447", {"start": v(-18.32, 56.05) * mm, "end": v(-17.4, 56.96) * mm});
            skLineSegment(sketch, "E1448", {"start": v(-17.4, 56.96) * mm, "end": v(-17.03, 57.56) * mm});
            skLineSegment(sketch, "E1449", {"start": v(-17.03, 57.56) * mm, "end": v(-16.57, 58.77) * mm});
            skLineSegment(sketch, "E1450", {"start": v(-16.57, 58.77) * mm, "end": v(-16.52, 59.88) * mm});
            skLineSegment(sketch, "E1451", {"start": v(-16.52, 59.88) * mm, "end": v(-16.65, 60.5) * mm});
            skLineSegment(sketch, "E1452", {"start": v(-16.65, 60.5) * mm, "end": v(-17.15, 61.48) * mm});
            skLineSegment(sketch, "E1453", {"start": v(-17.15, 61.48) * mm, "end": v(-18.26, 63.96) * mm});
            skLineSegment(sketch, "E1454", {"start": v(-18.26, 63.96) * mm, "end": v(-18.8, 65.2) * mm});
            skLineSegment(sketch, "E1455", {"start": v(-18.8, 65.2) * mm, "end": v(-19.87, 67.69) * mm});
            skLineSegment(sketch, "E1456", {"start": v(-19.87, 67.69) * mm, "end": v(-23.28, 74.52) * mm});
            skLineSegment(sketch, "E1457", {"start": v(-23.28, 74.52) * mm, "end": v(-25, 77.93) * mm});
            skLineSegment(sketch, "E1458", {"start": v(-25, 77.93) * mm, "end": v(-28.4, 84.76) * mm});
            skLineSegment(sketch, "E1459", {"start": v(-28.4, 84.76) * mm, "end": v(-28.56, 84.92) * mm});
            skLineSegment(sketch, "E1460", {"start": v(-28.56, 84.92) * mm, "end": v(-28.64, 85) * mm});
            skLineSegment(sketch, "E1461", {"start": v(-28.64, 85) * mm, "end": v(-28.8, 85.15) * mm});
            skLineSegment(sketch, "E1462", {"start": v(-28.8, 85.15) * mm, "end": v(-29.57, 86.7) * mm});
            skLineSegment(sketch, "E1463", {"start": v(-29.57, 86.7) * mm, "end": v(-29.96, 87.48) * mm});
            skLineSegment(sketch, "E1464", {"start": v(-29.96, 87.48) * mm, "end": v(-30.73, 89.03) * mm});
            skLineSegment(sketch, "E1465", {"start": v(-30.73, 89.03) * mm, "end": v(-33.74, 94.57) * mm});
            skLineSegment(sketch, "E1466", {"start": v(-33.74, 94.57) * mm, "end": v(-35.42, 97.27) * mm});
            skLineSegment(sketch, "E1467", {"start": v(-35.42, 97.27) * mm, "end": v(-39.07, 102.41) * mm});
            skLineSegment(sketch, "E1468", {"start": v(-39.07, 102.41) * mm, "end": v(-40.22, 102.96) * mm});
            skLineSegment(sketch, "E1469", {"start": v(-40.22, 102.96) * mm, "end": v(-40.92, 103.09) * mm});
            skLineSegment(sketch, "E1470", {"start": v(-40.92, 103.09) * mm, "end": v(-42.18, 103) * mm});
            skLineSegment(sketch, "E1471", {"start": v(-42.18, 103) * mm, "end": v(-43.19, 102.68) * mm});
            skLineSegment(sketch, "E1472", {"start": v(-43.19, 102.68) * mm, "end": v(-43.7, 102.3) * mm});
            skLineSegment(sketch, "E1473", {"start": v(-43.7, 102.3) * mm, "end": v(-44.31, 101.44) * mm});
            skLineSegment(sketch, "E1474", {"start": v(-44.31, 101.44) * mm, "end": v(-46.3, 99.82) * mm});
            skLineSegment(sketch, "E1475", {"start": v(-46.3, 99.82) * mm, "end": v(-47.5, 99.16) * mm});
            skLineSegment(sketch, "E1476", {"start": v(-47.5, 99.16) * mm, "end": v(-49.94, 98.34) * mm});
            skLineSegment(sketch, "E1477", {"start": v(-49.94, 98.34) * mm, "end": v(-50.44, 97) * mm});
            skLineSegment(sketch, "E1478", {"start": v(-50.44, 97) * mm, "end": v(-50.6, 96.27) * mm});
            skLineSegment(sketch, "E1479", {"start": v(-50.6, 96.27) * mm, "end": v(-50.71, 94.85) * mm});
            skLineSegment(sketch, "E1480", {"start": v(-50.71, 94.85) * mm, "end": v(-50.23, 93.89) * mm});
            skLineSegment(sketch, "E1481", {"start": v(-50.23, 93.89) * mm, "end": v(-49.95, 93.42) * mm});
            skLineSegment(sketch, "E1482", {"start": v(-49.95, 93.42) * mm, "end": v(-49.36, 92.52) * mm});
            skLineSegment(sketch, "E1483", {"start": v(-49.36, 92.52) * mm, "end": v(-48.75, 91.28) * mm});
            skLineSegment(sketch, "E1484", {"start": v(-48.75, 91.28) * mm, "end": v(-48.28, 90.7) * mm});
            skLineSegment(sketch, "E1485", {"start": v(-48.28, 90.7) * mm, "end": v(-47.22, 89.8) * mm});
            skLineSegment(sketch, "E1486", {"start": v(-47.22, 89.8) * mm, "end": v(-47.31, 89.3) * mm});
            skLineSegment(sketch, "E1487", {"start": v(-47.31, 89.3) * mm, "end": v(-47.1, 88.88) * mm});
            skLineSegment(sketch, "E1488", {"start": v(-47.1, 88.88) * mm, "end": v(-46.64, 88.64) * mm});
            skLineSegment(sketch, "E1489", {"start": v(-46.64, 88.64) * mm, "end": v(-46.13, 87.64) * mm});
            skLineSegment(sketch, "E1490", {"start": v(-46.13, 87.64) * mm, "end": v(-45.81, 87.16) * mm});
            skLineSegment(sketch, "E1491", {"start": v(-45.81, 87.16) * mm, "end": v(-45.09, 86.31) * mm});
            skLineSegment(sketch, "E1492", {"start": v(-45.09, 86.31) * mm, "end": v(-44.2, 84.59) * mm});
            skLineSegment(sketch, "E1493", {"start": v(-44.2, 84.59) * mm, "end": v(-43.58, 83.77) * mm});
            skLineSegment(sketch, "E1494", {"start": v(-43.58, 83.77) * mm, "end": v(-42.18, 82.43) * mm});
            skLineSegment(sketch, "E1495", {"start": v(-42.18, 82.43) * mm, "end": v(-42.27, 81.92) * mm});
            skLineSegment(sketch, "E1496", {"start": v(-42.27, 81.92) * mm, "end": v(-42.06, 81.5) * mm});
            skLineSegment(sketch, "E1497", {"start": v(-42.06, 81.5) * mm, "end": v(-41.6, 81.27) * mm});
            skLineSegment(sketch, "E1498", {"start": v(-41.6, 81.27) * mm, "end": v(-38.84, 77.36) * mm});
            skLineSegment(sketch, "E1499", {"start": v(-38.84, 77.36) * mm, "end": v(-37.44, 75.42) * mm});
            skLineSegment(sketch, "E1500", {"start": v(-37.44, 75.42) * mm, "end": v(-34.61, 71.57) * mm});
            skLineSegment(sketch, "E1501", {"start": v(-34.61, 71.57) * mm, "end": v(-30.17, 65.1) * mm});
            skLineSegment(sketch, "E1502", {"start": v(-30.17, 65.1) * mm, "end": v(-27.75, 61.97) * mm});
            skLineSegment(sketch, "E1503", {"start": v(-27.75, 61.97) * mm, "end": v(-22.59, 56.05) * mm});
            skLineSegment(sketch, "E1504", {"start": v(-22.59, 56.05) * mm, "end": v(-22.32, 56.15) * mm});
            skLineSegment(sketch, "E1505", {"start": v(-22.32, 56.15) * mm, "end": v(-22, 55.94) * mm});
            skLineSegment(sketch, "E1506", {"start": v(-22, 55.94) * mm, "end": v(-22, 55.66) * mm});
            skLineSegment(sketch, "E1507", {"start": v(-56.15, 102.22) * mm, "end": v(-54.6, 102) * mm});
            skLineSegment(sketch, "E1508", {"start": v(-54.6, 102) * mm, "end": v(-53.74, 102.09) * mm});
            skLineSegment(sketch, "E1509", {"start": v(-53.74, 102.09) * mm, "end": v(-52.27, 102.6) * mm});
            skLineSegment(sketch, "E1510", {"start": v(-52.27, 102.6) * mm, "end": v(-51.2, 103.06) * mm});
            skLineSegment(sketch, "E1511", {"start": v(-51.2, 103.06) * mm, "end": v(-50.68, 103.45) * mm});
            skLineSegment(sketch, "E1512", {"start": v(-50.68, 103.45) * mm, "end": v(-49.94, 104.35) * mm});
            skLineSegment(sketch, "E1513", {"start": v(-49.94, 104.35) * mm, "end": v(-49.94, 104.59) * mm});
            skLineSegment(sketch, "E1514", {"start": v(-49.94, 104.59) * mm, "end": v(-49.94, 104.7) * mm});
            skLineSegment(sketch, "E1515", {"start": v(-49.94, 104.7) * mm, "end": v(-49.94, 104.94) * mm});
            skLineSegment(sketch, "E1516", {"start": v(-49.94, 104.94) * mm, "end": v(-49.42, 104.85) * mm});
            skLineSegment(sketch, "E1517", {"start": v(-49.42, 104.85) * mm, "end": v(-49.01, 105.05) * mm});
            skLineSegment(sketch, "E1518", {"start": v(-49.01, 105.05) * mm, "end": v(-48.77, 105.52) * mm});
            skLineSegment(sketch, "E1519", {"start": v(-48.77, 105.52) * mm, "end": v(-47.06, 105.8) * mm});
            skLineSegment(sketch, "E1520", {"start": v(-47.06, 105.8) * mm, "end": v(-46.14, 106.25) * mm});
            skLineSegment(sketch, "E1521", {"start": v(-46.14, 106.25) * mm, "end": v(-44.9, 107.46) * mm});
            skLineSegment(sketch, "E1522", {"start": v(-44.9, 107.46) * mm, "end": v(-44.35, 108.26) * mm});
            skLineSegment(sketch, "E1523", {"start": v(-44.35, 108.26) * mm, "end": v(-44.12, 108.7) * mm});
            skLineSegment(sketch, "E1524", {"start": v(-44.12, 108.7) * mm, "end": v(-43.73, 109.6) * mm});
            skLineSegment(sketch, "E1525", {"start": v(-43.73, 109.6) * mm, "end": v(-43.53, 111) * mm});
            skLineSegment(sketch, "E1526", {"start": v(-43.53, 111) * mm, "end": v(-43.67, 111.82) * mm});
            skLineSegment(sketch, "E1527", {"start": v(-43.67, 111.82) * mm, "end": v(-44.31, 113.08) * mm});
            skLineSegment(sketch, "E1528", {"start": v(-44.31, 113.08) * mm, "end": v(-44.82, 114.08) * mm});
            skLineSegment(sketch, "E1529", {"start": v(-44.82, 114.08) * mm, "end": v(-45.14, 114.56) * mm});
            skLineSegment(sketch, "E1530", {"start": v(-45.14, 114.56) * mm, "end": v(-45.86, 115.41) * mm});
            skLineSegment(sketch, "E1531", {"start": v(-45.86, 115.41) * mm, "end": v(-51.1, 123.11) * mm});
            skLineSegment(sketch, "E1532", {"start": v(-51.1, 123.11) * mm, "end": v(-53.9, 126.85) * mm});
            skLineSegment(sketch, "E1533", {"start": v(-53.9, 126.85) * mm, "end": v(-59.83, 134.03) * mm});
            skLineSegment(sketch, "E1534", {"start": v(-59.83, 134.03) * mm, "end": v(-65.05, 140.57) * mm});
            skLineSegment(sketch, "E1535", {"start": v(-65.05, 140.57) * mm, "end": v(-67.78, 143.76) * mm});
            skLineSegment(sketch, "E1536", {"start": v(-67.78, 143.76) * mm, "end": v(-73.41, 149.94) * mm});
            skLineSegment(sketch, "E1537", {"start": v(-73.41, 149.94) * mm, "end": v(-73.9, 149.88) * mm});
            skLineSegment(sketch, "E1538", {"start": v(-73.9, 149.88) * mm, "end": v(-74.33, 150.22) * mm});
            skLineSegment(sketch, "E1539", {"start": v(-74.33, 150.22) * mm, "end": v(-74.38, 150.72) * mm});
            skLineSegment(sketch, "E1540", {"start": v(-74.38, 150.72) * mm, "end": v(-75.86, 151.18) * mm});
            skLineSegment(sketch, "E1541", {"start": v(-75.86, 151.18) * mm, "end": v(-76.74, 151.22) * mm});
            skLineSegment(sketch, "E1542", {"start": v(-76.74, 151.22) * mm, "end": v(-78.26, 150.91) * mm});
            skLineSegment(sketch, "E1543", {"start": v(-78.26, 150.91) * mm, "end": v(-79.69, 150.3) * mm});
            skLineSegment(sketch, "E1544", {"start": v(-79.69, 150.3) * mm, "end": v(-80.38, 149.78) * mm});
            skLineSegment(sketch, "E1545", {"start": v(-80.38, 149.78) * mm, "end": v(-81.36, 148.58) * mm});
            skLineSegment(sketch, "E1546", {"start": v(-81.36, 148.58) * mm, "end": v(-81.88, 147.35) * mm});
            skLineSegment(sketch, "E1547", {"start": v(-81.88, 147.35) * mm, "end": v(-82.01, 146.62) * mm});
            skLineSegment(sketch, "E1548", {"start": v(-82.01, 146.62) * mm, "end": v(-81.95, 145.28) * mm});
            skLineSegment(sketch, "E1549", {"start": v(-81.95, 145.28) * mm, "end": v(-81.8, 144.82) * mm});
            skLineSegment(sketch, "E1550", {"start": v(-81.8, 144.82) * mm, "end": v(-81.71, 144.59) * mm});
            skLineSegment(sketch, "E1551", {"start": v(-81.71, 144.59) * mm, "end": v(-81.56, 144.12) * mm});
            skLineSegment(sketch, "E1552", {"start": v(-81.56, 144.12) * mm, "end": v(-80.32, 141.64) * mm});
            skLineSegment(sketch, "E1553", {"start": v(-80.32, 141.64) * mm, "end": v(-79.7, 140.4) * mm});
            skLineSegment(sketch, "E1554", {"start": v(-79.7, 140.4) * mm, "end": v(-78.45, 137.91) * mm});
            skLineSegment(sketch, "E1555", {"start": v(-78.45, 137.91) * mm, "end": v(-71.42, 125.75) * mm});
            skLineSegment(sketch, "E1556", {"start": v(-71.42, 125.75) * mm, "end": v(-67.85, 119.7) * mm});
            skLineSegment(sketch, "E1557", {"start": v(-67.85, 119.7) * mm, "end": v(-60.6, 107.65) * mm});
            skLineSegment(sketch, "E1558", {"start": v(-60.6, 107.65) * mm, "end": v(-59.63, 105.66) * mm});
            skLineSegment(sketch, "E1559", {"start": v(-59.63, 105.66) * mm, "end": v(-58.93, 104.7) * mm});
            skLineSegment(sketch, "E1560", {"start": v(-58.93, 104.7) * mm, "end": v(-57.3, 103.19) * mm});
            skLineSegment(sketch, "E1561", {"start": v(-57.3, 103.19) * mm, "end": v(-56.77, 102.9) * mm});
            skLineSegment(sketch, "E1562", {"start": v(-56.77, 102.9) * mm, "end": v(-56.52, 102.7) * mm});
            skLineSegment(sketch, "E1563", {"start": v(-56.52, 102.7) * mm, "end": v(-56.15, 102.22) * mm});
            skLineSegment(sketch, "E1564", {"start": v(-54.98, 103.38) * mm, "end": v(-53.87, 103.34) * mm});
            skLineSegment(sketch, "E1565", {"start": v(-53.87, 103.34) * mm, "end": v(-53.26, 103.47) * mm});
            skLineSegment(sketch, "E1566", {"start": v(-53.26, 103.47) * mm, "end": v(-52.27, 103.97) * mm});
            skLineSegment(sketch, "E1567", {"start": v(-52.27, 103.97) * mm, "end": v(-51.22, 105.24) * mm});
            skLineSegment(sketch, "E1568", {"start": v(-51.22, 105.24) * mm, "end": v(-50.57, 105.82) * mm});
            skLineSegment(sketch, "E1569", {"start": v(-50.57, 105.82) * mm, "end": v(-49.16, 106.68) * mm});
            skLineSegment(sketch, "E1570", {"start": v(-49.16, 106.68) * mm, "end": v(-47.8, 106.92) * mm});
            skLineSegment(sketch, "E1571", {"start": v(-47.8, 106.92) * mm, "end": v(-47.07, 107.28) * mm});
            skLineSegment(sketch, "E1572", {"start": v(-47.07, 107.28) * mm, "end": v(-46.06, 108.23) * mm});
            skLineSegment(sketch, "E1573", {"start": v(-46.06, 108.23) * mm, "end": v(-45.75, 108.54) * mm});
            skLineSegment(sketch, "E1574", {"start": v(-45.75, 108.54) * mm, "end": v(-45.6, 108.7) * mm});
            skLineSegment(sketch, "E1575", {"start": v(-45.6, 108.7) * mm, "end": v(-45.28, 109) * mm});
            skLineSegment(sketch, "E1576", {"start": v(-45.28, 109) * mm, "end": v(-44.9, 109.95) * mm});
            skLineSegment(sketch, "E1577", {"start": v(-44.9, 109.95) * mm, "end": v(-44.86, 110.55) * mm});
            skLineSegment(sketch, "E1578", {"start": v(-44.86, 110.55) * mm, "end": v(-45.09, 111.53) * mm});
            skLineSegment(sketch, "E1579", {"start": v(-45.09, 111.53) * mm, "end": v(-45.33, 112.65) * mm});
            skLineSegment(sketch, "E1580", {"start": v(-45.33, 112.65) * mm, "end": v(-45.64, 113.24) * mm});
            skLineSegment(sketch, "E1581", {"start": v(-45.64, 113.24) * mm, "end": v(-46.45, 114.05) * mm});
            skLineSegment(sketch, "E1582", {"start": v(-46.45, 114.05) * mm, "end": v(-47.82, 116.21) * mm});
            skLineSegment(sketch, "E1583", {"start": v(-47.82, 116.21) * mm, "end": v(-48.56, 117.27) * mm});
            skLineSegment(sketch, "E1584", {"start": v(-48.56, 117.27) * mm, "end": v(-50.13, 119.3) * mm});
            skLineSegment(sketch, "E1585", {"start": v(-50.13, 119.3) * mm, "end": v(-55.08, 126.36) * mm});
            skLineSegment(sketch, "E1586", {"start": v(-55.08, 126.36) * mm, "end": v(-57.73, 129.79) * mm});
            skLineSegment(sketch, "E1587", {"start": v(-57.73, 129.79) * mm, "end": v(-63.32, 136.36) * mm});
            skLineSegment(sketch, "E1588", {"start": v(-63.32, 136.36) * mm, "end": v(-67.5, 141.6) * mm});
            skLineSegment(sketch, "E1589", {"start": v(-67.5, 141.6) * mm, "end": v(-69.72, 144.14) * mm});
            skLineSegment(sketch, "E1590", {"start": v(-69.72, 144.14) * mm, "end": v(-74.38, 148.97) * mm});
            skLineSegment(sketch, "E1591", {"start": v(-74.38, 148.97) * mm, "end": v(-75.45, 149.72) * mm});
            skLineSegment(sketch, "E1592", {"start": v(-75.45, 149.72) * mm, "end": v(-76.18, 149.95) * mm});
            skLineSegment(sketch, "E1593", {"start": v(-76.18, 149.95) * mm, "end": v(-77.48, 149.94) * mm});
            skLineSegment(sketch, "E1594", {"start": v(-77.48, 149.94) * mm, "end": v(-78.35, 149.37) * mm});
            skLineSegment(sketch, "E1595", {"start": v(-78.35, 149.37) * mm, "end": v(-78.83, 149.13) * mm});
            skLineSegment(sketch, "E1596", {"start": v(-78.83, 149.13) * mm, "end": v(-79.81, 148.78) * mm});
            skLineSegment(sketch, "E1597", {"start": v(-79.81, 148.78) * mm, "end": v(-79.72, 148.26) * mm});
            skLineSegment(sketch, "E1598", {"start": v(-79.72, 148.26) * mm, "end": v(-79.93, 147.85) * mm});
            skLineSegment(sketch, "E1599", {"start": v(-79.93, 147.85) * mm, "end": v(-80.4, 147.61) * mm});
            skLineSegment(sketch, "E1600", {"start": v(-80.4, 147.61) * mm, "end": v(-80.78, 146.43) * mm});
            skLineSegment(sketch, "E1601", {"start": v(-80.78, 146.43) * mm, "end": v(-80.78, 145.7) * mm});
            skLineSegment(sketch, "E1602", {"start": v(-80.78, 145.7) * mm, "end": v(-80.4, 144.5) * mm});
            skLineSegment(sketch, "E1603", {"start": v(-80.4, 144.5) * mm, "end": v(-79.62, 142.96) * mm});
            skLineSegment(sketch, "E1604", {"start": v(-79.62, 142.96) * mm, "end": v(-79.23, 142.18) * mm});
            skLineSegment(sketch, "E1605", {"start": v(-79.23, 142.18) * mm, "end": v(-78.45, 140.63) * mm});
            skLineSegment(sketch, "E1606", {"start": v(-78.45, 140.63) * mm, "end": v(-78.3, 140.47) * mm});
            skLineSegment(sketch, "E1607", {"start": v(-78.3, 140.47) * mm, "end": v(-78.22, 140.4) * mm});
            skLineSegment(sketch, "E1608", {"start": v(-78.22, 140.4) * mm, "end": v(-78.07, 140.24) * mm});
            skLineSegment(sketch, "E1609", {"start": v(-78.07, 140.24) * mm, "end": v(-77.3, 138.69) * mm});
            skLineSegment(sketch, "E1610", {"start": v(-77.3, 138.69) * mm, "end": v(-76.9, 137.91) * mm});
            skLineSegment(sketch, "E1611", {"start": v(-76.9, 137.91) * mm, "end": v(-76.13, 136.36) * mm});
            skLineSegment(sketch, "E1612", {"start": v(-76.13, 136.36) * mm, "end": v(-69.7, 125.29) * mm});
            skLineSegment(sketch, "E1613", {"start": v(-69.7, 125.29) * mm, "end": v(-66.44, 119.78) * mm});
            skLineSegment(sketch, "E1614", {"start": v(-66.44, 119.78) * mm, "end": v(-59.83, 108.81) * mm});
            skLineSegment(sketch, "E1615", {"start": v(-59.83, 108.81) * mm, "end": v(-58.83, 106.93) * mm});
            skLineSegment(sketch, "E1616", {"start": v(-58.83, 106.93) * mm, "end": v(-58.24, 106.03) * mm});
            skLineSegment(sketch, "E1617", {"start": v(-58.24, 106.03) * mm, "end": v(-56.92, 104.35) * mm});
            skLineSegment(sketch, "E1618", {"start": v(-56.92, 104.35) * mm, "end": v(-56.15, 103.97) * mm});
            skLineSegment(sketch, "E1619", {"start": v(-56.15, 103.97) * mm, "end": v(-55.76, 103.77) * mm});
            skLineSegment(sketch, "E1620", {"start": v(-55.76, 103.77) * mm, "end": v(-54.98, 103.38) * mm});
            skLineSegment(sketch, "E1621", {"start": v(-138.78, -58.4) * mm, "end": v(-136.15, -58.4) * mm});
            skLineSegment(sketch, "E1622", {"start": v(-136.15, -58.4) * mm, "end": v(-134.83, -58.4) * mm});
            skLineSegment(sketch, "E1623", {"start": v(-134.83, -58.4) * mm, "end": v(-132.19, -58.4) * mm});
            skLineSegment(sketch, "E1624", {"start": v(-132.19, -58.4) * mm, "end": v(-128.9, -57.5) * mm});
            skLineSegment(sketch, "E1625", {"start": v(-128.9, -57.5) * mm, "end": v(-127.27, -56.87) * mm});
            skLineSegment(sketch, "E1626", {"start": v(-127.27, -56.87) * mm, "end": v(-124.24, -55.3) * mm});
            skLineSegment(sketch, "E1627", {"start": v(-124.24, -55.3) * mm, "end": v(-122.86, -54.55) * mm});
            skLineSegment(sketch, "E1628", {"start": v(-122.86, -54.55) * mm, "end": v(-122.19, -54.12) * mm});
            skLineSegment(sketch, "E1629", {"start": v(-122.19, -54.12) * mm, "end": v(-120.94, -53.17) * mm});
            skLineSegment(sketch, "E1630", {"start": v(-120.94, -53.17) * mm, "end": v(-119.94, -52.66) * mm});
            skLineSegment(sketch, "E1631", {"start": v(-119.94, -52.66) * mm, "end": v(-119.46, -52.34) * mm});
            skLineSegment(sketch, "E1632", {"start": v(-119.46, -52.34) * mm, "end": v(-118.6, -51.61) * mm});
            skLineSegment(sketch, "E1633", {"start": v(-118.6, -51.61) * mm, "end": v(-115.09, -49.34) * mm});
            skLineSegment(sketch, "E1634", {"start": v(-115.09, -49.34) * mm, "end": v(-113.42, -48) * mm});
            skLineSegment(sketch, "E1635", {"start": v(-113.42, -48) * mm, "end": v(-110.46, -45.02) * mm});
            skLineSegment(sketch, "E1636", {"start": v(-110.46, -45.02) * mm, "end": v(-110.15, -44.86) * mm});
            skLineSegment(sketch, "E1637", {"start": v(-110.15, -44.86) * mm, "end": v(-110, -44.79) * mm});
            skLineSegment(sketch, "E1638", {"start": v(-110, -44.79) * mm, "end": v(-109.69, -44.63) * mm});
            skLineSegment(sketch, "E1639", {"start": v(-109.69, -44.63) * mm, "end": v(-103.71, -38.66) * mm});
            skLineSegment(sketch, "E1640", {"start": v(-103.71, -38.66) * mm, "end": v(-100.72, -35.67) * mm});
            skLineSegment(sketch, "E1641", {"start": v(-100.72, -35.67) * mm, "end": v(-94.75, -29.7) * mm});
            skLineSegment(sketch, "E1642", {"start": v(-94.75, -29.7) * mm, "end": v(-88.63, -22.46) * mm});
            skLineSegment(sketch, "E1643", {"start": v(-88.63, -22.46) * mm, "end": v(-85.6, -18.8) * mm});
            skLineSegment(sketch, "E1644", {"start": v(-85.6, -18.8) * mm, "end": v(-79.62, -11.46) * mm});
            skLineSegment(sketch, "E1645", {"start": v(-79.62, -11.46) * mm, "end": v(-78.14, -9.98) * mm});
            skLineSegment(sketch, "E1646", {"start": v(-78.14, -9.98) * mm, "end": v(-77.4, -9.25) * mm});
            skLineSegment(sketch, "E1647", {"start": v(-77.4, -9.25) * mm, "end": v(-75.93, -7.77) * mm});
            skLineSegment(sketch, "E1648", {"start": v(-30.93, 58.57) * mm, "end": v(-34.11, 63.26) * mm});
            skLineSegment(sketch, "E1649", {"start": v(-34.11, 63.26) * mm, "end": v(-35.79, 65.55) * mm});
            skLineSegment(sketch, "E1650", {"start": v(-35.79, 65.55) * mm, "end": v(-39.27, 70.02) * mm});
            skLineSegment(sketch, "E1651", {"start": v(-39.27, 70.02) * mm, "end": v(-41.15, 72.96) * mm});
            skLineSegment(sketch, "E1652", {"start": v(-41.15, 72.96) * mm, "end": v(-42.2, 74.37) * mm});
            skLineSegment(sketch, "E1653", {"start": v(-42.2, 74.37) * mm, "end": v(-44.5, 77) * mm});
            skLineSegment(sketch, "E1654", {"start": v(-44.5, 77) * mm, "end": v(-44.42, 77.51) * mm});
            skLineSegment(sketch, "E1655", {"start": v(-44.42, 77.51) * mm, "end": v(-44.62, 77.93) * mm});
            skLineSegment(sketch, "E1656", {"start": v(-44.62, 77.93) * mm, "end": v(-45.09, 78.16) * mm});
            skLineSegment(sketch, "E1657", {"start": v(-45.09, 78.16) * mm, "end": v(-45.7, 79.4) * mm});
            skLineSegment(sketch, "E1658", {"start": v(-45.7, 79.4) * mm, "end": v(-46.16, 80) * mm});
            skLineSegment(sketch, "E1659", {"start": v(-46.16, 80) * mm, "end": v(-47.22, 80.88) * mm});
            skLineSegment(sketch, "E1660", {"start": v(-47.22, 80.88) * mm, "end": v(-47.13, 81.4) * mm});
            skLineSegment(sketch, "E1661", {"start": v(-47.13, 81.4) * mm, "end": v(-47.34, 81.8) * mm});
            skLineSegment(sketch, "E1662", {"start": v(-47.34, 81.8) * mm, "end": v(-47.8, 82.04) * mm});
            skLineSegment(sketch, "E1663", {"start": v(-47.8, 82.04) * mm, "end": v(-48.7, 83.77) * mm});
            skLineSegment(sketch, "E1664", {"start": v(-48.7, 83.77) * mm, "end": v(-49.3, 84.59) * mm});
            skLineSegment(sketch, "E1665", {"start": v(-49.3, 84.59) * mm, "end": v(-50.71, 85.92) * mm});
            skLineSegment(sketch, "E1666", {"start": v(-50.71, 85.92) * mm, "end": v(-50.62, 86.44) * mm});
            skLineSegment(sketch, "E1667", {"start": v(-50.62, 86.44) * mm, "end": v(-50.83, 86.85) * mm});
            skLineSegment(sketch, "E1668", {"start": v(-50.83, 86.85) * mm, "end": v(-51.3, 87.09) * mm});
            skLineSegment(sketch, "E1669", {"start": v(-51.3, 87.09) * mm, "end": v(-51.8, 88.09) * mm});
            skLineSegment(sketch, "E1670", {"start": v(-51.8, 88.09) * mm, "end": v(-52.12, 88.56) * mm});
            skLineSegment(sketch, "E1671", {"start": v(-52.12, 88.56) * mm, "end": v(-52.85, 89.42) * mm});
            skLineSegment(sketch, "E1672", {"start": v(-52.85, 89.42) * mm, "end": v(-53.35, 90.41) * mm});
            skLineSegment(sketch, "E1673", {"start": v(-53.35, 90.41) * mm, "end": v(-53.67, 90.9) * mm});
            skLineSegment(sketch, "E1674", {"start": v(-53.67, 90.9) * mm, "end": v(-54.4, 91.74) * mm});
            skLineSegment(sketch, "E1675", {"start": v(-54.4, 91.74) * mm, "end": v(-54.9, 92.74) * mm});
            skLineSegment(sketch, "E1676", {"start": v(-54.9, 92.74) * mm, "end": v(-55.22, 93.22) * mm});
            skLineSegment(sketch, "E1677", {"start": v(-55.22, 93.22) * mm, "end": v(-55.95, 94.07) * mm});
            skLineSegment(sketch, "E1678", {"start": v(-55.95, 94.07) * mm, "end": v(-56.9, 95.85) * mm});
            skLineSegment(sketch, "E1679", {"start": v(-56.9, 95.85) * mm, "end": v(-57.46, 96.72) * mm});
            skLineSegment(sketch, "E1680", {"start": v(-57.46, 96.72) * mm, "end": v(-58.67, 98.34) * mm});
            skLineSegment(sketch, "E1681", {"start": v(-58.67, 98.34) * mm, "end": v(-59.97, 100.57) * mm});
            skLineSegment(sketch, "E1682", {"start": v(-59.97, 100.57) * mm, "end": v(-60.67, 101.66) * mm});
            skLineSegment(sketch, "E1683", {"start": v(-60.67, 101.66) * mm, "end": v(-62.16, 103.77) * mm});
            skLineSegment(sketch, "E1684", {"start": v(-62.16, 103.77) * mm, "end": v(-68.56, 114.46) * mm});
            skLineSegment(sketch, "E1685", {"start": v(-68.56, 114.46) * mm, "end": v(-71.74, 119.81) * mm});
            skLineSegment(sketch, "E1686", {"start": v(-71.74, 119.81) * mm, "end": v(-78.07, 130.54) * mm});
            skLineSegment(sketch, "E1687", {"start": v(-78.07, 130.54) * mm, "end": v(-78.84, 132.1) * mm});
            skLineSegment(sketch, "E1688", {"start": v(-78.84, 132.1) * mm, "end": v(-79.23, 132.87) * mm});
            skLineSegment(sketch, "E1689", {"start": v(-79.23, 132.87) * mm, "end": v(-80, 134.42) * mm});
            skLineSegment(sketch, "E1690", {"start": v(-80, 134.42) * mm, "end": v(-80.16, 134.58) * mm});
            skLineSegment(sketch, "E1691", {"start": v(-80.16, 134.58) * mm, "end": v(-80.24, 134.65) * mm});
            skLineSegment(sketch, "E1692", {"start": v(-80.24, 134.65) * mm, "end": v(-80.4, 134.8) * mm});
            skLineSegment(sketch, "E1693", {"start": v(-80.4, 134.8) * mm, "end": v(-81.17, 136.36) * mm});
            skLineSegment(sketch, "E1694", {"start": v(-81.17, 136.36) * mm, "end": v(-81.56, 137.14) * mm});
            skLineSegment(sketch, "E1695", {"start": v(-81.56, 137.14) * mm, "end": v(-82.33, 138.69) * mm});
            skLineSegment(sketch, "E1696", {"start": v(-82.33, 138.69) * mm, "end": v(-82.49, 138.84) * mm});
            skLineSegment(sketch, "E1697", {"start": v(-82.49, 138.84) * mm, "end": v(-82.57, 138.92) * mm});
            skLineSegment(sketch, "E1698", {"start": v(-82.57, 138.92) * mm, "end": v(-82.72, 139.08) * mm});
            skLineSegment(sketch, "E1699", {"start": v(-82.72, 139.08) * mm, "end": v(-84.12, 141.87) * mm});
            skLineSegment(sketch, "E1700", {"start": v(-84.12, 141.87) * mm, "end": v(-84.82, 143.27) * mm});
            skLineSegment(sketch, "E1701", {"start": v(-84.82, 143.27) * mm, "end": v(-86.21, 146.06) * mm});
            skLineSegment(sketch, "E1702", {"start": v(-86.21, 146.06) * mm, "end": v(-87.1, 147.73) * mm});
            skLineSegment(sketch, "E1703", {"start": v(-87.1, 147.73) * mm, "end": v(-87.66, 148.53) * mm});
            skLineSegment(sketch, "E1704", {"start": v(-87.66, 148.53) * mm, "end": v(-88.93, 149.94) * mm});
            skLineSegment(sketch, "E1705", {"start": v(-88.93, 149.94) * mm, "end": v(-90.46, 150.51) * mm});
            skLineSegment(sketch, "E1706", {"start": v(-90.46, 150.51) * mm, "end": v(-91.43, 150.56) * mm});
            skLineSegment(sketch, "E1707", {"start": v(-91.43, 150.56) * mm, "end": v(-93, 150.13) * mm});
            skLineSegment(sketch, "E1708", {"start": v(-93, 150.13) * mm, "end": v(-94.14, 149.58) * mm});
            skLineSegment(sketch, "E1709", {"start": v(-94.14, 149.58) * mm, "end": v(-94.85, 149.45) * mm});
            skLineSegment(sketch, "E1710", {"start": v(-94.85, 149.45) * mm, "end": v(-96.1, 149.55) * mm});
            skLineSegment(sketch, "E1711", {"start": v(-96.1, 149.55) * mm, "end": v(-96.96, 150.23) * mm});
            skLineSegment(sketch, "E1712", {"start": v(-96.96, 150.23) * mm, "end": v(-97.88, 150.3) * mm});
            skLineSegment(sketch, "E1713", {"start": v(-97.88, 150.3) * mm, "end": v(-98.82, 149.75) * mm});
            skLineSegment(sketch, "E1714", {"start": v(-98.82, 149.75) * mm, "end": v(-99.7, 149.19) * mm});
            skLineSegment(sketch, "E1715", {"start": v(-99.7, 149.19) * mm, "end": v(-100.11, 148.82) * mm});
            skLineSegment(sketch, "E1716", {"start": v(-100.11, 148.82) * mm, "end": v(-100.76, 148) * mm});
            skLineSegment(sketch, "E1717", {"start": v(-100.76, 148) * mm, "end": v(-100.76, 146.37) * mm});
            skLineSegment(sketch, "E1718", {"start": v(-100.76, 146.37) * mm, "end": v(-100.76, 145.56) * mm});
            skLineSegment(sketch, "E1719", {"start": v(-100.76, 145.56) * mm, "end": v(-100.76, 143.93) * mm});
            skLineSegment(sketch, "E1720", {"start": v(-100.76, 143.93) * mm, "end": v(-101.38, 143.3) * mm});
            skLineSegment(sketch, "E1721", {"start": v(-101.38, 143.3) * mm, "end": v(-101.7, 143) * mm});
            skLineSegment(sketch, "E1722", {"start": v(-101.7, 143) * mm, "end": v(-102.31, 142.38) * mm});
            skLineSegment(sketch, "E1723", {"start": v(-102.31, 142.38) * mm, "end": v(-102.74, 141.29) * mm});
            skLineSegment(sketch, "E1724", {"start": v(-102.74, 141.29) * mm, "end": v(-102.78, 140.6) * mm});
            skLineSegment(sketch, "E1725", {"start": v(-102.78, 140.6) * mm, "end": v(-102.5, 139.47) * mm});
            skLineSegment(sketch, "E1726", {"start": v(-102.5, 139.47) * mm, "end": v(-102.26, 138.8) * mm});
            skLineSegment(sketch, "E1727", {"start": v(-102.26, 138.8) * mm, "end": v(-102.32, 138.3) * mm});
            skLineSegment(sketch, "E1728", {"start": v(-102.32, 138.3) * mm, "end": v(-102.7, 137.72) * mm});
            skLineSegment(sketch, "E1729", {"start": v(-102.7, 137.72) * mm, "end": v(-103.3, 137) * mm});
            skLineSegment(sketch, "E1730", {"start": v(-103.3, 137) * mm, "end": v(-103.61, 136.65) * mm});
            skLineSegment(sketch, "E1731", {"start": v(-103.61, 136.65) * mm, "end": v(-104.25, 135.97) * mm});
            skLineSegment(sketch, "E1732", {"start": v(-104.25, 135.97) * mm, "end": v(-104.25, 134.34) * mm});
            skLineSegment(sketch, "E1733", {"start": v(-104.25, 134.34) * mm, "end": v(-104.25, 133.53) * mm});
            skLineSegment(sketch, "E1734", {"start": v(-104.25, 133.53) * mm, "end": v(-104.25, 131.9) * mm});
            skLineSegment(sketch, "E1735", {"start": v(-104.25, 131.9) * mm, "end": v(-105.03, 131.05) * mm});
            skLineSegment(sketch, "E1736", {"start": v(-105.03, 131.05) * mm, "end": v(-105.42, 130.62) * mm});
            skLineSegment(sketch, "E1737", {"start": v(-105.42, 130.62) * mm, "end": v(-106.2, 129.77) * mm});
            skLineSegment(sketch, "E1738", {"start": v(-106.2, 129.77) * mm, "end": v(-106.17, 128.52) * mm});
            skLineSegment(sketch, "E1739", {"start": v(-106.17, 128.52) * mm, "end": v(-106.13, 127.9) * mm});
            skLineSegment(sketch, "E1740", {"start": v(-106.13, 127.9) * mm, "end": v(-106, 126.66) * mm});
            skLineSegment(sketch, "E1741", {"start": v(-106, 126.66) * mm, "end": v(-106.5, 125.66) * mm});
            skLineSegment(sketch, "E1742", {"start": v(-106.5, 125.66) * mm, "end": v(-106.83, 125.19) * mm});
            skLineSegment(sketch, "E1743", {"start": v(-106.83, 125.19) * mm, "end": v(-107.55, 124.33) * mm});
            skLineSegment(sketch, "E1744", {"start": v(-107.55, 124.33) * mm, "end": v(-107.85, 122.73) * mm});
            skLineSegment(sketch, "E1745", {"start": v(-107.85, 122.73) * mm, "end": v(-107.9, 121.89) * mm});
            skLineSegment(sketch, "E1746", {"start": v(-107.9, 121.89) * mm, "end": v(-107.75, 120.26) * mm});
            skLineSegment(sketch, "E1747", {"start": v(-107.75, 120.26) * mm, "end": v(-108.35, 119.54) * mm});
            skLineSegment(sketch, "E1748", {"start": v(-108.35, 119.54) * mm, "end": v(-108.66, 119.2) * mm});
            skLineSegment(sketch, "E1749", {"start": v(-108.66, 119.2) * mm, "end": v(-109.3, 118.51) * mm});
            skLineSegment(sketch, "E1750", {"start": v(-109.3, 118.51) * mm, "end": v(-109.53, 117.77) * mm});
            skLineSegment(sketch, "E1751", {"start": v(-109.53, 117.77) * mm, "end": v(-109.57, 117.35) * mm});
            skLineSegment(sketch, "E1752", {"start": v(-109.57, 117.35) * mm, "end": v(-109.5, 116.57) * mm});
            skLineSegment(sketch, "E1753", {"start": v(-109.5, 116.57) * mm, "end": v(-109, 115.7) * mm});
            skLineSegment(sketch, "E1754", {"start": v(-109, 115.7) * mm, "end": v(-109.06, 114.85) * mm});
            skLineSegment(sketch, "E1755", {"start": v(-109.06, 114.85) * mm, "end": v(-109.69, 114.05) * mm});
            skLineSegment(sketch, "E1756", {"start": v(-109.69, 114.05) * mm, "end": v(-110.17, 113.25) * mm});
            skLineSegment(sketch, "E1757", {"start": v(-110.17, 113.25) * mm, "end": v(-110.5, 112.88) * mm});
            skLineSegment(sketch, "E1758", {"start": v(-110.5, 112.88) * mm, "end": v(-111.24, 112.3) * mm});
            skLineSegment(sketch, "E1759", {"start": v(-111.24, 112.3) * mm, "end": v(-111.25, 110.75) * mm});
            skLineSegment(sketch, "E1760", {"start": v(-111.25, 110.75) * mm, "end": v(-111.21, 109.97) * mm});
            skLineSegment(sketch, "E1761", {"start": v(-111.21, 109.97) * mm, "end": v(-111.04, 108.43) * mm});
            skLineSegment(sketch, "E1762", {"start": v(-111.04, 108.43) * mm, "end": v(-111.73, 107.23) * mm});
            skLineSegment(sketch, "E1763", {"start": v(-111.73, 107.23) * mm, "end": v(-112.17, 106.66) * mm});
            skLineSegment(sketch, "E1764", {"start": v(-112.17, 106.66) * mm, "end": v(-113.18, 105.71) * mm});
            skLineSegment(sketch, "E1765", {"start": v(-113.18, 105.71) * mm, "end": v(-112.96, 104.17) * mm});
            skLineSegment(sketch, "E1766", {"start": v(-112.96, 104.17) * mm, "end": v(-112.92, 103.38) * mm});
            skLineSegment(sketch, "E1767", {"start": v(-112.92, 103.38) * mm, "end": v(-112.98, 101.83) * mm});
            skLineSegment(sketch, "E1768", {"start": v(-112.98, 101.83) * mm, "end": v(-113.68, 100.64) * mm});
            skLineSegment(sketch, "E1769", {"start": v(-113.68, 100.64) * mm, "end": v(-114.13, 100.08) * mm});
            skLineSegment(sketch, "E1770", {"start": v(-114.13, 100.08) * mm, "end": v(-115.12, 99.12) * mm});
            skLineSegment(sketch, "E1771", {"start": v(-115.12, 99.12) * mm, "end": v(-114.78, 97.44) * mm});
            skLineSegment(sketch, "E1772", {"start": v(-114.78, 97.44) * mm, "end": v(-114.74, 96.55) * mm});
            skLineSegment(sketch, "E1773", {"start": v(-114.74, 96.55) * mm, "end": v(-114.92, 94.85) * mm});
            skLineSegment(sketch, "E1774", {"start": v(-114.92, 94.85) * mm, "end": v(-115.62, 94.15) * mm});
            skLineSegment(sketch, "E1775", {"start": v(-115.62, 94.15) * mm, "end": v(-115.97, 93.8) * mm});
            skLineSegment(sketch, "E1776", {"start": v(-115.97, 93.8) * mm, "end": v(-116.67, 93.1) * mm});
            skLineSegment(sketch, "E1777", {"start": v(-116.67, 93.1) * mm, "end": v(-117.05, 92.16) * mm});
            skLineSegment(sketch, "E1778", {"start": v(-117.05, 92.16) * mm, "end": v(-117.1, 91.57) * mm});
            skLineSegment(sketch, "E1779", {"start": v(-117.1, 91.57) * mm, "end": v(-116.86, 90.58) * mm});
            skLineSegment(sketch, "E1780", {"start": v(-116.86, 90.58) * mm, "end": v(-116.55, 89.38) * mm});
            skLineSegment(sketch, "E1781", {"start": v(-116.55, 89.38) * mm, "end": v(-116.6, 88.63) * mm});
            skLineSegment(sketch, "E1782", {"start": v(-116.6, 88.63) * mm, "end": v(-117.06, 87.48) * mm});
            skLineSegment(sketch, "E1783", {"start": v(-117.06, 87.48) * mm, "end": v(-117.45, 87.63) * mm});
            skLineSegment(sketch, "E1784", {"start": v(-117.45, 87.63) * mm, "end": v(-117.85, 87.47) * mm});
            skLineSegment(sketch, "E1785", {"start": v(-117.85, 87.47) * mm, "end": v(-118.03, 87.09) * mm});
            skLineSegment(sketch, "E1786", {"start": v(-118.03, 87.09) * mm, "end": v(-118.42, 86.31) * mm});
            skLineSegment(sketch, "E1787", {"start": v(-118.42, 86.31) * mm, "end": v(-118.6, 85.92) * mm});
            skLineSegment(sketch, "E1788", {"start": v(-118.6, 85.92) * mm, "end": v(-119, 85.15) * mm});
            skLineSegment(sketch, "E1789", {"start": v(-119, 85.15) * mm, "end": v(-118.6, 83.65) * mm});
            skLineSegment(sketch, "E1790", {"start": v(-118.6, 83.65) * mm, "end": v(-118.56, 82.8) * mm});
            skLineSegment(sketch, "E1791", {"start": v(-118.56, 82.8) * mm, "end": v(-118.8, 81.27) * mm});
            skLineSegment(sketch, "E1792", {"start": v(-118.8, 81.27) * mm, "end": v(-119.05, 81.06) * mm});
            skLineSegment(sketch, "E1793", {"start": v(-119.05, 81.06) * mm, "end": v(-119.12, 80.79) * mm});
            skLineSegment(sketch, "E1794", {"start": v(-119.12, 80.79) * mm, "end": v(-119, 80.5) * mm});
            skLineSegment(sketch, "E1795", {"start": v(-119, 80.5) * mm, "end": v(-119.73, 80.43) * mm});
            skLineSegment(sketch, "E1796", {"start": v(-119.73, 80.43) * mm, "end": v(-120.17, 80.15) * mm});
            skLineSegment(sketch, "E1797", {"start": v(-120.17, 80.15) * mm, "end": v(-120.55, 79.52) * mm});
            skLineSegment(sketch, "E1798", {"start": v(-120.55, 79.52) * mm, "end": v(-121.08, 78.15) * mm});
            skLineSegment(sketch, "E1799", {"start": v(-121.08, 78.15) * mm, "end": v(-121.13, 77.26) * mm});
            skLineSegment(sketch, "E1800", {"start": v(-121.13, 77.26) * mm, "end": v(-120.74, 75.84) * mm});
            skLineSegment(sketch, "E1801", {"start": v(-120.74, 75.84) * mm, "end": v(-120.3, 75.1) * mm});
            skLineSegment(sketch, "E1802", {"start": v(-120.3, 75.1) * mm, "end": v(-120.38, 74.35) * mm});
            skLineSegment(sketch, "E1803", {"start": v(-120.38, 74.35) * mm, "end": v(-120.94, 73.7) * mm});
            skLineSegment(sketch, "E1804", {"start": v(-120.94, 73.7) * mm, "end": v(-121.71, 72.93) * mm});
            skLineSegment(sketch, "E1805", {"start": v(-121.71, 72.93) * mm, "end": v(-122.1, 72.54) * mm});
            skLineSegment(sketch, "E1806", {"start": v(-122.1, 72.54) * mm, "end": v(-122.88, 71.76) * mm});
            skLineSegment(sketch, "E1807", {"start": v(-122.88, 71.76) * mm, "end": v(-123.26, 70.83) * mm});
            skLineSegment(sketch, "E1808", {"start": v(-123.26, 70.83) * mm, "end": v(-123.3, 70.23) * mm});
            skLineSegment(sketch, "E1809", {"start": v(-123.3, 70.23) * mm, "end": v(-123.07, 69.24) * mm});
            skLineSegment(sketch, "E1810", {"start": v(-123.07, 69.24) * mm, "end": v(-122.56, 68.02) * mm});
            skLineSegment(sketch, "E1811", {"start": v(-122.56, 68.02) * mm, "end": v(-122.62, 67.1) * mm});
            skLineSegment(sketch, "E1812", {"start": v(-122.62, 67.1) * mm, "end": v(-123.27, 65.94) * mm});
            skLineSegment(sketch, "E1813", {"start": v(-123.27, 65.94) * mm, "end": v(-123.52, 65.49) * mm});
            skLineSegment(sketch, "E1814", {"start": v(-123.52, 65.49) * mm, "end": v(-123.91, 65.3) * mm});
            skLineSegment(sketch, "E1815", {"start": v(-123.91, 65.3) * mm, "end": v(-124.43, 65.36) * mm});
            skLineSegment(sketch, "E1816", {"start": v(-124.43, 65.36) * mm, "end": v(-124.34, 64.85) * mm});
            skLineSegment(sketch, "E1817", {"start": v(-124.34, 64.85) * mm, "end": v(-124.55, 64.43) * mm});
            skLineSegment(sketch, "E1818", {"start": v(-124.55, 64.43) * mm, "end": v(-125.01, 64.2) * mm});
            skLineSegment(sketch, "E1819", {"start": v(-125.01, 64.2) * mm, "end": v(-124.99, 61.95) * mm});
            skLineSegment(sketch, "E1820", {"start": v(-124.99, 61.95) * mm, "end": v(-125.03, 60.82) * mm});
            skLineSegment(sketch, "E1821", {"start": v(-125.03, 60.82) * mm, "end": v(-125.2, 58.57) * mm});
            skLineSegment(sketch, "E1822", {"start": v(-125.2, 58.57) * mm, "end": v(-126.14, 57.57) * mm});
            skLineSegment(sketch, "E1823", {"start": v(-126.14, 57.57) * mm, "end": v(-126.6, 57.07) * mm});
            skLineSegment(sketch, "E1824", {"start": v(-126.6, 57.07) * mm, "end": v(-127.53, 56.05) * mm});
            skLineSegment(sketch, "E1825", {"start": v(-127.53, 56.05) * mm, "end": v(-127.3, 53.89) * mm});
            skLineSegment(sketch, "E1826", {"start": v(-127.3, 53.89) * mm, "end": v(-127.25, 52.8) * mm});
            skLineSegment(sketch, "E1827", {"start": v(-127.25, 52.8) * mm, "end": v(-127.34, 50.62) * mm});
            skLineSegment(sketch, "E1828", {"start": v(-127.34, 50.62) * mm, "end": v(-128.35, 49.6) * mm});
            skLineSegment(sketch, "E1829", {"start": v(-128.35, 49.6) * mm, "end": v(-128.85, 49.1) * mm});
            skLineSegment(sketch, "E1830", {"start": v(-128.85, 49.1) * mm, "end": v(-129.86, 48.1) * mm});
            skLineSegment(sketch, "E1831", {"start": v(-129.86, 48.1) * mm, "end": v(-129.86, 46.62) * mm});
            skLineSegment(sketch, "E1832", {"start": v(-129.86, 46.62) * mm, "end": v(-129.86, 45.89) * mm});
            skLineSegment(sketch, "E1833", {"start": v(-129.86, 45.89) * mm, "end": v(-129.86, 44.41) * mm});
            skLineSegment(sketch, "E1834", {"start": v(-129.86, 44.41) * mm, "end": v(-129.27, 43.9) * mm});
            skLineSegment(sketch, "E1835", {"start": v(-129.27, 43.9) * mm, "end": v(-129.18, 43.08) * mm});
            skLineSegment(sketch, "E1836", {"start": v(-129.18, 43.08) * mm, "end": v(-129.67, 42.47) * mm});
            skLineSegment(sketch, "E1837", {"start": v(-129.67, 42.47) * mm, "end": v(-129.93, 42.02) * mm});
            skLineSegment(sketch, "E1838", {"start": v(-129.93, 42.02) * mm, "end": v(-130.04, 41.79) * mm});
            skLineSegment(sketch, "E1839", {"start": v(-130.04, 41.79) * mm, "end": v(-130.25, 41.3) * mm});
            skLineSegment(sketch, "E1840", {"start": v(-130.25, 41.3) * mm, "end": v(-131.18, 41.15) * mm});
            skLineSegment(sketch, "E1841", {"start": v(-131.18, 41.15) * mm, "end": v(-131.72, 40.77) * mm});
            skLineSegment(sketch, "E1842", {"start": v(-131.72, 40.77) * mm, "end": v(-132.19, 39.95) * mm});
            skLineSegment(sketch, "E1843", {"start": v(-132.19, 39.95) * mm, "end": v(-132.57, 39.01) * mm});
            skLineSegment(sketch, "E1844", {"start": v(-132.57, 39.01) * mm, "end": v(-132.61, 38.41) * mm});
            skLineSegment(sketch, "E1845", {"start": v(-132.61, 38.41) * mm, "end": v(-132.38, 37.43) * mm});
            skLineSegment(sketch, "E1846", {"start": v(-132.38, 37.43) * mm, "end": v(-131.94, 36.1) * mm});
            skLineSegment(sketch, "E1847", {"start": v(-131.94, 36.1) * mm, "end": v(-131.85, 35.33) * mm});
            skLineSegment(sketch, "E1848", {"start": v(-131.85, 35.33) * mm, "end": v(-132, 33.94) * mm});
            skLineSegment(sketch, "E1849", {"start": v(-132, 33.94) * mm, "end": v(-132.25, 33.48) * mm});
            skLineSegment(sketch, "E1850", {"start": v(-132.25, 33.48) * mm, "end": v(-132.37, 33.25) * mm});
            skLineSegment(sketch, "E1851", {"start": v(-132.37, 33.25) * mm, "end": v(-132.58, 32.77) * mm});
            skLineSegment(sketch, "E1852", {"start": v(-132.58, 32.77) * mm, "end": v(-133.51, 32.61) * mm});
            skLineSegment(sketch, "E1853", {"start": v(-133.51, 32.61) * mm, "end": v(-134.05, 32.24) * mm});
            skLineSegment(sketch, "E1854", {"start": v(-134.05, 32.24) * mm, "end": v(-134.52, 31.41) * mm});
            skLineSegment(sketch, "E1855", {"start": v(-134.52, 31.41) * mm, "end": v(-135.09, 29.89) * mm});
            skLineSegment(sketch, "E1856", {"start": v(-135.09, 29.89) * mm, "end": v(-135.13, 28.92) * mm});
            skLineSegment(sketch, "E1857", {"start": v(-135.13, 28.92) * mm, "end": v(-134.71, 27.34) * mm});
            skLineSegment(sketch, "E1858", {"start": v(-134.71, 27.34) * mm, "end": v(-134.25, 26.27) * mm});
            skLineSegment(sketch, "E1859", {"start": v(-134.25, 26.27) * mm, "end": v(-134.3, 25.43) * mm});
            skLineSegment(sketch, "E1860", {"start": v(-134.3, 25.43) * mm, "end": v(-134.9, 24.43) * mm});
            skLineSegment(sketch, "E1861", {"start": v(-134.9, 24.43) * mm, "end": v(-135.37, 23.6) * mm});
            skLineSegment(sketch, "E1862", {"start": v(-135.37, 23.6) * mm, "end": v(-135.91, 23.23) * mm});
            skLineSegment(sketch, "E1863", {"start": v(-135.91, 23.23) * mm, "end": v(-136.84, 23.07) * mm});
            skLineSegment(sketch, "E1864", {"start": v(-136.84, 23.07) * mm, "end": v(-136.76, 22.56) * mm});
            skLineSegment(sketch, "E1865", {"start": v(-136.76, 22.56) * mm, "end": v(-136.96, 22.14) * mm});
            skLineSegment(sketch, "E1866", {"start": v(-136.96, 22.14) * mm, "end": v(-137.43, 21.9) * mm});
            skLineSegment(sketch, "E1867", {"start": v(-137.43, 21.9) * mm, "end": v(-137.9, 20.84) * mm});
            skLineSegment(sketch, "E1868", {"start": v(-137.9, 20.84) * mm, "end": v(-137.84, 20) * mm});
            skLineSegment(sketch, "E1869", {"start": v(-137.84, 20) * mm, "end": v(-137.23, 19) * mm});
            skLineSegment(sketch, "E1870", {"start": v(-137.23, 19) * mm, "end": v(-136.69, 18.17) * mm});
            skLineSegment(sketch, "E1871", {"start": v(-136.69, 18.17) * mm, "end": v(-136.22, 17.8) * mm});
            skLineSegment(sketch, "E1872", {"start": v(-136.22, 17.8) * mm, "end": v(-135.3, 17.45) * mm});
            skLineSegment(sketch, "E1873", {"start": v(-135.3, 17.45) * mm, "end": v(-133.96, 17.08) * mm});
            skLineSegment(sketch, "E1874", {"start": v(-133.96, 17.08) * mm, "end": v(-133.29, 16.74) * mm});
            skLineSegment(sketch, "E1875", {"start": v(-133.29, 16.74) * mm, "end": v(-132.19, 15.9) * mm});
            skLineSegment(sketch, "E1876", {"start": v(-132.19, 15.9) * mm, "end": v(-130.42, 14.9) * mm});
            skLineSegment(sketch, "E1877", {"start": v(-130.42, 14.9) * mm, "end": v(-129.6, 14.03) * mm});
            skLineSegment(sketch, "E1878", {"start": v(-129.6, 14.03) * mm, "end": v(-128.7, 12.2) * mm});
            skLineSegment(sketch, "E1879", {"start": v(-128.7, 12.2) * mm, "end": v(-128.39, 11.21) * mm});
            skLineSegment(sketch, "E1880", {"start": v(-128.39, 11.21) * mm, "end": v(-128.14, 10.72) * mm});
            skLineSegment(sketch, "E1881", {"start": v(-128.14, 10.72) * mm, "end": v(-127.53, 9.88) * mm});
            skLineSegment(sketch, "E1882", {"start": v(-127.53, 9.88) * mm, "end": v(-127.48, 8.17) * mm});
            skLineSegment(sketch, "E1883", {"start": v(-127.48, 8.17) * mm, "end": v(-127.56, 7.29) * mm});
            skLineSegment(sketch, "E1884", {"start": v(-127.56, 7.29) * mm, "end": v(-127.92, 5.61) * mm});
            skLineSegment(sketch, "E1885", {"start": v(-127.92, 5.61) * mm, "end": v(-130.25, 2.82) * mm});
            skLineSegment(sketch, "E1886", {"start": v(-130.25, 2.82) * mm, "end": v(-131.41, 1.42) * mm});
            skLineSegment(sketch, "E1887", {"start": v(-131.41, 1.42) * mm, "end": v(-133.74, -1.37) * mm});
            skLineSegment(sketch, "E1888", {"start": v(-133.74, -1.37) * mm, "end": v(-133.65, -1.88) * mm});
            skLineSegment(sketch, "E1889", {"start": v(-133.65, -1.88) * mm, "end": v(-133.86, -2.3) * mm});
            skLineSegment(sketch, "E1890", {"start": v(-133.86, -2.3) * mm, "end": v(-134.32, -2.53) * mm});
            skLineSegment(sketch, "E1891", {"start": v(-134.32, -2.53) * mm, "end": v(-135.88, -5.51) * mm});
            skLineSegment(sketch, "E1892", {"start": v(-135.88, -5.51) * mm, "end": v(-136.83, -6.94) * mm});
            skLineSegment(sketch, "E1893", {"start": v(-136.83, -6.94) * mm, "end": v(-138.98, -9.52) * mm});
            skLineSegment(sketch, "E1894", {"start": v(-138.98, -9.52) * mm, "end": v(-144.3, -15.84) * mm});
            skLineSegment(sketch, "E1895", {"start": v(-144.3, -15.84) * mm, "end": v(-146.97, -18.98) * mm});
            skLineSegment(sketch, "E1896", {"start": v(-146.97, -18.98) * mm, "end": v(-152.36, -25.23) * mm});
            skLineSegment(sketch, "E1897", {"start": v(-152.36, -25.23) * mm, "end": v(-152.8, -26.56) * mm});
            skLineSegment(sketch, "E1898", {"start": v(-152.8, -26.56) * mm, "end": v(-153.24, -27.23) * mm});
            skLineSegment(sketch, "E1899", {"start": v(-153.24, -27.23) * mm, "end": v(-154.3, -28.14) * mm});
            skLineSegment(sketch, "E1900", {"start": v(-154.3, -28.14) * mm, "end": v(-154.2, -28.94) * mm});
            skLineSegment(sketch, "E1901", {"start": v(-154.2, -28.94) * mm, "end": v(-154.35, -29.47) * mm});
            skLineSegment(sketch, "E1902", {"start": v(-154.35, -29.47) * mm, "end": v(-154.89, -30.08) * mm});
            skLineSegment(sketch, "E1903", {"start": v(-154.89, -30.08) * mm, "end": v(-155.12, -31.2) * mm});
            skLineSegment(sketch, "E1904", {"start": v(-155.12, -31.2) * mm, "end": v(-155.32, -31.77) * mm});
            skLineSegment(sketch, "E1905", {"start": v(-155.32, -31.77) * mm, "end": v(-155.86, -32.8) * mm});
            skLineSegment(sketch, "E1906", {"start": v(-155.86, -32.8) * mm, "end": v(-155.55, -33.53) * mm});
            skLineSegment(sketch, "E1907", {"start": v(-155.55, -33.53) * mm, "end": v(-155.68, -34.18) * mm});
            skLineSegment(sketch, "E1908", {"start": v(-155.68, -34.18) * mm, "end": v(-156.24, -34.74) * mm});
            skLineSegment(sketch, "E1909", {"start": v(-156.24, -34.74) * mm, "end": v(-156.24, -36.9) * mm});
            skLineSegment(sketch, "E1910", {"start": v(-156.24, -36.9) * mm, "end": v(-156.24, -38) * mm});
            skLineSegment(sketch, "E1911", {"start": v(-156.24, -38) * mm, "end": v(-156.24, -40.17) * mm});
            skLineSegment(sketch, "E1912", {"start": v(-156.24, -40.17) * mm, "end": v(-155.43, -43.53) * mm});
            skLineSegment(sketch, "E1913", {"start": v(-155.43, -43.53) * mm, "end": v(-154.83, -45.2) * mm});
            skLineSegment(sketch, "E1914", {"start": v(-154.83, -45.2) * mm, "end": v(-153.33, -48.32) * mm});
            skLineSegment(sketch, "E1915", {"start": v(-153.33, -48.32) * mm, "end": v(-151.6, -50.87) * mm});
            skLineSegment(sketch, "E1916", {"start": v(-151.6, -50.87) * mm, "end": v(-150.57, -52.06) * mm});
            skLineSegment(sketch, "E1917", {"start": v(-150.57, -52.06) * mm, "end": v(-148.29, -54.14) * mm});
            skLineSegment(sketch, "E1918", {"start": v(-148.29, -54.14) * mm, "end": v(-145.3, -56.16) * mm});
            skLineSegment(sketch, "E1919", {"start": v(-145.3, -56.16) * mm, "end": v(-143.6, -56.97) * mm});
            skLineSegment(sketch, "E1920", {"start": v(-143.6, -56.97) * mm, "end": v(-140.14, -58.02) * mm});
            skLineSegment(sketch, "E1921", {"start": v(-140.14, -58.02) * mm, "end": v(-139.64, -57.75) * mm});
            skLineSegment(sketch, "E1922", {"start": v(-139.64, -57.75) * mm, "end": v(-139.07, -57.92) * mm});
            skLineSegment(sketch, "E1923", {"start": v(-139.07, -57.92) * mm, "end": v(-138.78, -58.4) * mm});
            skLineSegment(sketch, "E1924", {"start": v(-6.1, 46.16) * mm, "end": v(-6.12, 45.14) * mm});
            skLineSegment(sketch, "E1925", {"start": v(-6.12, 45.14) * mm, "end": v(-6.04, 44.6) * mm});
            skLineSegment(sketch, "E1926", {"start": v(-6.04, 44.6) * mm, "end": v(-5.7, 43.63) * mm});
            skLineSegment(sketch, "E1927", {"start": v(-10.36, 19.39) * mm, "end": v(-10.6, 18.38) * mm});
            skLineSegment(sketch, "E1928", {"start": v(-10.6, 18.38) * mm, "end": v(-10.71, 17.87) * mm});
            skLineSegment(sketch, "E1929", {"start": v(-10.71, 17.87) * mm, "end": v(-10.95, 16.86) * mm});
            skLineSegment(sketch, "E1930", {"start": v(-5.32, 42.47) * mm, "end": v(-5.32, 39.06) * mm});
            skLineSegment(sketch, "E1931", {"start": v(-5.32, 39.06) * mm, "end": v(-5.32, 37.35) * mm});
            skLineSegment(sketch, "E1932", {"start": v(-5.32, 37.35) * mm, "end": v(-5.32, 33.94) * mm});
            skLineSegment(sketch, "E1933", {"start": v(-5.32, 33.94) * mm, "end": v(-6.12, 29.81) * mm});
            skLineSegment(sketch, "E1934", {"start": v(-6.12, 29.81) * mm, "end": v(-6.71, 27.76) * mm});
            skLineSegment(sketch, "E1935", {"start": v(-6.71, 27.76) * mm, "end": v(-8.23, 23.85) * mm});
            skLineSegment(sketch, "E1936", {"start": v(-8.23, 23.85) * mm, "end": v(-8.98, 22.38) * mm});
            skLineSegment(sketch, "E1937", {"start": v(-8.98, 22.38) * mm, "end": v(-9.26, 21.58) * mm});
            skLineSegment(sketch, "E1938", {"start": v(-9.26, 21.58) * mm, "end": v(-9.59, 19.97) * mm});
            skLineSegment(sketch, "E1939.1", {"start": v(-71.4, -3.24) * mm, "end": v(-74.65, -6.5) * mm});
            skLineSegment(sketch, "E1939.2", {"start": v(-67.83, -0.36) * mm, "end": v(-71.4, -3.24) * mm});
            skLineSegment(sketch, "E1939.3", {"start": v(-65.97, 1.01) * mm, "end": v(-67.83, -0.36) * mm});
            skLineSegment(sketch, "E1939.4", {"start": v(-49.57, 10.65) * mm, "end": v(-52.42, 9.23) * mm});
            skLineSegment(sketch, "E1939.5", {"start": v(-45.48, 12.37) * mm, "end": v(-49.57, 10.65) * mm});
            skLineSegment(sketch, "E1939.6", {"start": v(-43.46, 13.22) * mm, "end": v(-45.48, 12.37) * mm});
            skLineSegment(sketch, "E1939.8", {"start": v(-52.42, 9.23) * mm, "end": v(-53.82, 8.53) * mm});
            skLineSegment(sketch, "E1939.9", {"start": v(-53.82, 8.53) * mm, "end": v(-56.7, 7.09) * mm});
            skLineSegment(sketch, "E1939.10", {"start": v(-56.7, 7.09) * mm, "end": v(-58.97, 5.65) * mm});
            skLineSegment(sketch, "E1939.11", {"start": v(-58.97, 5.65) * mm, "end": v(-60.07, 4.95) * mm});
            skLineSegment(sketch, "E1939.12", {"start": v(-60.07, 4.95) * mm, "end": v(-62.25, 3.52) * mm});
            skLineSegment(sketch, "E1939.13", {"start": v(-62.25, 3.52) * mm, "end": v(-65.97, 1.01) * mm});
            skLineSegment(sketch, "E1940", {"start": v(-75.93, -7.77) * mm, "end": v(-74.65, -6.5) * mm});
            skLineSegment(sketch, "E1941", {"start": v(-40.24, 14.92) * mm, "end": v(-43.46, 13.22) * mm});
            skArc(sketch, "E1942", {"start": v(-35.18, 16.97) * mm, "mid": v(-18.13, 32.9) * mm, "end": v(-27.43, 54.3) * mm});
            skLineSegment(sketch, "E1943", {"start": v(-10.95, 16.86) * mm, "end": v(-11.37, 15.72) * mm});
            skLineSegment(sketch, "E1944", {"start": v(-10.36, 19.39) * mm, "end": v(-9.59, 19.97) * mm});
            skLineSegment(sketch, "E1945", {"start": v(-30.93, 58.57) * mm, "end": v(-27.43, 54.3) * mm});
            skLineSegment(sketch, "E1946", {"start": v(-40.24, 14.92) * mm, "end": v(-35.18, 16.97) * mm});
            skLineSegment(sketch, "E1947", {"start": v(-6.48, 47.32) * mm, "end": v(-6.1, 46.16) * mm});
            skLineSegment(sketch, "E1948", {"start": v(-5.7, 43.63) * mm, "end": v(-5.32, 42.47) * mm});
            skCircle(sketch, "E1949", {"center": v(-191.13, -45.3) * mm, "radius": 19.71 * mm});
            skCircle(sketch, "E1950", {"center": v(-191.05, -45.26) * mm, "radius": 21 * mm});
            skSolve(sketch);
        }
        {
            var Q0;
            Q0=makeQuery(id+"F0.imprint","IMPRINT",FACE,{"disambiguationData":[TD([[makeQuery(id+"F0.imprint","IMPRINT",EDGE,{"derivedFrom":sQuery(id+"F0.wireOp",EDGE,"E290")}),1.0]])]});
            var Q1;
            Q1=makeQuery(id+"F0.imprint","IMPRINT",FACE,{"disambiguationData":[TD([[makeQuery(id+"F0.imprint","IMPRINT",EDGE,{"derivedFrom":sQuery(id+"F0.wireOp",EDGE,"E0")}),1.0]])]});
            extrude(context, id + "F1", {"entities" : qUnion([Q0, Q1]), "depth" : 10 * mm, "offsetDistance" : 25 * mm});
        }
    });
